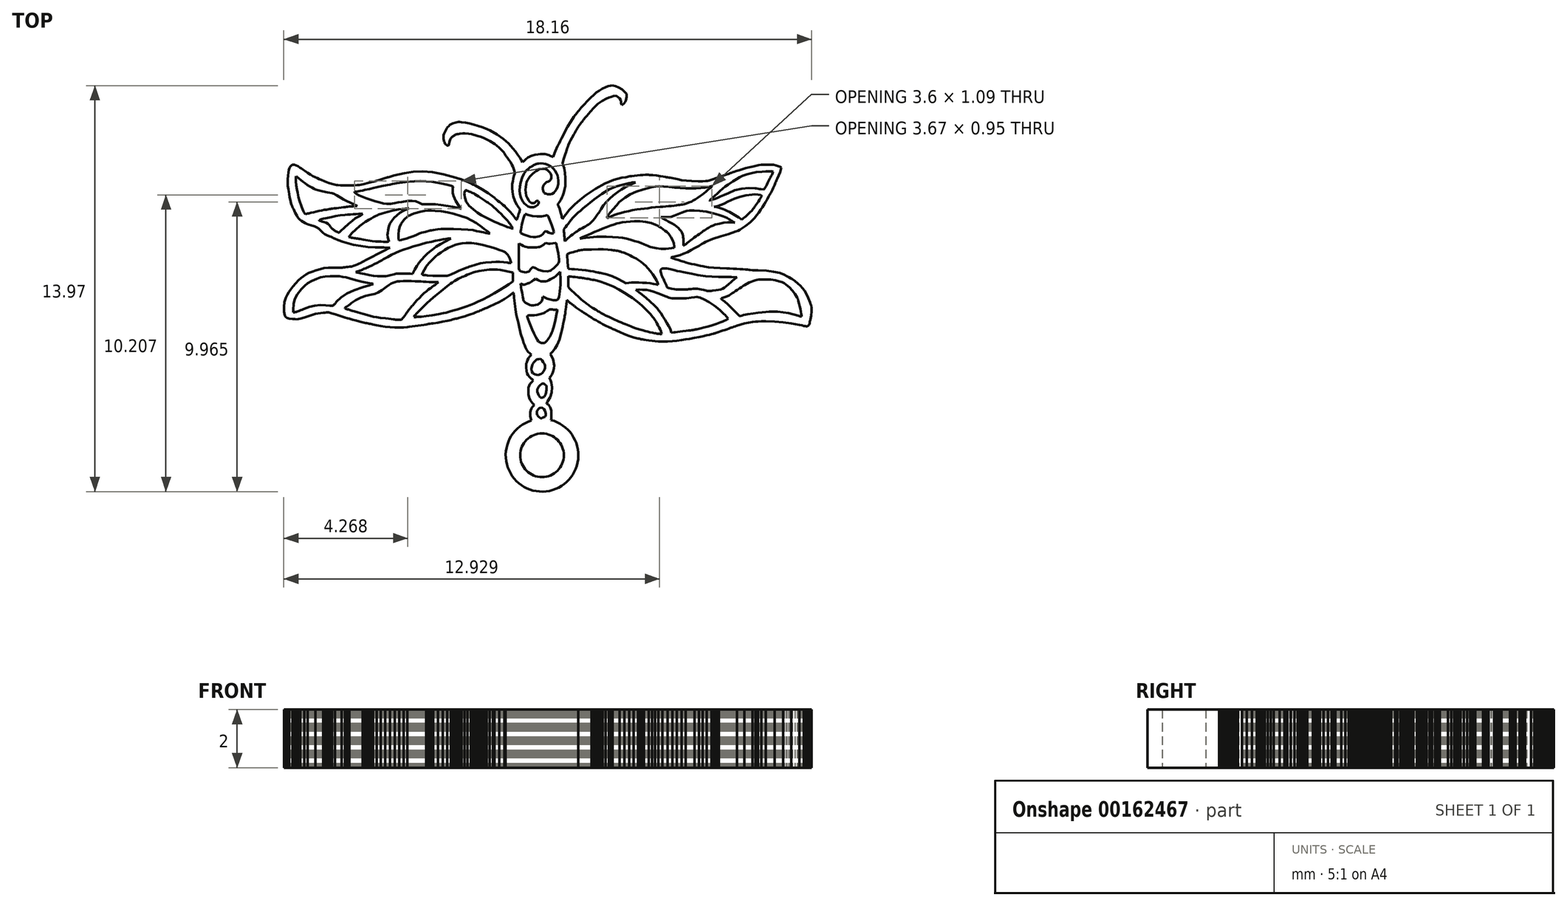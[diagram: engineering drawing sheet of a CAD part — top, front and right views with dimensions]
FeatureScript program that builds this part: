
annotation { "Feature Type Name" : "Feature", "Feature Type Description" : "" }
export const myFeature = defineFeature(function(context is Context, id is Id, definition is map)
    precondition{}
    {
        {
            var Q0;
            Q0=qCreatedBy(makeId("Top.planeOp"),FACE);
            var sketch = newSketch(context, id + "F0", { "sketchPlane" : qUnion([Q0])});
            skLineSegment(sketch, "E0", {"start": v(-0.38, -5.85) * mm, "end": v(-0.42, -5.82) * mm});
            skLineSegment(sketch, "E1", {"start": v(-0.42, -5.82) * mm, "end": v(-0.47, -5.77) * mm});
            skLineSegment(sketch, "E2", {"start": v(-0.47, -5.77) * mm, "end": v(-0.52, -5.72) * mm});
            skLineSegment(sketch, "E3", {"start": v(-0.52, -5.72) * mm, "end": v(-0.56, -5.66) * mm});
            skLineSegment(sketch, "E4", {"start": v(-0.56, -5.66) * mm, "end": v(-0.6, -5.52) * mm});
            skLineSegment(sketch, "E5", {"start": v(-0.6, -5.52) * mm, "end": v(-0.6, -5.39) * mm});
            skLineSegment(sketch, "E6", {"start": v(-0.6, -5.39) * mm, "end": v(-0.58, -5.32) * mm});
            skLineSegment(sketch, "E7", {"start": v(-0.58, -5.32) * mm, "end": v(-0.56, -5.26) * mm});
            skLineSegment(sketch, "E8", {"start": v(-0.56, -5.26) * mm, "end": v(-0.53, -5.21) * mm});
            skLineSegment(sketch, "E9", {"start": v(-0.53, -5.21) * mm, "end": v(-0.5, -5.17) * mm});
            skLineSegment(sketch, "E10", {"start": v(-0.5, -5.17) * mm, "end": v(-0.46, -5.13) * mm});
            skLineSegment(sketch, "E11", {"start": v(-0.46, -5.13) * mm, "end": v(-0.52, -5.07) * mm});
            skLineSegment(sketch, "E12", {"start": v(-0.52, -5.07) * mm, "end": v(-0.6, -4.97) * mm});
            skLineSegment(sketch, "E13", {"start": v(-0.6, -4.97) * mm, "end": v(-0.64, -4.87) * mm});
            skLineSegment(sketch, "E14", {"start": v(-0.64, -4.87) * mm, "end": v(-0.66, -4.76) * mm});
            skLineSegment(sketch, "E15", {"start": v(-0.66, -4.76) * mm, "end": v(-0.67, -4.62) * mm});
            skLineSegment(sketch, "E16", {"start": v(-0.67, -4.62) * mm, "end": v(-0.66, -4.53) * mm});
            skLineSegment(sketch, "E17", {"start": v(-0.66, -4.53) * mm, "end": v(-0.64, -4.47) * mm});
            skLineSegment(sketch, "E18", {"start": v(-0.64, -4.47) * mm, "end": v(-0.6, -4.4) * mm});
            skLineSegment(sketch, "E19", {"start": v(-0.6, -4.4) * mm, "end": v(-0.55, -4.34) * mm});
            skLineSegment(sketch, "E20", {"start": v(-0.55, -4.34) * mm, "end": v(-0.5, -4.28) * mm});
            skLineSegment(sketch, "E21", {"start": v(-0.5, -4.28) * mm, "end": v(-0.52, -4.26) * mm});
            skLineSegment(sketch, "E22", {"start": v(-0.52, -4.26) * mm, "end": v(-0.54, -4.25) * mm});
            skLineSegment(sketch, "E23", {"start": v(-0.54, -4.25) * mm, "end": v(-0.56, -4.23) * mm});
            skLineSegment(sketch, "E24", {"start": v(-0.56, -4.23) * mm, "end": v(-0.6, -4.2) * mm});
            skLineSegment(sketch, "E25", {"start": v(-0.6, -4.2) * mm, "end": v(-0.62, -4.17) * mm});
            skLineSegment(sketch, "E26", {"start": v(-0.62, -4.17) * mm, "end": v(-0.67, -4.1) * mm});
            skLineSegment(sketch, "E27", {"start": v(-0.67, -4.1) * mm, "end": v(-0.7, -4.04) * mm});
            skLineSegment(sketch, "E28", {"start": v(-0.7, -4.04) * mm, "end": v(-0.73, -3.95) * mm});
            skLineSegment(sketch, "E29", {"start": v(-0.73, -3.95) * mm, "end": v(-0.74, -3.85) * mm});
            skLineSegment(sketch, "E30", {"start": v(-0.74, -3.85) * mm, "end": v(-0.74, -3.79) * mm});
            skLineSegment(sketch, "E31", {"start": v(-0.74, -3.79) * mm, "end": v(-0.74, -3.74) * mm});
            skLineSegment(sketch, "E32", {"start": v(-0.74, -3.74) * mm, "end": v(-0.73, -3.7) * mm});
            skLineSegment(sketch, "E33", {"start": v(-0.73, -3.7) * mm, "end": v(-0.72, -3.65) * mm});
            skLineSegment(sketch, "E34", {"start": v(-0.72, -3.65) * mm, "end": v(-0.7, -3.59) * mm});
            skLineSegment(sketch, "E35", {"start": v(-0.7, -3.59) * mm, "end": v(-0.67, -3.53) * mm});
            skLineSegment(sketch, "E36", {"start": v(-0.67, -3.53) * mm, "end": v(-0.63, -3.48) * mm});
            skLineSegment(sketch, "E37", {"start": v(-0.63, -3.48) * mm, "end": v(-0.6, -3.44) * mm});
            skLineSegment(sketch, "E38", {"start": v(-0.6, -3.44) * mm, "end": v(-0.56, -3.4) * mm});
            skLineSegment(sketch, "E39", {"start": v(-0.56, -3.4) * mm, "end": v(-0.62, -3.35) * mm});
            skLineSegment(sketch, "E40", {"start": v(-0.62, -3.35) * mm, "end": v(-0.67, -3.3) * mm});
            skLineSegment(sketch, "E41", {"start": v(-0.67, -3.3) * mm, "end": v(-0.72, -3.23) * mm});
            skLineSegment(sketch, "E42", {"start": v(-0.72, -3.23) * mm, "end": v(-0.77, -3.15) * mm});
            skLineSegment(sketch, "E43", {"start": v(-0.77, -3.15) * mm, "end": v(-0.8, -3.08) * mm});
            skLineSegment(sketch, "E44", {"start": v(-0.8, -3.08) * mm, "end": v(-0.8, -3.04) * mm});
            skLineSegment(sketch, "E45", {"start": v(-0.8, -3.04) * mm, "end": v(-0.82, -3) * mm});
            skLineSegment(sketch, "E46", {"start": v(-0.82, -3) * mm, "end": v(-0.84, -2.94) * mm});
            skLineSegment(sketch, "E47", {"start": v(-0.84, -2.94) * mm, "end": v(-0.86, -2.9) * mm});
            skLineSegment(sketch, "E48", {"start": v(-0.86, -2.9) * mm, "end": v(-0.93, -2.67) * mm});
            skLineSegment(sketch, "E49", {"start": v(-0.93, -2.67) * mm, "end": v(-1, -2.37) * mm});
            skLineSegment(sketch, "E50", {"start": v(-1, -2.37) * mm, "end": v(-1, -2.31) * mm});
            skLineSegment(sketch, "E51", {"start": v(-1, -2.31) * mm, "end": v(-1.02, -2.26) * mm});
            skLineSegment(sketch, "E52", {"start": v(-1.02, -2.26) * mm, "end": v(-1.03, -2.2) * mm});
            skLineSegment(sketch, "E53", {"start": v(-1.03, -2.2) * mm, "end": v(-1.04, -2.17) * mm});
            skLineSegment(sketch, "E54", {"start": v(-1.04, -2.17) * mm, "end": v(-1.08, -2.02) * mm});
            skLineSegment(sketch, "E55", {"start": v(-1.08, -2.02) * mm, "end": v(-1.1, -1.84) * mm});
            skLineSegment(sketch, "E56", {"start": v(-1.1, -1.84) * mm, "end": v(-1.14, -1.64) * mm});
            skLineSegment(sketch, "E57", {"start": v(-1.14, -1.64) * mm, "end": v(-1.16, -1.44) * mm});
            skLineSegment(sketch, "E58", {"start": v(-1.16, -1.44) * mm, "end": v(-1.16, -1.37) * mm});
            skLineSegment(sketch, "E59", {"start": v(-1.16, -1.37) * mm, "end": v(-1.17, -1.32) * mm});
            skLineSegment(sketch, "E60", {"start": v(-1.17, -1.32) * mm, "end": v(-1.17, -1.28) * mm});
            skLineSegment(sketch, "E61", {"start": v(-1.17, -1.28) * mm, "end": v(-1.18, -1.27) * mm});
            skLineSegment(sketch, "E62", {"start": v(-1.18, -1.27) * mm, "end": v(-1.19, -1.27) * mm});
            skLineSegment(sketch, "E63", {"start": v(-1.19, -1.27) * mm, "end": v(-1.22, -1.29) * mm});
            skLineSegment(sketch, "E64", {"start": v(-1.22, -1.29) * mm, "end": v(-1.33, -1.38) * mm});
            skLineSegment(sketch, "E65", {"start": v(-1.33, -1.38) * mm, "end": v(-1.5, -1.49) * mm});
            skLineSegment(sketch, "E66", {"start": v(-1.5, -1.49) * mm, "end": v(-1.67, -1.59) * mm});
            skLineSegment(sketch, "E67", {"start": v(-1.67, -1.59) * mm, "end": v(-1.84, -1.67) * mm});
            skLineSegment(sketch, "E68", {"start": v(-1.84, -1.67) * mm, "end": v(-1.89, -1.69) * mm});
            skLineSegment(sketch, "E69", {"start": v(-1.89, -1.69) * mm, "end": v(-1.94, -1.71) * mm});
            skLineSegment(sketch, "E70", {"start": v(-1.94, -1.71) * mm, "end": v(-2, -1.74) * mm});
            skLineSegment(sketch, "E71", {"start": v(-2, -1.74) * mm, "end": v(-2.05, -1.76) * mm});
            skLineSegment(sketch, "E72", {"start": v(-2.05, -1.76) * mm, "end": v(-2.1, -1.78) * mm});
            skLineSegment(sketch, "E73", {"start": v(-2.1, -1.78) * mm, "end": v(-2.15, -1.8) * mm});
            skLineSegment(sketch, "E74", {"start": v(-2.15, -1.8) * mm, "end": v(-2.2, -1.83) * mm});
            skLineSegment(sketch, "E75", {"start": v(-2.2, -1.83) * mm, "end": v(-2.24, -1.85) * mm});
            skLineSegment(sketch, "E76", {"start": v(-2.24, -1.85) * mm, "end": v(-2.28, -1.86) * mm});
            skLineSegment(sketch, "E77", {"start": v(-2.28, -1.86) * mm, "end": v(-2.32, -1.88) * mm});
            skLineSegment(sketch, "E78", {"start": v(-2.32, -1.88) * mm, "end": v(-2.37, -1.9) * mm});
            skLineSegment(sketch, "E79", {"start": v(-2.37, -1.9) * mm, "end": v(-2.41, -1.92) * mm});
            skLineSegment(sketch, "E80", {"start": v(-2.41, -1.92) * mm, "end": v(-2.47, -1.95) * mm});
            skLineSegment(sketch, "E81", {"start": v(-2.47, -1.95) * mm, "end": v(-2.55, -1.98) * mm});
            skLineSegment(sketch, "E82", {"start": v(-2.55, -1.98) * mm, "end": v(-2.65, -2.01) * mm});
            skLineSegment(sketch, "E83", {"start": v(-2.65, -2.01) * mm, "end": v(-2.75, -2.05) * mm});
            skLineSegment(sketch, "E84", {"start": v(-2.75, -2.05) * mm, "end": v(-2.86, -2.08) * mm});
            skLineSegment(sketch, "E85", {"start": v(-2.86, -2.08) * mm, "end": v(-2.96, -2.1) * mm});
            skLineSegment(sketch, "E86", {"start": v(-2.96, -2.1) * mm, "end": v(-3.05, -2.13) * mm});
            skLineSegment(sketch, "E87", {"start": v(-3.05, -2.13) * mm, "end": v(-3.12, -2.15) * mm});
            skLineSegment(sketch, "E88", {"start": v(-3.12, -2.15) * mm, "end": v(-3.16, -2.16) * mm});
            skLineSegment(sketch, "E89", {"start": v(-3.16, -2.16) * mm, "end": v(-3.22, -2.18) * mm});
            skLineSegment(sketch, "E90", {"start": v(-3.22, -2.18) * mm, "end": v(-3.27, -2.19) * mm});
            skLineSegment(sketch, "E91", {"start": v(-3.27, -2.19) * mm, "end": v(-3.32, -2.2) * mm});
            skLineSegment(sketch, "E92", {"start": v(-3.32, -2.2) * mm, "end": v(-3.45, -2.23) * mm});
            skLineSegment(sketch, "E93", {"start": v(-3.45, -2.23) * mm, "end": v(-3.6, -2.27) * mm});
            skLineSegment(sketch, "E94", {"start": v(-3.6, -2.27) * mm, "end": v(-3.78, -2.3) * mm});
            skLineSegment(sketch, "E95", {"start": v(-3.78, -2.3) * mm, "end": v(-3.93, -2.32) * mm});
            skLineSegment(sketch, "E96", {"start": v(-3.93, -2.32) * mm, "end": v(-4, -2.33) * mm});
            skLineSegment(sketch, "E97", {"start": v(-4, -2.33) * mm, "end": v(-4.05, -2.33) * mm});
            skLineSegment(sketch, "E98", {"start": v(-4.05, -2.33) * mm, "end": v(-4.1, -2.34) * mm});
            skLineSegment(sketch, "E99", {"start": v(-4.1, -2.34) * mm, "end": v(-4.13, -2.35) * mm});
            skLineSegment(sketch, "E100", {"start": v(-4.13, -2.35) * mm, "end": v(-4.18, -2.36) * mm});
            skLineSegment(sketch, "E101", {"start": v(-4.18, -2.36) * mm, "end": v(-4.26, -2.37) * mm});
            skLineSegment(sketch, "E102", {"start": v(-4.26, -2.37) * mm, "end": v(-4.36, -2.38) * mm});
            skLineSegment(sketch, "E103", {"start": v(-4.36, -2.38) * mm, "end": v(-4.46, -2.4) * mm});
            skLineSegment(sketch, "E104", {"start": v(-4.46, -2.4) * mm, "end": v(-4.57, -2.42) * mm});
            skLineSegment(sketch, "E105", {"start": v(-4.57, -2.42) * mm, "end": v(-4.67, -2.43) * mm});
            skLineSegment(sketch, "E106", {"start": v(-4.67, -2.43) * mm, "end": v(-4.76, -2.44) * mm});
            skLineSegment(sketch, "E107", {"start": v(-4.76, -2.44) * mm, "end": v(-4.83, -2.45) * mm});
            skLineSegment(sketch, "E108", {"start": v(-4.83, -2.45) * mm, "end": v(-4.96, -2.46) * mm});
            skLineSegment(sketch, "E109", {"start": v(-4.96, -2.46) * mm, "end": v(-5.1, -2.47) * mm});
            skLineSegment(sketch, "E110", {"start": v(-5.1, -2.47) * mm, "end": v(-5.26, -2.46) * mm});
            skLineSegment(sketch, "E111", {"start": v(-5.26, -2.46) * mm, "end": v(-5.42, -2.45) * mm});
            skLineSegment(sketch, "E112", {"start": v(-5.42, -2.45) * mm, "end": v(-5.59, -2.44) * mm});
            skLineSegment(sketch, "E113", {"start": v(-5.59, -2.44) * mm, "end": v(-5.74, -2.42) * mm});
            skLineSegment(sketch, "E114", {"start": v(-5.74, -2.42) * mm, "end": v(-5.88, -2.4) * mm});
            skLineSegment(sketch, "E115", {"start": v(-5.88, -2.4) * mm, "end": v(-6, -2.36) * mm});
            skLineSegment(sketch, "E116", {"start": v(-6, -2.36) * mm, "end": v(-6.05, -2.35) * mm});
            skLineSegment(sketch, "E117", {"start": v(-6.05, -2.35) * mm, "end": v(-6.1, -2.34) * mm});
            skLineSegment(sketch, "E118", {"start": v(-6.1, -2.34) * mm, "end": v(-6.14, -2.33) * mm});
            skLineSegment(sketch, "E119", {"start": v(-6.14, -2.33) * mm, "end": v(-6.18, -2.32) * mm});
            skLineSegment(sketch, "E120", {"start": v(-6.18, -2.32) * mm, "end": v(-6.22, -2.32) * mm});
            skLineSegment(sketch, "E121", {"start": v(-6.22, -2.32) * mm, "end": v(-6.27, -2.3) * mm});
            skLineSegment(sketch, "E122", {"start": v(-6.27, -2.3) * mm, "end": v(-6.32, -2.3) * mm});
            skLineSegment(sketch, "E123", {"start": v(-6.32, -2.3) * mm, "end": v(-6.36, -2.28) * mm});
            skLineSegment(sketch, "E124", {"start": v(-6.36, -2.28) * mm, "end": v(-6.47, -2.25) * mm});
            skLineSegment(sketch, "E125", {"start": v(-6.47, -2.25) * mm, "end": v(-6.59, -2.22) * mm});
            skLineSegment(sketch, "E126", {"start": v(-6.59, -2.22) * mm, "end": v(-6.71, -2.2) * mm});
            skLineSegment(sketch, "E127", {"start": v(-6.71, -2.2) * mm, "end": v(-6.82, -2.16) * mm});
            skLineSegment(sketch, "E128", {"start": v(-6.82, -2.16) * mm, "end": v(-6.89, -2.15) * mm});
            skLineSegment(sketch, "E129", {"start": v(-6.89, -2.15) * mm, "end": v(-6.98, -2.12) * mm});
            skLineSegment(sketch, "E130", {"start": v(-6.98, -2.12) * mm, "end": v(-7.1, -2.08) * mm});
            skLineSegment(sketch, "E131", {"start": v(-7.1, -2.08) * mm, "end": v(-7.2, -2.05) * mm});
            skLineSegment(sketch, "E132", {"start": v(-7.2, -2.05) * mm, "end": v(-7.32, -2) * mm});
            skLineSegment(sketch, "E133", {"start": v(-7.32, -2) * mm, "end": v(-7.42, -1.98) * mm});
            skLineSegment(sketch, "E134", {"start": v(-7.42, -1.98) * mm, "end": v(-7.49, -1.96) * mm});
            skLineSegment(sketch, "E135", {"start": v(-7.49, -1.96) * mm, "end": v(-7.53, -1.95) * mm});
            skLineSegment(sketch, "E136", {"start": v(-7.53, -1.95) * mm, "end": v(-7.56, -1.95) * mm});
            skLineSegment(sketch, "E137", {"start": v(-7.56, -1.95) * mm, "end": v(-7.6, -1.95) * mm});
            skLineSegment(sketch, "E138", {"start": v(-7.6, -1.95) * mm, "end": v(-7.66, -1.95) * mm});
            skLineSegment(sketch, "E139", {"start": v(-7.66, -1.95) * mm, "end": v(-7.72, -1.96) * mm});
            skLineSegment(sketch, "E140", {"start": v(-7.72, -1.96) * mm, "end": v(-7.99, -2) * mm});
            skLineSegment(sketch, "E141", {"start": v(-7.99, -2) * mm, "end": v(-8.25, -2.08) * mm});
            skLineSegment(sketch, "E142", {"start": v(-8.25, -2.08) * mm, "end": v(-8.38, -2.13) * mm});
            skLineSegment(sketch, "E143", {"start": v(-8.38, -2.13) * mm, "end": v(-8.5, -2.16) * mm});
            skLineSegment(sketch, "E144", {"start": v(-8.5, -2.16) * mm, "end": v(-8.58, -2.17) * mm});
            skLineSegment(sketch, "E145", {"start": v(-8.58, -2.17) * mm, "end": v(-8.64, -2.18) * mm});
            skLineSegment(sketch, "E146", {"start": v(-8.64, -2.18) * mm, "end": v(-8.7, -2.18) * mm});
            skLineSegment(sketch, "E147", {"start": v(-8.7, -2.18) * mm, "end": v(-8.78, -2.17) * mm});
            skLineSegment(sketch, "E148", {"start": v(-8.78, -2.17) * mm, "end": v(-8.9, -2.16) * mm});
            skLineSegment(sketch, "E149", {"start": v(-8.9, -2.16) * mm, "end": v(-8.97, -2.14) * mm});
            skLineSegment(sketch, "E150", {"start": v(-8.97, -2.14) * mm, "end": v(-9.01, -2.1) * mm});
            skLineSegment(sketch, "E151", {"start": v(-9.01, -2.1) * mm, "end": v(-9.05, -2.04) * mm});
            skLineSegment(sketch, "E152", {"start": v(-9.05, -2.04) * mm, "end": v(-9.07, -1.92) * mm});
            skLineSegment(sketch, "E153", {"start": v(-9.07, -1.92) * mm, "end": v(-9.08, -1.76) * mm});
            skLineSegment(sketch, "E154", {"start": v(-9.08, -1.76) * mm, "end": v(-9.05, -1.6) * mm});
            skLineSegment(sketch, "E155", {"start": v(-9.05, -1.6) * mm, "end": v(-9, -1.44) * mm});
            skLineSegment(sketch, "E156", {"start": v(-9, -1.44) * mm, "end": v(-8.96, -1.33) * mm});
            skLineSegment(sketch, "E157", {"start": v(-8.96, -1.33) * mm, "end": v(-8.9, -1.24) * mm});
            skLineSegment(sketch, "E158", {"start": v(-8.9, -1.24) * mm, "end": v(-8.85, -1.15) * mm});
            skLineSegment(sketch, "E159", {"start": v(-8.85, -1.15) * mm, "end": v(-8.77, -1.06) * mm});
            skLineSegment(sketch, "E160", {"start": v(-8.77, -1.06) * mm, "end": v(-8.67, -0.94) * mm});
            skLineSegment(sketch, "E161", {"start": v(-8.67, -0.94) * mm, "end": v(-8.57, -0.84) * mm});
            skLineSegment(sketch, "E162", {"start": v(-8.57, -0.84) * mm, "end": v(-8.49, -0.76) * mm});
            skLineSegment(sketch, "E163", {"start": v(-8.49, -0.76) * mm, "end": v(-8.4, -0.7) * mm});
            skLineSegment(sketch, "E164", {"start": v(-8.4, -0.7) * mm, "end": v(-8.31, -0.64) * mm});
            skLineSegment(sketch, "E165", {"start": v(-8.31, -0.64) * mm, "end": v(-8.21, -0.6) * mm});
            skLineSegment(sketch, "E166", {"start": v(-8.21, -0.6) * mm, "end": v(-8.1, -0.54) * mm});
            skLineSegment(sketch, "E167", {"start": v(-8.1, -0.54) * mm, "end": v(-7.97, -0.5) * mm});
            skLineSegment(sketch, "E168", {"start": v(-7.97, -0.5) * mm, "end": v(-7.83, -0.45) * mm});
            skLineSegment(sketch, "E169", {"start": v(-7.83, -0.45) * mm, "end": v(-7.7, -0.43) * mm});
            skLineSegment(sketch, "E170", {"start": v(-7.7, -0.43) * mm, "end": v(-7.55, -0.41) * mm});
            skLineSegment(sketch, "E171", {"start": v(-7.55, -0.41) * mm, "end": v(-7.34, -0.4) * mm});
            skLineSegment(sketch, "E172", {"start": v(-7.34, -0.4) * mm, "end": v(-7.23, -0.4) * mm});
            skLineSegment(sketch, "E173", {"start": v(-7.23, -0.4) * mm, "end": v(-7.13, -0.4) * mm});
            skLineSegment(sketch, "E174", {"start": v(-7.13, -0.4) * mm, "end": v(-7.06, -0.4) * mm});
            skLineSegment(sketch, "E175", {"start": v(-7.06, -0.4) * mm, "end": v(-7.03, -0.4) * mm});
            skLineSegment(sketch, "E176", {"start": v(-7.03, -0.4) * mm, "end": v(-7, -0.4) * mm});
            skLineSegment(sketch, "E177", {"start": v(-7, -0.4) * mm, "end": v(-6.97, -0.4) * mm});
            skLineSegment(sketch, "E178", {"start": v(-6.97, -0.4) * mm, "end": v(-6.92, -0.39) * mm});
            skLineSegment(sketch, "E179", {"start": v(-6.92, -0.39) * mm, "end": v(-6.87, -0.38) * mm});
            skLineSegment(sketch, "E180", {"start": v(-6.87, -0.38) * mm, "end": v(-6.8, -0.37) * mm});
            skLineSegment(sketch, "E181", {"start": v(-6.8, -0.37) * mm, "end": v(-6.75, -0.36) * mm});
            skLineSegment(sketch, "E182", {"start": v(-6.75, -0.36) * mm, "end": v(-6.69, -0.34) * mm});
            skLineSegment(sketch, "E183", {"start": v(-6.69, -0.34) * mm, "end": v(-6.6, -0.31) * mm});
            skLineSegment(sketch, "E184", {"start": v(-6.6, -0.31) * mm, "end": v(-6.55, -0.29) * mm});
            skLineSegment(sketch, "E185", {"start": v(-6.55, -0.29) * mm, "end": v(-6.49, -0.26) * mm});
            skLineSegment(sketch, "E186", {"start": v(-6.49, -0.26) * mm, "end": v(-6.43, -0.24) * mm});
            skLineSegment(sketch, "E187", {"start": v(-6.43, -0.24) * mm, "end": v(-6.4, -0.22) * mm});
            skLineSegment(sketch, "E188", {"start": v(-6.4, -0.22) * mm, "end": v(-6.2, -0.12) * mm});
            skLineSegment(sketch, "E189", {"start": v(-6.2, -0.12) * mm, "end": v(-6.02, -0.03) * mm});
            skLineSegment(sketch, "E190", {"start": v(-6.02, -0.03) * mm, "end": v(-5.88, 0.05) * mm});
            skLineSegment(sketch, "E191", {"start": v(-5.88, 0.05) * mm, "end": v(-5.77, 0.1) * mm});
            skLineSegment(sketch, "E192", {"start": v(-5.77, 0.1) * mm, "end": v(-5.68, 0.16) * mm});
            skLineSegment(sketch, "E193", {"start": v(-5.68, 0.16) * mm, "end": v(-5.58, 0.2) * mm});
            skLineSegment(sketch, "E194", {"start": v(-5.58, 0.2) * mm, "end": v(-5.49, 0.25) * mm});
            skLineSegment(sketch, "E195", {"start": v(-5.49, 0.25) * mm, "end": v(-5.42, 0.28) * mm});
            skLineSegment(sketch, "E196", {"start": v(-5.42, 0.28) * mm, "end": v(-5.43, 0.28) * mm});
            skLineSegment(sketch, "E197", {"start": v(-5.43, 0.28) * mm, "end": v(-5.48, 0.28) * mm});
            skLineSegment(sketch, "E198", {"start": v(-5.48, 0.28) * mm, "end": v(-5.54, 0.29) * mm});
            skLineSegment(sketch, "E199", {"start": v(-5.54, 0.29) * mm, "end": v(-5.62, 0.29) * mm});
            skLineSegment(sketch, "E200", {"start": v(-5.62, 0.29) * mm, "end": v(-5.93, 0.3) * mm});
            skLineSegment(sketch, "E201", {"start": v(-5.93, 0.3) * mm, "end": v(-6.19, 0.3) * mm});
            skLineSegment(sketch, "E202", {"start": v(-6.19, 0.3) * mm, "end": v(-6.43, 0.34) * mm});
            skLineSegment(sketch, "E203", {"start": v(-6.43, 0.34) * mm, "end": v(-6.68, 0.39) * mm});
            skLineSegment(sketch, "E204", {"start": v(-6.68, 0.39) * mm, "end": v(-6.85, 0.43) * mm});
            skLineSegment(sketch, "E205", {"start": v(-6.85, 0.43) * mm, "end": v(-7.04, 0.49) * mm});
            skLineSegment(sketch, "E206", {"start": v(-7.04, 0.49) * mm, "end": v(-7.21, 0.55) * mm});
            skLineSegment(sketch, "E207", {"start": v(-7.21, 0.55) * mm, "end": v(-7.34, 0.6) * mm});
            skLineSegment(sketch, "E208", {"start": v(-7.34, 0.6) * mm, "end": v(-7.37, 0.61) * mm});
            skLineSegment(sketch, "E209", {"start": v(-7.37, 0.61) * mm, "end": v(-7.41, 0.63) * mm});
            skLineSegment(sketch, "E210", {"start": v(-7.41, 0.63) * mm, "end": v(-7.46, 0.65) * mm});
            skLineSegment(sketch, "E211", {"start": v(-7.46, 0.65) * mm, "end": v(-7.5, 0.67) * mm});
            skLineSegment(sketch, "E212", {"start": v(-7.5, 0.67) * mm, "end": v(-7.6, 0.71) * mm});
            skLineSegment(sketch, "E213", {"start": v(-7.6, 0.71) * mm, "end": v(-7.67, 0.75) * mm});
            skLineSegment(sketch, "E214", {"start": v(-7.67, 0.75) * mm, "end": v(-7.73, 0.8) * mm});
            skLineSegment(sketch, "E215", {"start": v(-7.73, 0.8) * mm, "end": v(-7.8, 0.88) * mm});
            skLineSegment(sketch, "E216", {"start": v(-7.8, 0.88) * mm, "end": v(-7.84, 0.9) * mm});
            skLineSegment(sketch, "E217", {"start": v(-7.84, 0.9) * mm, "end": v(-7.87, 0.94) * mm});
            skLineSegment(sketch, "E218", {"start": v(-7.87, 0.94) * mm, "end": v(-7.9, 0.96) * mm});
            skLineSegment(sketch, "E219", {"start": v(-7.9, 0.96) * mm, "end": v(-7.92, 0.97) * mm});
            skLineSegment(sketch, "E220", {"start": v(-7.92, 0.97) * mm, "end": v(-7.94, 0.98) * mm});
            skLineSegment(sketch, "E221", {"start": v(-7.94, 0.98) * mm, "end": v(-7.96, 1) * mm});
            skLineSegment(sketch, "E222", {"start": v(-7.96, 1) * mm, "end": v(-7.99, 1) * mm});
            skLineSegment(sketch, "E223", {"start": v(-7.99, 1) * mm, "end": v(-8.02, 1.01) * mm});
            skLineSegment(sketch, "E224", {"start": v(-8.02, 1.01) * mm, "end": v(-8.14, 1.05) * mm});
            skLineSegment(sketch, "E225", {"start": v(-8.14, 1.05) * mm, "end": v(-8.23, 1.08) * mm});
            skLineSegment(sketch, "E226", {"start": v(-8.23, 1.08) * mm, "end": v(-8.3, 1.1) * mm});
            skLineSegment(sketch, "E227", {"start": v(-8.3, 1.1) * mm, "end": v(-8.35, 1.13) * mm});
            skLineSegment(sketch, "E228", {"start": v(-8.35, 1.13) * mm, "end": v(-8.41, 1.17) * mm});
            skLineSegment(sketch, "E229", {"start": v(-8.41, 1.17) * mm, "end": v(-8.47, 1.2) * mm});
            skLineSegment(sketch, "E230", {"start": v(-8.47, 1.2) * mm, "end": v(-8.52, 1.24) * mm});
            skLineSegment(sketch, "E231", {"start": v(-8.52, 1.24) * mm, "end": v(-8.55, 1.27) * mm});
            skLineSegment(sketch, "E232", {"start": v(-8.55, 1.27) * mm, "end": v(-8.59, 1.31) * mm});
            skLineSegment(sketch, "E233", {"start": v(-8.59, 1.31) * mm, "end": v(-8.63, 1.39) * mm});
            skLineSegment(sketch, "E234", {"start": v(-8.63, 1.39) * mm, "end": v(-8.68, 1.49) * mm});
            skLineSegment(sketch, "E235", {"start": v(-8.68, 1.49) * mm, "end": v(-8.74, 1.6) * mm});
            skLineSegment(sketch, "E236", {"start": v(-8.74, 1.6) * mm, "end": v(-8.77, 1.67) * mm});
            skLineSegment(sketch, "E237", {"start": v(-8.77, 1.67) * mm, "end": v(-8.8, 1.71) * mm});
            skLineSegment(sketch, "E238", {"start": v(-8.8, 1.71) * mm, "end": v(-8.81, 1.76) * mm});
            skLineSegment(sketch, "E239", {"start": v(-8.81, 1.76) * mm, "end": v(-8.83, 1.8) * mm});
            skLineSegment(sketch, "E240", {"start": v(-8.83, 1.8) * mm, "end": v(-8.84, 1.86) * mm});
            skLineSegment(sketch, "E241", {"start": v(-8.84, 1.86) * mm, "end": v(-8.86, 1.93) * mm});
            skLineSegment(sketch, "E242", {"start": v(-8.86, 1.93) * mm, "end": v(-8.87, 2.02) * mm});
            skLineSegment(sketch, "E243", {"start": v(-8.87, 2.02) * mm, "end": v(-8.9, 2.13) * mm});
            skLineSegment(sketch, "E244", {"start": v(-8.9, 2.13) * mm, "end": v(-8.92, 2.29) * mm});
            skLineSegment(sketch, "E245", {"start": v(-8.92, 2.29) * mm, "end": v(-8.94, 2.41) * mm});
            skLineSegment(sketch, "E246", {"start": v(-8.94, 2.41) * mm, "end": v(-8.94, 2.52) * mm});
            skLineSegment(sketch, "E247", {"start": v(-8.94, 2.52) * mm, "end": v(-8.94, 2.63) * mm});
            skLineSegment(sketch, "E248", {"start": v(-8.94, 2.63) * mm, "end": v(-8.93, 2.76) * mm});
            skLineSegment(sketch, "E249", {"start": v(-8.93, 2.76) * mm, "end": v(-8.92, 2.87) * mm});
            skLineSegment(sketch, "E250", {"start": v(-8.92, 2.87) * mm, "end": v(-8.9, 2.96) * mm});
            skLineSegment(sketch, "E251", {"start": v(-8.9, 2.96) * mm, "end": v(-8.87, 3.03) * mm});
            skLineSegment(sketch, "E252", {"start": v(-8.87, 3.03) * mm, "end": v(-8.85, 3.08) * mm});
            skLineSegment(sketch, "E253", {"start": v(-8.85, 3.08) * mm, "end": v(-8.82, 3.11) * mm});
            skLineSegment(sketch, "E254", {"start": v(-8.82, 3.11) * mm, "end": v(-8.79, 3.14) * mm});
            skLineSegment(sketch, "E255", {"start": v(-8.79, 3.14) * mm, "end": v(-8.75, 3.14) * mm});
            skLineSegment(sketch, "E256", {"start": v(-8.75, 3.14) * mm, "end": v(-8.7, 3.14) * mm});
            skLineSegment(sketch, "E257", {"start": v(-8.7, 3.14) * mm, "end": v(-8.66, 3.12) * mm});
            skLineSegment(sketch, "E258", {"start": v(-8.66, 3.12) * mm, "end": v(-8.6, 3.08) * mm});
            skLineSegment(sketch, "E259", {"start": v(-8.6, 3.08) * mm, "end": v(-8.52, 3.04) * mm});
            skLineSegment(sketch, "E260", {"start": v(-8.52, 3.04) * mm, "end": v(-8.47, 3) * mm});
            skLineSegment(sketch, "E261", {"start": v(-8.47, 3) * mm, "end": v(-8.43, 2.98) * mm});
            skLineSegment(sketch, "E262", {"start": v(-8.43, 2.98) * mm, "end": v(-8.38, 2.94) * mm});
            skLineSegment(sketch, "E263", {"start": v(-8.38, 2.94) * mm, "end": v(-8.34, 2.92) * mm});
            skLineSegment(sketch, "E264", {"start": v(-8.34, 2.92) * mm, "end": v(-8.25, 2.85) * mm});
            skLineSegment(sketch, "E265", {"start": v(-8.25, 2.85) * mm, "end": v(-8.16, 2.8) * mm});
            skLineSegment(sketch, "E266", {"start": v(-8.16, 2.8) * mm, "end": v(-8.07, 2.74) * mm});
            skLineSegment(sketch, "E267", {"start": v(-8.07, 2.74) * mm, "end": v(-8.02, 2.71) * mm});
            skLineSegment(sketch, "E268", {"start": v(-8.02, 2.71) * mm, "end": v(-7.99, 2.7) * mm});
            skLineSegment(sketch, "E269", {"start": v(-7.99, 2.7) * mm, "end": v(-7.93, 2.68) * mm});
            skLineSegment(sketch, "E270", {"start": v(-7.93, 2.68) * mm, "end": v(-7.86, 2.65) * mm});
            skLineSegment(sketch, "E271", {"start": v(-7.86, 2.65) * mm, "end": v(-7.79, 2.61) * mm});
            skLineSegment(sketch, "E272", {"start": v(-7.79, 2.61) * mm, "end": v(-7.67, 2.56) * mm});
            skLineSegment(sketch, "E273", {"start": v(-7.67, 2.56) * mm, "end": v(-7.55, 2.52) * mm});
            skLineSegment(sketch, "E274", {"start": v(-7.55, 2.52) * mm, "end": v(-7.42, 2.48) * mm});
            skLineSegment(sketch, "E275", {"start": v(-7.42, 2.48) * mm, "end": v(-7.27, 2.44) * mm});
            skLineSegment(sketch, "E276", {"start": v(-7.27, 2.44) * mm, "end": v(-7.22, 2.43) * mm});
            skLineSegment(sketch, "E277", {"start": v(-7.22, 2.43) * mm, "end": v(-7.13, 2.43) * mm});
            skLineSegment(sketch, "E278", {"start": v(-7.13, 2.43) * mm, "end": v(-7.02, 2.43) * mm});
            skLineSegment(sketch, "E279", {"start": v(-7.02, 2.43) * mm, "end": v(-6.9, 2.43) * mm});
            skLineSegment(sketch, "E280", {"start": v(-6.9, 2.43) * mm, "end": v(-6.77, 2.43) * mm});
            skLineSegment(sketch, "E281", {"start": v(-6.77, 2.43) * mm, "end": v(-6.65, 2.43) * mm});
            skLineSegment(sketch, "E282", {"start": v(-6.65, 2.43) * mm, "end": v(-6.55, 2.43) * mm});
            skLineSegment(sketch, "E283", {"start": v(-6.55, 2.43) * mm, "end": v(-6.48, 2.44) * mm});
            skLineSegment(sketch, "E284", {"start": v(-6.48, 2.44) * mm, "end": v(-6.35, 2.47) * mm});
            skLineSegment(sketch, "E285", {"start": v(-6.35, 2.47) * mm, "end": v(-6.16, 2.51) * mm});
            skLineSegment(sketch, "E286", {"start": v(-6.16, 2.51) * mm, "end": v(-5.95, 2.57) * mm});
            skLineSegment(sketch, "E287", {"start": v(-5.95, 2.57) * mm, "end": v(-5.75, 2.63) * mm});
            skLineSegment(sketch, "E288", {"start": v(-5.75, 2.63) * mm, "end": v(-5.66, 2.66) * mm});
            skLineSegment(sketch, "E289", {"start": v(-5.66, 2.66) * mm, "end": v(-5.6, 2.68) * mm});
            skLineSegment(sketch, "E290", {"start": v(-5.6, 2.68) * mm, "end": v(-5.54, 2.7) * mm});
            skLineSegment(sketch, "E291", {"start": v(-5.54, 2.7) * mm, "end": v(-5.51, 2.7) * mm});
            skLineSegment(sketch, "E292", {"start": v(-5.51, 2.7) * mm, "end": v(-5.49, 2.7) * mm});
            skLineSegment(sketch, "E293", {"start": v(-5.49, 2.7) * mm, "end": v(-5.43, 2.72) * mm});
            skLineSegment(sketch, "E294", {"start": v(-5.43, 2.72) * mm, "end": v(-5.36, 2.74) * mm});
            skLineSegment(sketch, "E295", {"start": v(-5.36, 2.74) * mm, "end": v(-5.28, 2.76) * mm});
            skLineSegment(sketch, "E296", {"start": v(-5.28, 2.76) * mm, "end": v(-4.93, 2.84) * mm});
            skLineSegment(sketch, "E297", {"start": v(-4.93, 2.84) * mm, "end": v(-4.63, 2.9) * mm});
            skLineSegment(sketch, "E298", {"start": v(-4.63, 2.9) * mm, "end": v(-4.3, 2.9) * mm});
            skLineSegment(sketch, "E299", {"start": v(-4.3, 2.9) * mm, "end": v(-3.96, 2.88) * mm});
            skLineSegment(sketch, "E300", {"start": v(-3.96, 2.88) * mm, "end": v(-3.58, 2.81) * mm});
            skLineSegment(sketch, "E301", {"start": v(-3.58, 2.81) * mm, "end": v(-3.17, 2.7) * mm});
            skLineSegment(sketch, "E302", {"start": v(-3.17, 2.7) * mm, "end": v(-3.08, 2.67) * mm});
            skLineSegment(sketch, "E303", {"start": v(-3.08, 2.67) * mm, "end": v(-3, 2.64) * mm});
            skLineSegment(sketch, "E304", {"start": v(-3, 2.64) * mm, "end": v(-2.9, 2.6) * mm});
            skLineSegment(sketch, "E305", {"start": v(-2.9, 2.6) * mm, "end": v(-2.8, 2.56) * mm});
            skLineSegment(sketch, "E306", {"start": v(-2.8, 2.56) * mm, "end": v(-2.7, 2.53) * mm});
            skLineSegment(sketch, "E307", {"start": v(-2.7, 2.53) * mm, "end": v(-2.62, 2.49) * mm});
            skLineSegment(sketch, "E308", {"start": v(-2.62, 2.49) * mm, "end": v(-2.55, 2.46) * mm});
            skLineSegment(sketch, "E309", {"start": v(-2.55, 2.46) * mm, "end": v(-2.5, 2.43) * mm});
            skLineSegment(sketch, "E310", {"start": v(-2.5, 2.43) * mm, "end": v(-2.25, 2.28) * mm});
            skLineSegment(sketch, "E311", {"start": v(-2.25, 2.28) * mm, "end": v(-2.05, 2.16) * mm});
            skLineSegment(sketch, "E312", {"start": v(-2.05, 2.16) * mm, "end": v(-1.9, 2.06) * mm});
            skLineSegment(sketch, "E313", {"start": v(-1.9, 2.06) * mm, "end": v(-1.82, 2) * mm});
            skLineSegment(sketch, "E314", {"start": v(-1.82, 2) * mm, "end": v(-1.8, 1.97) * mm});
            skLineSegment(sketch, "E315", {"start": v(-1.8, 1.97) * mm, "end": v(-1.76, 1.94) * mm});
            skLineSegment(sketch, "E316", {"start": v(-1.76, 1.94) * mm, "end": v(-1.7, 1.9) * mm});
            skLineSegment(sketch, "E317", {"start": v(-1.7, 1.9) * mm, "end": v(-1.65, 1.85) * mm});
            skLineSegment(sketch, "E318", {"start": v(-1.65, 1.85) * mm, "end": v(-1.6, 1.8) * mm});
            skLineSegment(sketch, "E319", {"start": v(-1.6, 1.8) * mm, "end": v(-1.53, 1.75) * mm});
            skLineSegment(sketch, "E320", {"start": v(-1.53, 1.75) * mm, "end": v(-1.48, 1.71) * mm});
            skLineSegment(sketch, "E321", {"start": v(-1.48, 1.71) * mm, "end": v(-1.44, 1.68) * mm});
            skLineSegment(sketch, "E322", {"start": v(-1.44, 1.68) * mm, "end": v(-1.38, 1.62) * mm});
            skLineSegment(sketch, "E323", {"start": v(-1.38, 1.62) * mm, "end": v(-1.3, 1.53) * mm});
            skLineSegment(sketch, "E324", {"start": v(-1.3, 1.53) * mm, "end": v(-1.21, 1.42) * mm});
            skLineSegment(sketch, "E325", {"start": v(-1.21, 1.42) * mm, "end": v(-1.13, 1.32) * mm});
            skLineSegment(sketch, "E326", {"start": v(-1.13, 1.32) * mm, "end": v(-1.1, 1.28) * mm});
            skLineSegment(sketch, "E327", {"start": v(-1.1, 1.28) * mm, "end": v(-1.08, 1.26) * mm});
            skLineSegment(sketch, "E328", {"start": v(-1.08, 1.26) * mm, "end": v(-1.06, 1.24) * mm});
            skLineSegment(sketch, "E329", {"start": v(-1.06, 1.24) * mm, "end": v(-1.06, 1.24) * mm});
            skLineSegment(sketch, "E330", {"start": v(-1.06, 1.24) * mm, "end": v(-1.05, 1.26) * mm});
            skLineSegment(sketch, "E331", {"start": v(-1.05, 1.26) * mm, "end": v(-1.04, 1.3) * mm});
            skLineSegment(sketch, "E332", {"start": v(-1.04, 1.3) * mm, "end": v(-1.02, 1.36) * mm});
            skLineSegment(sketch, "E333", {"start": v(-1.02, 1.36) * mm, "end": v(-1, 1.43) * mm});
            skLineSegment(sketch, "E334", {"start": v(-1, 1.43) * mm, "end": v(-0.98, 1.48) * mm});
            skLineSegment(sketch, "E335", {"start": v(-0.98, 1.48) * mm, "end": v(-0.97, 1.52) * mm});
            skLineSegment(sketch, "E336", {"start": v(-0.97, 1.52) * mm, "end": v(-0.96, 1.55) * mm});
            skLineSegment(sketch, "E337", {"start": v(-0.96, 1.55) * mm, "end": v(-0.96, 1.58) * mm});
            skLineSegment(sketch, "E338", {"start": v(-0.96, 1.58) * mm, "end": v(-0.96, 1.6) * mm});
            skLineSegment(sketch, "E339", {"start": v(-0.96, 1.6) * mm, "end": v(-0.96, 1.6) * mm});
            skLineSegment(sketch, "E340", {"start": v(-0.96, 1.6) * mm, "end": v(-0.96, 1.61) * mm});
            skLineSegment(sketch, "E341", {"start": v(-0.96, 1.61) * mm, "end": v(-0.96, 1.62) * mm});
            skLineSegment(sketch, "E342", {"start": v(-0.96, 1.62) * mm, "end": v(-1, 1.68) * mm});
            skLineSegment(sketch, "E343", {"start": v(-1, 1.68) * mm, "end": v(-1.06, 1.76) * mm});
            skLineSegment(sketch, "E344", {"start": v(-1.06, 1.76) * mm, "end": v(-1.1, 1.84) * mm});
            skLineSegment(sketch, "E345", {"start": v(-1.1, 1.84) * mm, "end": v(-1.14, 1.9) * mm});
            skLineSegment(sketch, "E346", {"start": v(-1.14, 1.9) * mm, "end": v(-1.18, 2.05) * mm});
            skLineSegment(sketch, "E347", {"start": v(-1.18, 2.05) * mm, "end": v(-1.2, 2.2) * mm});
            skLineSegment(sketch, "E348", {"start": v(-1.2, 2.2) * mm, "end": v(-1.22, 2.34) * mm});
            skLineSegment(sketch, "E349", {"start": v(-1.22, 2.34) * mm, "end": v(-1.21, 2.47) * mm});
            skLineSegment(sketch, "E350", {"start": v(-1.21, 2.47) * mm, "end": v(-1.2, 2.56) * mm});
            skLineSegment(sketch, "E351", {"start": v(-1.2, 2.56) * mm, "end": v(-1.18, 2.67) * mm});
            skLineSegment(sketch, "E352", {"start": v(-1.18, 2.67) * mm, "end": v(-1.16, 2.76) * mm});
            skLineSegment(sketch, "E353", {"start": v(-1.16, 2.76) * mm, "end": v(-1.13, 2.83) * mm});
            skLineSegment(sketch, "E354", {"start": v(-1.13, 2.83) * mm, "end": v(-1.13, 2.87) * mm});
            skLineSegment(sketch, "E355", {"start": v(-1.13, 2.87) * mm, "end": v(-1.14, 2.92) * mm});
            skLineSegment(sketch, "E356", {"start": v(-1.14, 2.92) * mm, "end": v(-1.16, 3) * mm});
            skLineSegment(sketch, "E357", {"start": v(-1.16, 3) * mm, "end": v(-1.2, 3.08) * mm});
            skLineSegment(sketch, "E358", {"start": v(-1.2, 3.08) * mm, "end": v(-1.23, 3.14) * mm});
            skLineSegment(sketch, "E359", {"start": v(-1.23, 3.14) * mm, "end": v(-1.28, 3.22) * mm});
            skLineSegment(sketch, "E360", {"start": v(-1.28, 3.22) * mm, "end": v(-1.33, 3.3) * mm});
            skLineSegment(sketch, "E361", {"start": v(-1.33, 3.3) * mm, "end": v(-1.39, 3.38) * mm});
            skLineSegment(sketch, "E362", {"start": v(-1.39, 3.38) * mm, "end": v(-1.4, 3.4) * mm});
            skLineSegment(sketch, "E363", {"start": v(-1.4, 3.4) * mm, "end": v(-1.43, 3.43) * mm});
            skLineSegment(sketch, "E364", {"start": v(-1.43, 3.43) * mm, "end": v(-1.44, 3.46) * mm});
            skLineSegment(sketch, "E365", {"start": v(-1.44, 3.46) * mm, "end": v(-1.46, 3.48) * mm});
            skLineSegment(sketch, "E366", {"start": v(-1.46, 3.48) * mm, "end": v(-1.48, 3.53) * mm});
            skLineSegment(sketch, "E367", {"start": v(-1.48, 3.53) * mm, "end": v(-1.52, 3.57) * mm});
            skLineSegment(sketch, "E368", {"start": v(-1.52, 3.57) * mm, "end": v(-1.58, 3.64) * mm});
            skLineSegment(sketch, "E369", {"start": v(-1.58, 3.64) * mm, "end": v(-1.66, 3.72) * mm});
            skLineSegment(sketch, "E370", {"start": v(-1.66, 3.72) * mm, "end": v(-1.75, 3.8) * mm});
            skLineSegment(sketch, "E371", {"start": v(-1.75, 3.8) * mm, "end": v(-1.82, 3.85) * mm});
            skLineSegment(sketch, "E372", {"start": v(-1.82, 3.85) * mm, "end": v(-1.98, 3.95) * mm});
            skLineSegment(sketch, "E373", {"start": v(-1.98, 3.95) * mm, "end": v(-2.1, 4.02) * mm});
            skLineSegment(sketch, "E374", {"start": v(-2.1, 4.02) * mm, "end": v(-2.2, 4.06) * mm});
            skLineSegment(sketch, "E375", {"start": v(-2.2, 4.06) * mm, "end": v(-2.32, 4.1) * mm});
            skLineSegment(sketch, "E376", {"start": v(-2.32, 4.1) * mm, "end": v(-2.36, 4.11) * mm});
            skLineSegment(sketch, "E377", {"start": v(-2.36, 4.11) * mm, "end": v(-2.41, 4.13) * mm});
            skLineSegment(sketch, "E378", {"start": v(-2.41, 4.13) * mm, "end": v(-2.45, 4.14) * mm});
            skLineSegment(sketch, "E379", {"start": v(-2.45, 4.14) * mm, "end": v(-2.48, 4.15) * mm});
            skLineSegment(sketch, "E380", {"start": v(-2.48, 4.15) * mm, "end": v(-2.54, 4.17) * mm});
            skLineSegment(sketch, "E381", {"start": v(-2.54, 4.17) * mm, "end": v(-2.62, 4.19) * mm});
            skLineSegment(sketch, "E382", {"start": v(-2.62, 4.19) * mm, "end": v(-2.72, 4.2) * mm});
            skLineSegment(sketch, "E383", {"start": v(-2.72, 4.2) * mm, "end": v(-2.84, 4.22) * mm});
            skLineSegment(sketch, "E384", {"start": v(-2.84, 4.22) * mm, "end": v(-2.92, 4.22) * mm});
            skLineSegment(sketch, "E385", {"start": v(-2.92, 4.22) * mm, "end": v(-3.02, 4.2) * mm});
            skLineSegment(sketch, "E386", {"start": v(-3.02, 4.2) * mm, "end": v(-3.08, 4.2) * mm});
            skLineSegment(sketch, "E387", {"start": v(-3.08, 4.2) * mm, "end": v(-3.12, 4.19) * mm});
            skLineSegment(sketch, "E388", {"start": v(-3.12, 4.19) * mm, "end": v(-3.15, 4.18) * mm});
            skLineSegment(sketch, "E389", {"start": v(-3.15, 4.18) * mm, "end": v(-3.17, 4.18) * mm});
            skLineSegment(sketch, "E390", {"start": v(-3.17, 4.18) * mm, "end": v(-3.18, 4.18) * mm});
            skLineSegment(sketch, "E391", {"start": v(-3.18, 4.18) * mm, "end": v(-3.19, 4.17) * mm});
            skLineSegment(sketch, "E392", {"start": v(-3.19, 4.17) * mm, "end": v(-3.19, 4.17) * mm});
            skLineSegment(sketch, "E393", {"start": v(-3.19, 4.17) * mm, "end": v(-3.19, 4.16) * mm});
            skLineSegment(sketch, "E394", {"start": v(-3.19, 4.16) * mm, "end": v(-3.2, 4.15) * mm});
            skLineSegment(sketch, "E395", {"start": v(-3.2, 4.15) * mm, "end": v(-3.22, 4.14) * mm});
            skLineSegment(sketch, "E396", {"start": v(-3.22, 4.14) * mm, "end": v(-3.23, 4.13) * mm});
            skLineSegment(sketch, "E397", {"start": v(-3.23, 4.13) * mm, "end": v(-3.26, 4.12) * mm});
            skLineSegment(sketch, "E398", {"start": v(-3.26, 4.12) * mm, "end": v(-3.28, 4.1) * mm});
            skLineSegment(sketch, "E399", {"start": v(-3.28, 4.1) * mm, "end": v(-3.3, 4.08) * mm});
            skLineSegment(sketch, "E400", {"start": v(-3.3, 4.08) * mm, "end": v(-3.32, 4.06) * mm});
            skLineSegment(sketch, "E401", {"start": v(-3.32, 4.06) * mm, "end": v(-3.34, 4.03) * mm});
            skLineSegment(sketch, "E402", {"start": v(-3.34, 4.03) * mm, "end": v(-3.36, 4) * mm});
            skLineSegment(sketch, "E403", {"start": v(-3.36, 4) * mm, "end": v(-3.37, 3.96) * mm});
            skLineSegment(sketch, "E404", {"start": v(-3.37, 3.96) * mm, "end": v(-3.38, 3.93) * mm});
            skLineSegment(sketch, "E405", {"start": v(-3.38, 3.93) * mm, "end": v(-3.38, 3.9) * mm});
            skLineSegment(sketch, "E406", {"start": v(-3.38, 3.9) * mm, "end": v(-3.39, 3.87) * mm});
            skLineSegment(sketch, "E407", {"start": v(-3.39, 3.87) * mm, "end": v(-3.39, 3.85) * mm});
            skLineSegment(sketch, "E408", {"start": v(-3.39, 3.85) * mm, "end": v(-3.4, 3.83) * mm});
            skLineSegment(sketch, "E409", {"start": v(-3.4, 3.83) * mm, "end": v(-3.4, 3.81) * mm});
            skLineSegment(sketch, "E410", {"start": v(-3.4, 3.81) * mm, "end": v(-3.42, 3.8) * mm});
            skLineSegment(sketch, "E411", {"start": v(-3.42, 3.8) * mm, "end": v(-3.45, 3.8) * mm});
            skLineSegment(sketch, "E412", {"start": v(-3.45, 3.8) * mm, "end": v(-3.47, 3.8) * mm});
            skLineSegment(sketch, "E413", {"start": v(-3.47, 3.8) * mm, "end": v(-3.5, 3.83) * mm});
            skLineSegment(sketch, "E414", {"start": v(-3.5, 3.83) * mm, "end": v(-3.53, 3.86) * mm});
            skLineSegment(sketch, "E415", {"start": v(-3.53, 3.86) * mm, "end": v(-3.54, 3.9) * mm});
            skLineSegment(sketch, "E416", {"start": v(-3.54, 3.9) * mm, "end": v(-3.55, 3.92) * mm});
            skLineSegment(sketch, "E417", {"start": v(-3.55, 3.92) * mm, "end": v(-3.56, 3.93) * mm});
            skLineSegment(sketch, "E418", {"start": v(-3.56, 3.93) * mm, "end": v(-3.56, 3.94) * mm});
            skLineSegment(sketch, "E419", {"start": v(-3.56, 3.94) * mm, "end": v(-3.57, 3.96) * mm});
            skLineSegment(sketch, "E420", {"start": v(-3.57, 3.96) * mm, "end": v(-3.58, 3.98) * mm});
            skLineSegment(sketch, "E421", {"start": v(-3.58, 3.98) * mm, "end": v(-3.58, 4.01) * mm});
            skLineSegment(sketch, "E422", {"start": v(-3.58, 4.01) * mm, "end": v(-3.58, 4.05) * mm});
            skLineSegment(sketch, "E423", {"start": v(-3.58, 4.05) * mm, "end": v(-3.59, 4.08) * mm});
            skLineSegment(sketch, "E424", {"start": v(-3.59, 4.08) * mm, "end": v(-3.59, 4.1) * mm});
            skLineSegment(sketch, "E425", {"start": v(-3.59, 4.1) * mm, "end": v(-3.59, 4.13) * mm});
            skLineSegment(sketch, "E426", {"start": v(-3.59, 4.13) * mm, "end": v(-3.58, 4.16) * mm});
            skLineSegment(sketch, "E427", {"start": v(-3.58, 4.16) * mm, "end": v(-3.56, 4.2) * mm});
            skLineSegment(sketch, "E428", {"start": v(-3.56, 4.2) * mm, "end": v(-3.55, 4.24) * mm});
            skLineSegment(sketch, "E429", {"start": v(-3.55, 4.24) * mm, "end": v(-3.52, 4.29) * mm});
            skLineSegment(sketch, "E430", {"start": v(-3.52, 4.29) * mm, "end": v(-3.5, 4.35) * mm});
            skLineSegment(sketch, "E431", {"start": v(-3.5, 4.35) * mm, "end": v(-3.47, 4.4) * mm});
            skLineSegment(sketch, "E432", {"start": v(-3.47, 4.4) * mm, "end": v(-3.44, 4.43) * mm});
            skLineSegment(sketch, "E433", {"start": v(-3.44, 4.43) * mm, "end": v(-3.41, 4.46) * mm});
            skLineSegment(sketch, "E434", {"start": v(-3.41, 4.46) * mm, "end": v(-3.36, 4.5) * mm});
            skLineSegment(sketch, "E435", {"start": v(-3.36, 4.5) * mm, "end": v(-3.32, 4.53) * mm});
            skLineSegment(sketch, "E436", {"start": v(-3.32, 4.53) * mm, "end": v(-3.26, 4.55) * mm});
            skLineSegment(sketch, "E437", {"start": v(-3.26, 4.55) * mm, "end": v(-3.18, 4.58) * mm});
            skLineSegment(sketch, "E438", {"start": v(-3.18, 4.58) * mm, "end": v(-3.12, 4.6) * mm});
            skLineSegment(sketch, "E439", {"start": v(-3.12, 4.6) * mm, "end": v(-3.08, 4.6) * mm});
            skLineSegment(sketch, "E440", {"start": v(-3.08, 4.6) * mm, "end": v(-3.03, 4.6) * mm});
            skLineSegment(sketch, "E441", {"start": v(-3.03, 4.6) * mm, "end": v(-2.96, 4.6) * mm});
            skLineSegment(sketch, "E442", {"start": v(-2.96, 4.6) * mm, "end": v(-2.82, 4.58) * mm});
            skLineSegment(sketch, "E443", {"start": v(-2.82, 4.58) * mm, "end": v(-2.69, 4.56) * mm});
            skLineSegment(sketch, "E444", {"start": v(-2.69, 4.56) * mm, "end": v(-2.55, 4.53) * mm});
            skLineSegment(sketch, "E445", {"start": v(-2.55, 4.53) * mm, "end": v(-2.39, 4.47) * mm});
            skLineSegment(sketch, "E446", {"start": v(-2.39, 4.47) * mm, "end": v(-2.26, 4.43) * mm});
            skLineSegment(sketch, "E447", {"start": v(-2.26, 4.43) * mm, "end": v(-2.16, 4.4) * mm});
            skLineSegment(sketch, "E448", {"start": v(-2.16, 4.4) * mm, "end": v(-2.07, 4.36) * mm});
            skLineSegment(sketch, "E449", {"start": v(-2.07, 4.36) * mm, "end": v(-1.98, 4.31) * mm});
            skLineSegment(sketch, "E450", {"start": v(-1.98, 4.31) * mm, "end": v(-1.74, 4.17) * mm});
            skLineSegment(sketch, "E451", {"start": v(-1.74, 4.17) * mm, "end": v(-1.53, 4.03) * mm});
            skLineSegment(sketch, "E452", {"start": v(-1.53, 4.03) * mm, "end": v(-1.35, 3.87) * mm});
            skLineSegment(sketch, "E453", {"start": v(-1.35, 3.87) * mm, "end": v(-1.2, 3.7) * mm});
            skLineSegment(sketch, "E454", {"start": v(-1.2, 3.7) * mm, "end": v(-1.1, 3.6) * mm});
            skLineSegment(sketch, "E455", {"start": v(-1.1, 3.6) * mm, "end": v(-1.03, 3.48) * mm});
            skLineSegment(sketch, "E456", {"start": v(-1.03, 3.48) * mm, "end": v(-0.96, 3.38) * mm});
            skLineSegment(sketch, "E457", {"start": v(-0.96, 3.38) * mm, "end": v(-0.9, 3.3) * mm});
            skLineSegment(sketch, "E458", {"start": v(-0.9, 3.3) * mm, "end": v(-0.86, 3.22) * mm});
            skLineSegment(sketch, "E459", {"start": v(-0.86, 3.22) * mm, "end": v(-0.82, 3.27) * mm});
            skLineSegment(sketch, "E460", {"start": v(-0.82, 3.27) * mm, "end": v(-0.8, 3.29) * mm});
            skLineSegment(sketch, "E461", {"start": v(-0.8, 3.29) * mm, "end": v(-0.77, 3.31) * mm});
            skLineSegment(sketch, "E462", {"start": v(-0.77, 3.31) * mm, "end": v(-0.73, 3.34) * mm});
            skLineSegment(sketch, "E463", {"start": v(-0.73, 3.34) * mm, "end": v(-0.7, 3.36) * mm});
            skLineSegment(sketch, "E464", {"start": v(-0.7, 3.36) * mm, "end": v(-0.67, 3.39) * mm});
            skLineSegment(sketch, "E465", {"start": v(-0.67, 3.39) * mm, "end": v(-0.64, 3.4) * mm});
            skLineSegment(sketch, "E466", {"start": v(-0.64, 3.4) * mm, "end": v(-0.61, 3.42) * mm});
            skLineSegment(sketch, "E467", {"start": v(-0.61, 3.42) * mm, "end": v(-0.6, 3.43) * mm});
            skLineSegment(sketch, "E468", {"start": v(-0.6, 3.43) * mm, "end": v(-0.52, 3.46) * mm});
            skLineSegment(sketch, "E469", {"start": v(-0.52, 3.46) * mm, "end": v(-0.43, 3.48) * mm});
            skLineSegment(sketch, "E470", {"start": v(-0.43, 3.48) * mm, "end": v(-0.34, 3.5) * mm});
            skLineSegment(sketch, "E471", {"start": v(-0.34, 3.5) * mm, "end": v(-0.25, 3.5) * mm});
            skLineSegment(sketch, "E472", {"start": v(-0.25, 3.5) * mm, "end": v(-0.2, 3.5) * mm});
            skLineSegment(sketch, "E473", {"start": v(-0.2, 3.5) * mm, "end": v(-0.14, 3.5) * mm});
            skLineSegment(sketch, "E474", {"start": v(-0.14, 3.5) * mm, "end": v(-0.1, 3.5) * mm});
            skLineSegment(sketch, "E475", {"start": v(-0.1, 3.5) * mm, "end": v(-0.04, 3.49) * mm});
            skLineSegment(sketch, "E476", {"start": v(-0.04, 3.49) * mm, "end": v(0, 3.48) * mm});
            skLineSegment(sketch, "E477", {"start": v(0, 3.48) * mm, "end": v(0.05, 3.46) * mm});
            skLineSegment(sketch, "E478", {"start": v(0.05, 3.46) * mm, "end": v(0.1, 3.45) * mm});
            skLineSegment(sketch, "E479", {"start": v(0.1, 3.45) * mm, "end": v(0.12, 3.43) * mm});
            skLineSegment(sketch, "E480", {"start": v(0.12, 3.43) * mm, "end": v(0.19, 3.4) * mm});
            skLineSegment(sketch, "E481", {"start": v(0.19, 3.4) * mm, "end": v(0.24, 3.54) * mm});
            skLineSegment(sketch, "E482", {"start": v(0.24, 3.54) * mm, "end": v(0.27, 3.6) * mm});
            skLineSegment(sketch, "E483", {"start": v(0.27, 3.6) * mm, "end": v(0.3, 3.7) * mm});
            skLineSegment(sketch, "E484", {"start": v(0.3, 3.7) * mm, "end": v(0.35, 3.78) * mm});
            skLineSegment(sketch, "E485", {"start": v(0.35, 3.78) * mm, "end": v(0.39, 3.86) * mm});
            skLineSegment(sketch, "E486", {"start": v(0.39, 3.86) * mm, "end": v(0.43, 3.95) * mm});
            skLineSegment(sketch, "E487", {"start": v(0.43, 3.95) * mm, "end": v(0.48, 4.05) * mm});
            skLineSegment(sketch, "E488", {"start": v(0.48, 4.05) * mm, "end": v(0.53, 4.14) * mm});
            skLineSegment(sketch, "E489", {"start": v(0.53, 4.14) * mm, "end": v(0.57, 4.23) * mm});
            skLineSegment(sketch, "E490", {"start": v(0.57, 4.23) * mm, "end": v(0.68, 4.44) * mm});
            skLineSegment(sketch, "E491", {"start": v(0.68, 4.44) * mm, "end": v(0.8, 4.62) * mm});
            skLineSegment(sketch, "E492", {"start": v(0.8, 4.62) * mm, "end": v(0.9, 4.78) * mm});
            skLineSegment(sketch, "E493", {"start": v(0.9, 4.78) * mm, "end": v(1.01, 4.93) * mm});
            skLineSegment(sketch, "E494", {"start": v(1.01, 4.93) * mm, "end": v(1.04, 4.96) * mm});
            skLineSegment(sketch, "E495", {"start": v(1.04, 4.96) * mm, "end": v(1.08, 5) * mm});
            skLineSegment(sketch, "E496", {"start": v(1.08, 5) * mm, "end": v(1.12, 5.05) * mm});
            skLineSegment(sketch, "E497", {"start": v(1.12, 5.05) * mm, "end": v(1.16, 5.1) * mm});
            skLineSegment(sketch, "E498", {"start": v(1.16, 5.1) * mm, "end": v(1.21, 5.16) * mm});
            skLineSegment(sketch, "E499", {"start": v(1.21, 5.16) * mm, "end": v(1.28, 5.23) * mm});
            skLineSegment(sketch, "E500", {"start": v(1.28, 5.23) * mm, "end": v(1.35, 5.3) * mm});
            skLineSegment(sketch, "E501", {"start": v(1.35, 5.3) * mm, "end": v(1.42, 5.39) * mm});
            skLineSegment(sketch, "E502", {"start": v(1.42, 5.39) * mm, "end": v(1.5, 5.46) * mm});
            skLineSegment(sketch, "E503", {"start": v(1.5, 5.46) * mm, "end": v(1.57, 5.53) * mm});
            skLineSegment(sketch, "E504", {"start": v(1.57, 5.53) * mm, "end": v(1.63, 5.58) * mm});
            skLineSegment(sketch, "E505", {"start": v(1.63, 5.58) * mm, "end": v(1.67, 5.62) * mm});
            skLineSegment(sketch, "E506", {"start": v(1.67, 5.62) * mm, "end": v(1.77, 5.68) * mm});
            skLineSegment(sketch, "E507", {"start": v(1.77, 5.68) * mm, "end": v(1.88, 5.75) * mm});
            skLineSegment(sketch, "E508", {"start": v(1.88, 5.75) * mm, "end": v(2, 5.8) * mm});
            skLineSegment(sketch, "E509", {"start": v(2, 5.8) * mm, "end": v(2.09, 5.84) * mm});
            skLineSegment(sketch, "E510", {"start": v(2.09, 5.84) * mm, "end": v(2.15, 5.86) * mm});
            skLineSegment(sketch, "E511", {"start": v(2.15, 5.86) * mm, "end": v(2.22, 5.86) * mm});
            skLineSegment(sketch, "E512", {"start": v(2.22, 5.86) * mm, "end": v(2.33, 5.85) * mm});
            skLineSegment(sketch, "E513", {"start": v(2.33, 5.85) * mm, "end": v(2.45, 5.8) * mm});
            skLineSegment(sketch, "E514", {"start": v(2.45, 5.8) * mm, "end": v(2.57, 5.72) * mm});
            skLineSegment(sketch, "E515", {"start": v(2.57, 5.72) * mm, "end": v(2.66, 5.63) * mm});
            skLineSegment(sketch, "E516", {"start": v(2.66, 5.63) * mm, "end": v(2.7, 5.57) * mm});
            skLineSegment(sketch, "E517", {"start": v(2.7, 5.57) * mm, "end": v(2.71, 5.48) * mm});
            skLineSegment(sketch, "E518", {"start": v(2.71, 5.48) * mm, "end": v(2.7, 5.4) * mm});
            skLineSegment(sketch, "E519", {"start": v(2.7, 5.4) * mm, "end": v(2.7, 5.35) * mm});
            skLineSegment(sketch, "E520", {"start": v(2.7, 5.35) * mm, "end": v(2.67, 5.3) * mm});
            skLineSegment(sketch, "E521", {"start": v(2.67, 5.3) * mm, "end": v(2.62, 5.25) * mm});
            skLineSegment(sketch, "E522", {"start": v(2.62, 5.25) * mm, "end": v(2.58, 5.21) * mm});
            skLineSegment(sketch, "E523", {"start": v(2.58, 5.21) * mm, "end": v(2.55, 5.2) * mm});
            skLineSegment(sketch, "E524", {"start": v(2.55, 5.2) * mm, "end": v(2.53, 5.22) * mm});
            skLineSegment(sketch, "E525", {"start": v(2.53, 5.22) * mm, "end": v(2.53, 5.26) * mm});
            skLineSegment(sketch, "E526", {"start": v(2.53, 5.26) * mm, "end": v(2.53, 5.31) * mm});
            skLineSegment(sketch, "E527", {"start": v(2.53, 5.31) * mm, "end": v(2.52, 5.36) * mm});
            skLineSegment(sketch, "E528", {"start": v(2.52, 5.36) * mm, "end": v(2.48, 5.42) * mm});
            skLineSegment(sketch, "E529", {"start": v(2.48, 5.42) * mm, "end": v(2.43, 5.46) * mm});
            skLineSegment(sketch, "E530", {"start": v(2.43, 5.46) * mm, "end": v(2.37, 5.5) * mm});
            skLineSegment(sketch, "E531", {"start": v(2.37, 5.5) * mm, "end": v(2.3, 5.5) * mm});
            skLineSegment(sketch, "E532", {"start": v(2.3, 5.5) * mm, "end": v(2.26, 5.5) * mm});
            skLineSegment(sketch, "E533", {"start": v(2.26, 5.5) * mm, "end": v(2.2, 5.48) * mm});
            skLineSegment(sketch, "E534", {"start": v(2.2, 5.48) * mm, "end": v(2.1, 5.45) * mm});
            skLineSegment(sketch, "E535", {"start": v(2.1, 5.45) * mm, "end": v(2.01, 5.41) * mm});
            skLineSegment(sketch, "E536", {"start": v(2.01, 5.41) * mm, "end": v(1.87, 5.34) * mm});
            skLineSegment(sketch, "E537", {"start": v(1.87, 5.34) * mm, "end": v(1.73, 5.23) * mm});
            skLineSegment(sketch, "E538", {"start": v(1.73, 5.23) * mm, "end": v(1.58, 5.08) * mm});
            skLineSegment(sketch, "E539", {"start": v(1.58, 5.08) * mm, "end": v(1.4, 4.87) * mm});
            skLineSegment(sketch, "E540", {"start": v(1.4, 4.87) * mm, "end": v(1.36, 4.83) * mm});
            skLineSegment(sketch, "E541", {"start": v(1.36, 4.83) * mm, "end": v(1.32, 4.8) * mm});
            skLineSegment(sketch, "E542", {"start": v(1.32, 4.8) * mm, "end": v(1.3, 4.76) * mm});
            skLineSegment(sketch, "E543", {"start": v(1.3, 4.76) * mm, "end": v(1.28, 4.75) * mm});
            skLineSegment(sketch, "E544", {"start": v(1.28, 4.75) * mm, "end": v(1.26, 4.72) * mm});
            skLineSegment(sketch, "E545", {"start": v(1.26, 4.72) * mm, "end": v(1.23, 4.68) * mm});
            skLineSegment(sketch, "E546", {"start": v(1.23, 4.68) * mm, "end": v(1.21, 4.66) * mm});
            skLineSegment(sketch, "E547", {"start": v(1.21, 4.66) * mm, "end": v(1.19, 4.63) * mm});
            skLineSegment(sketch, "E548", {"start": v(1.19, 4.63) * mm, "end": v(1.16, 4.59) * mm});
            skLineSegment(sketch, "E549", {"start": v(1.16, 4.59) * mm, "end": v(1.13, 4.54) * mm});
            skLineSegment(sketch, "E550", {"start": v(1.13, 4.54) * mm, "end": v(1.1, 4.5) * mm});
            skLineSegment(sketch, "E551", {"start": v(1.1, 4.5) * mm, "end": v(1.06, 4.44) * mm});
            skLineSegment(sketch, "E552", {"start": v(1.06, 4.44) * mm, "end": v(1.02, 4.4) * mm});
            skLineSegment(sketch, "E553", {"start": v(1.02, 4.4) * mm, "end": v(1, 4.35) * mm});
            skLineSegment(sketch, "E554", {"start": v(1, 4.35) * mm, "end": v(0.98, 4.31) * mm});
            skLineSegment(sketch, "E555", {"start": v(0.98, 4.31) * mm, "end": v(0.95, 4.27) * mm});
            skLineSegment(sketch, "E556", {"start": v(0.95, 4.27) * mm, "end": v(0.92, 4.22) * mm});
            skLineSegment(sketch, "E557", {"start": v(0.92, 4.22) * mm, "end": v(0.9, 4.18) * mm});
            skLineSegment(sketch, "E558", {"start": v(0.9, 4.18) * mm, "end": v(0.83, 4.07) * mm});
            skLineSegment(sketch, "E559", {"start": v(0.83, 4.07) * mm, "end": v(0.79, 3.98) * mm});
            skLineSegment(sketch, "E560", {"start": v(0.79, 3.98) * mm, "end": v(0.75, 3.9) * mm});
            skLineSegment(sketch, "E561", {"start": v(0.75, 3.9) * mm, "end": v(0.72, 3.81) * mm});
            skLineSegment(sketch, "E562", {"start": v(0.72, 3.81) * mm, "end": v(0.7, 3.76) * mm});
            skLineSegment(sketch, "E563", {"start": v(0.7, 3.76) * mm, "end": v(0.68, 3.71) * mm});
            skLineSegment(sketch, "E564", {"start": v(0.68, 3.71) * mm, "end": v(0.66, 3.66) * mm});
            skLineSegment(sketch, "E565", {"start": v(0.66, 3.66) * mm, "end": v(0.64, 3.62) * mm});
            skLineSegment(sketch, "E566", {"start": v(0.64, 3.62) * mm, "end": v(0.63, 3.57) * mm});
            skLineSegment(sketch, "E567", {"start": v(0.63, 3.57) * mm, "end": v(0.6, 3.5) * mm});
            skLineSegment(sketch, "E568", {"start": v(0.6, 3.5) * mm, "end": v(0.58, 3.43) * mm});
            skLineSegment(sketch, "E569", {"start": v(0.58, 3.43) * mm, "end": v(0.56, 3.35) * mm});
            skLineSegment(sketch, "E570", {"start": v(0.56, 3.35) * mm, "end": v(0.5, 3.16) * mm});
            skLineSegment(sketch, "E571", {"start": v(0.5, 3.16) * mm, "end": v(0.53, 3.12) * mm});
            skLineSegment(sketch, "E572", {"start": v(0.53, 3.12) * mm, "end": v(0.56, 3.02) * mm});
            skLineSegment(sketch, "E573", {"start": v(0.56, 3.02) * mm, "end": v(0.6, 2.86) * mm});
            skLineSegment(sketch, "E574", {"start": v(0.6, 2.86) * mm, "end": v(0.6, 2.68) * mm});
            skLineSegment(sketch, "E575", {"start": v(0.6, 2.68) * mm, "end": v(0.61, 2.5) * mm});
            skLineSegment(sketch, "E576", {"start": v(0.61, 2.5) * mm, "end": v(0.6, 2.4) * mm});
            skLineSegment(sketch, "E577", {"start": v(0.6, 2.4) * mm, "end": v(0.59, 2.3) * mm});
            skLineSegment(sketch, "E578", {"start": v(0.59, 2.3) * mm, "end": v(0.56, 2.18) * mm});
            skLineSegment(sketch, "E579", {"start": v(0.56, 2.18) * mm, "end": v(0.52, 2.07) * mm});
            skLineSegment(sketch, "E580", {"start": v(0.52, 2.07) * mm, "end": v(0.5, 2.01) * mm});
            skLineSegment(sketch, "E581", {"start": v(0.5, 2.01) * mm, "end": v(0.45, 1.93) * mm});
            skLineSegment(sketch, "E582", {"start": v(0.45, 1.93) * mm, "end": v(0.4, 1.86) * mm});
            skLineSegment(sketch, "E583", {"start": v(0.4, 1.86) * mm, "end": v(0.37, 1.8) * mm});
            skLineSegment(sketch, "E584", {"start": v(0.37, 1.8) * mm, "end": v(0.36, 1.78) * mm});
            skLineSegment(sketch, "E585", {"start": v(0.36, 1.78) * mm, "end": v(0.35, 1.77) * mm});
            skLineSegment(sketch, "E586", {"start": v(0.35, 1.77) * mm, "end": v(0.35, 1.76) * mm});
            skLineSegment(sketch, "E587", {"start": v(0.35, 1.76) * mm, "end": v(0.36, 1.75) * mm});
            skLineSegment(sketch, "E588", {"start": v(0.36, 1.75) * mm, "end": v(0.38, 1.7) * mm});
            skLineSegment(sketch, "E589", {"start": v(0.38, 1.7) * mm, "end": v(0.41, 1.61) * mm});
            skLineSegment(sketch, "E590", {"start": v(0.41, 1.61) * mm, "end": v(0.45, 1.5) * mm});
            skLineSegment(sketch, "E591", {"start": v(0.45, 1.5) * mm, "end": v(0.48, 1.38) * mm});
            skLineSegment(sketch, "E592", {"start": v(0.48, 1.38) * mm, "end": v(0.49, 1.34) * mm});
            skLineSegment(sketch, "E593", {"start": v(0.49, 1.34) * mm, "end": v(0.5, 1.3) * mm});
            skLineSegment(sketch, "E594", {"start": v(0.5, 1.3) * mm, "end": v(0.5, 1.28) * mm});
            skLineSegment(sketch, "E595", {"start": v(0.5, 1.28) * mm, "end": v(0.5, 1.28) * mm});
            skLineSegment(sketch, "E596", {"start": v(0.5, 1.28) * mm, "end": v(0.52, 1.29) * mm});
            skLineSegment(sketch, "E597", {"start": v(0.52, 1.29) * mm, "end": v(0.54, 1.32) * mm});
            skLineSegment(sketch, "E598", {"start": v(0.54, 1.32) * mm, "end": v(0.58, 1.36) * mm});
            skLineSegment(sketch, "E599", {"start": v(0.58, 1.36) * mm, "end": v(0.62, 1.42) * mm});
            skLineSegment(sketch, "E600", {"start": v(0.62, 1.42) * mm, "end": v(0.75, 1.58) * mm});
            skLineSegment(sketch, "E601", {"start": v(0.75, 1.58) * mm, "end": v(0.92, 1.76) * mm});
            skLineSegment(sketch, "E602", {"start": v(0.92, 1.76) * mm, "end": v(1.11, 1.93) * mm});
            skLineSegment(sketch, "E603", {"start": v(1.11, 1.93) * mm, "end": v(1.3, 2.08) * mm});
            skLineSegment(sketch, "E604", {"start": v(1.3, 2.08) * mm, "end": v(1.65, 2.31) * mm});
            skLineSegment(sketch, "E605", {"start": v(1.65, 2.31) * mm, "end": v(1.97, 2.49) * mm});
            skLineSegment(sketch, "E606", {"start": v(1.97, 2.49) * mm, "end": v(2.27, 2.61) * mm});
            skLineSegment(sketch, "E607", {"start": v(2.27, 2.61) * mm, "end": v(2.55, 2.69) * mm});
            skLineSegment(sketch, "E608", {"start": v(2.55, 2.69) * mm, "end": v(2.69, 2.71) * mm});
            skLineSegment(sketch, "E609", {"start": v(2.69, 2.71) * mm, "end": v(2.83, 2.74) * mm});
            skLineSegment(sketch, "E610", {"start": v(2.83, 2.74) * mm, "end": v(2.9, 2.75) * mm});
            skLineSegment(sketch, "E611", {"start": v(2.9, 2.75) * mm, "end": v(2.99, 2.76) * mm});
            skLineSegment(sketch, "E612", {"start": v(2.99, 2.76) * mm, "end": v(3.08, 2.77) * mm});
            skLineSegment(sketch, "E613", {"start": v(3.08, 2.77) * mm, "end": v(3.18, 2.78) * mm});
            skLineSegment(sketch, "E614", {"start": v(3.18, 2.78) * mm, "end": v(3.28, 2.79) * mm});
            skLineSegment(sketch, "E615", {"start": v(3.28, 2.79) * mm, "end": v(3.36, 2.8) * mm});
            skLineSegment(sketch, "E616", {"start": v(3.36, 2.8) * mm, "end": v(3.42, 2.8) * mm});
            skLineSegment(sketch, "E617", {"start": v(3.42, 2.8) * mm, "end": v(3.45, 2.8) * mm});
            skLineSegment(sketch, "E618", {"start": v(3.45, 2.8) * mm, "end": v(3.47, 2.79) * mm});
            skLineSegment(sketch, "E619", {"start": v(3.47, 2.79) * mm, "end": v(3.5, 2.79) * mm});
            skLineSegment(sketch, "E620", {"start": v(3.5, 2.79) * mm, "end": v(3.56, 2.78) * mm});
            skLineSegment(sketch, "E621", {"start": v(3.56, 2.78) * mm, "end": v(3.62, 2.78) * mm});
            skLineSegment(sketch, "E622", {"start": v(3.62, 2.78) * mm, "end": v(3.75, 2.76) * mm});
            skLineSegment(sketch, "E623", {"start": v(3.75, 2.76) * mm, "end": v(3.88, 2.75) * mm});
            skLineSegment(sketch, "E624", {"start": v(3.88, 2.75) * mm, "end": v(3.98, 2.73) * mm});
            skLineSegment(sketch, "E625", {"start": v(3.98, 2.73) * mm, "end": v(4.05, 2.72) * mm});
            skLineSegment(sketch, "E626", {"start": v(4.05, 2.72) * mm, "end": v(4.09, 2.7) * mm});
            skLineSegment(sketch, "E627", {"start": v(4.09, 2.7) * mm, "end": v(4.13, 2.7) * mm});
            skLineSegment(sketch, "E628", {"start": v(4.13, 2.7) * mm, "end": v(4.18, 2.7) * mm});
            skLineSegment(sketch, "E629", {"start": v(4.18, 2.7) * mm, "end": v(4.22, 2.69) * mm});
            skLineSegment(sketch, "E630", {"start": v(4.22, 2.69) * mm, "end": v(4.34, 2.67) * mm});
            skLineSegment(sketch, "E631", {"start": v(4.34, 2.67) * mm, "end": v(4.47, 2.64) * mm});
            skLineSegment(sketch, "E632", {"start": v(4.47, 2.64) * mm, "end": v(4.61, 2.6) * mm});
            skLineSegment(sketch, "E633", {"start": v(4.61, 2.6) * mm, "end": v(4.77, 2.59) * mm});
            skLineSegment(sketch, "E634", {"start": v(4.77, 2.59) * mm, "end": v(4.95, 2.58) * mm});
            skLineSegment(sketch, "E635", {"start": v(4.95, 2.58) * mm, "end": v(5.18, 2.57) * mm});
            skLineSegment(sketch, "E636", {"start": v(5.18, 2.57) * mm, "end": v(5.34, 2.57) * mm});
            skLineSegment(sketch, "E637", {"start": v(5.34, 2.57) * mm, "end": v(5.43, 2.57) * mm});
            skLineSegment(sketch, "E638", {"start": v(5.43, 2.57) * mm, "end": v(5.5, 2.58) * mm});
            skLineSegment(sketch, "E639", {"start": v(5.5, 2.58) * mm, "end": v(5.55, 2.6) * mm});
            skLineSegment(sketch, "E640", {"start": v(5.55, 2.6) * mm, "end": v(5.67, 2.63) * mm});
            skLineSegment(sketch, "E641", {"start": v(5.67, 2.63) * mm, "end": v(5.8, 2.67) * mm});
            skLineSegment(sketch, "E642", {"start": v(5.8, 2.67) * mm, "end": v(5.95, 2.72) * mm});
            skLineSegment(sketch, "E643", {"start": v(5.95, 2.72) * mm, "end": v(6.1, 2.78) * mm});
            skLineSegment(sketch, "E644", {"start": v(6.1, 2.78) * mm, "end": v(6.17, 2.8) * mm});
            skLineSegment(sketch, "E645", {"start": v(6.17, 2.8) * mm, "end": v(6.23, 2.83) * mm});
            skLineSegment(sketch, "E646", {"start": v(6.23, 2.83) * mm, "end": v(6.27, 2.84) * mm});
            skLineSegment(sketch, "E647", {"start": v(6.27, 2.84) * mm, "end": v(6.3, 2.85) * mm});
            skLineSegment(sketch, "E648", {"start": v(6.3, 2.85) * mm, "end": v(6.33, 2.86) * mm});
            skLineSegment(sketch, "E649", {"start": v(6.33, 2.86) * mm, "end": v(6.38, 2.88) * mm});
            skLineSegment(sketch, "E650", {"start": v(6.38, 2.88) * mm, "end": v(6.43, 2.9) * mm});
            skLineSegment(sketch, "E651", {"start": v(6.43, 2.9) * mm, "end": v(6.49, 2.92) * mm});
            skLineSegment(sketch, "E652", {"start": v(6.49, 2.92) * mm, "end": v(6.59, 2.95) * mm});
            skLineSegment(sketch, "E653", {"start": v(6.59, 2.95) * mm, "end": v(6.7, 2.99) * mm});
            skLineSegment(sketch, "E654", {"start": v(6.7, 2.99) * mm, "end": v(6.82, 3.02) * mm});
            skLineSegment(sketch, "E655", {"start": v(6.82, 3.02) * mm, "end": v(6.94, 3.05) * mm});
            skLineSegment(sketch, "E656", {"start": v(6.94, 3.05) * mm, "end": v(7.05, 3.08) * mm});
            skLineSegment(sketch, "E657", {"start": v(7.05, 3.08) * mm, "end": v(7.16, 3.1) * mm});
            skLineSegment(sketch, "E658", {"start": v(7.16, 3.1) * mm, "end": v(7.26, 3.12) * mm});
            skLineSegment(sketch, "E659", {"start": v(7.26, 3.12) * mm, "end": v(7.34, 3.13) * mm});
            skLineSegment(sketch, "E660", {"start": v(7.34, 3.13) * mm, "end": v(7.45, 3.14) * mm});
            skLineSegment(sketch, "E661", {"start": v(7.45, 3.14) * mm, "end": v(7.57, 3.14) * mm});
            skLineSegment(sketch, "E662", {"start": v(7.57, 3.14) * mm, "end": v(7.69, 3.14) * mm});
            skLineSegment(sketch, "E663", {"start": v(7.69, 3.14) * mm, "end": v(7.78, 3.13) * mm});
            skLineSegment(sketch, "E664", {"start": v(7.78, 3.13) * mm, "end": v(7.85, 3.11) * mm});
            skLineSegment(sketch, "E665", {"start": v(7.85, 3.11) * mm, "end": v(7.94, 3.09) * mm});
            skLineSegment(sketch, "E666", {"start": v(7.94, 3.09) * mm, "end": v(8.01, 3.06) * mm});
            skLineSegment(sketch, "E667", {"start": v(8.01, 3.06) * mm, "end": v(8.04, 3.03) * mm});
            skLineSegment(sketch, "E668", {"start": v(8.04, 3.03) * mm, "end": v(8.03, 2.98) * mm});
            skLineSegment(sketch, "E669", {"start": v(8.03, 2.98) * mm, "end": v(8, 2.88) * mm});
            skLineSegment(sketch, "E670", {"start": v(8, 2.88) * mm, "end": v(7.95, 2.76) * mm});
            skLineSegment(sketch, "E671", {"start": v(7.95, 2.76) * mm, "end": v(7.9, 2.66) * mm});
            skLineSegment(sketch, "E672", {"start": v(7.9, 2.66) * mm, "end": v(7.88, 2.6) * mm});
            skLineSegment(sketch, "E673", {"start": v(7.88, 2.6) * mm, "end": v(7.86, 2.57) * mm});
            skLineSegment(sketch, "E674", {"start": v(7.86, 2.57) * mm, "end": v(7.85, 2.54) * mm});
            skLineSegment(sketch, "E675", {"start": v(7.85, 2.54) * mm, "end": v(7.84, 2.53) * mm});
            skLineSegment(sketch, "E676", {"start": v(7.84, 2.53) * mm, "end": v(7.84, 2.51) * mm});
            skLineSegment(sketch, "E677", {"start": v(7.84, 2.51) * mm, "end": v(7.83, 2.48) * mm});
            skLineSegment(sketch, "E678", {"start": v(7.83, 2.48) * mm, "end": v(7.8, 2.44) * mm});
            skLineSegment(sketch, "E679", {"start": v(7.8, 2.44) * mm, "end": v(7.78, 2.39) * mm});
            skLineSegment(sketch, "E680", {"start": v(7.78, 2.39) * mm, "end": v(7.76, 2.33) * mm});
            skLineSegment(sketch, "E681", {"start": v(7.76, 2.33) * mm, "end": v(7.73, 2.28) * mm});
            skLineSegment(sketch, "E682", {"start": v(7.73, 2.28) * mm, "end": v(7.7, 2.22) * mm});
            skLineSegment(sketch, "E683", {"start": v(7.7, 2.22) * mm, "end": v(7.68, 2.18) * mm});
            skLineSegment(sketch, "E684", {"start": v(7.68, 2.18) * mm, "end": v(7.61, 2.05) * mm});
            skLineSegment(sketch, "E685", {"start": v(7.61, 2.05) * mm, "end": v(7.55, 1.94) * mm});
            skLineSegment(sketch, "E686", {"start": v(7.55, 1.94) * mm, "end": v(7.5, 1.86) * mm});
            skLineSegment(sketch, "E687", {"start": v(7.5, 1.86) * mm, "end": v(7.45, 1.78) * mm});
            skLineSegment(sketch, "E688", {"start": v(7.45, 1.78) * mm, "end": v(7.4, 1.68) * mm});
            skLineSegment(sketch, "E689", {"start": v(7.4, 1.68) * mm, "end": v(7.33, 1.58) * mm});
            skLineSegment(sketch, "E690", {"start": v(7.33, 1.58) * mm, "end": v(7.26, 1.49) * mm});
            skLineSegment(sketch, "E691", {"start": v(7.26, 1.49) * mm, "end": v(7.19, 1.4) * mm});
            skLineSegment(sketch, "E692", {"start": v(7.19, 1.4) * mm, "end": v(7.12, 1.31) * mm});
            skLineSegment(sketch, "E693", {"start": v(7.12, 1.31) * mm, "end": v(7.06, 1.24) * mm});
            skLineSegment(sketch, "E694", {"start": v(7.06, 1.24) * mm, "end": v(6.97, 1.15) * mm});
            skLineSegment(sketch, "E695", {"start": v(6.97, 1.15) * mm, "end": v(6.8, 1.03) * mm});
            skLineSegment(sketch, "E696", {"start": v(6.8, 1.03) * mm, "end": v(6.7, 0.96) * mm});
            skLineSegment(sketch, "E697", {"start": v(6.7, 0.96) * mm, "end": v(6.62, 0.9) * mm});
            skLineSegment(sketch, "E698", {"start": v(6.62, 0.9) * mm, "end": v(6.55, 0.87) * mm});
            skLineSegment(sketch, "E699", {"start": v(6.55, 0.87) * mm, "end": v(6.46, 0.83) * mm});
            skLineSegment(sketch, "E700", {"start": v(6.46, 0.83) * mm, "end": v(6.22, 0.75) * mm});
            skLineSegment(sketch, "E701", {"start": v(6.22, 0.75) * mm, "end": v(5.96, 0.67) * mm});
            skLineSegment(sketch, "E702", {"start": v(5.96, 0.67) * mm, "end": v(5.68, 0.58) * mm});
            skLineSegment(sketch, "E703", {"start": v(5.68, 0.58) * mm, "end": v(5.44, 0.48) * mm});
            skLineSegment(sketch, "E704", {"start": v(5.44, 0.48) * mm, "end": v(5.37, 0.45) * mm});
            skLineSegment(sketch, "E705", {"start": v(5.37, 0.45) * mm, "end": v(5.3, 0.4) * mm});
            skLineSegment(sketch, "E706", {"start": v(5.3, 0.4) * mm, "end": v(5.2, 0.35) * mm});
            skLineSegment(sketch, "E707", {"start": v(5.2, 0.35) * mm, "end": v(5.06, 0.26) * mm});
            skLineSegment(sketch, "E708", {"start": v(5.06, 0.26) * mm, "end": v(4.94, 0.2) * mm});
            skLineSegment(sketch, "E709", {"start": v(4.94, 0.2) * mm, "end": v(4.8, 0.13) * mm});
            skLineSegment(sketch, "E710", {"start": v(4.8, 0.13) * mm, "end": v(4.67, 0.07) * mm});
            skLineSegment(sketch, "E711", {"start": v(4.67, 0.07) * mm, "end": v(4.55, 0.03) * mm});
            skLineSegment(sketch, "E712", {"start": v(4.55, 0.03) * mm, "end": v(4.51, 0.01) * mm});
            skLineSegment(sketch, "E713", {"start": v(4.51, 0.01) * mm, "end": v(4.46, 0) * mm});
            skLineSegment(sketch, "E714", {"start": v(4.46, 0) * mm, "end": v(4.4, -0.01) * mm});
            skLineSegment(sketch, "E715", {"start": v(4.4, -0.01) * mm, "end": v(4.36, -0.02) * mm});
            skLineSegment(sketch, "E716", {"start": v(4.36, -0.02) * mm, "end": v(4.3, -0.04) * mm});
            skLineSegment(sketch, "E717", {"start": v(4.3, -0.04) * mm, "end": v(4.26, -0.05) * mm});
            skLineSegment(sketch, "E718", {"start": v(4.26, -0.05) * mm, "end": v(4.24, -0.06) * mm});
            skLineSegment(sketch, "E719", {"start": v(4.24, -0.06) * mm, "end": v(4.26, -0.06) * mm});
            skLineSegment(sketch, "E720", {"start": v(4.26, -0.06) * mm, "end": v(4.27, -0.06) * mm});
            skLineSegment(sketch, "E721", {"start": v(4.27, -0.06) * mm, "end": v(4.28, -0.07) * mm});
            skLineSegment(sketch, "E722", {"start": v(4.28, -0.07) * mm, "end": v(4.3, -0.08) * mm});
            skLineSegment(sketch, "E723", {"start": v(4.3, -0.08) * mm, "end": v(4.33, -0.1) * mm});
            skLineSegment(sketch, "E724", {"start": v(4.33, -0.1) * mm, "end": v(4.4, -0.11) * mm});
            skLineSegment(sketch, "E725", {"start": v(4.4, -0.11) * mm, "end": v(4.5, -0.14) * mm});
            skLineSegment(sketch, "E726", {"start": v(4.5, -0.14) * mm, "end": v(4.6, -0.17) * mm});
            skLineSegment(sketch, "E727", {"start": v(4.6, -0.17) * mm, "end": v(4.7, -0.2) * mm});
            skLineSegment(sketch, "E728", {"start": v(4.7, -0.2) * mm, "end": v(4.76, -0.23) * mm});
            skLineSegment(sketch, "E729", {"start": v(4.76, -0.23) * mm, "end": v(4.85, -0.25) * mm});
            skLineSegment(sketch, "E730", {"start": v(4.85, -0.25) * mm, "end": v(4.95, -0.27) * mm});
            skLineSegment(sketch, "E731", {"start": v(4.95, -0.27) * mm, "end": v(5.05, -0.3) * mm});
            skLineSegment(sketch, "E732", {"start": v(5.05, -0.3) * mm, "end": v(5.15, -0.32) * mm});
            skLineSegment(sketch, "E733", {"start": v(5.15, -0.32) * mm, "end": v(5.25, -0.34) * mm});
            skLineSegment(sketch, "E734", {"start": v(5.25, -0.34) * mm, "end": v(5.34, -0.36) * mm});
            skLineSegment(sketch, "E735", {"start": v(5.34, -0.36) * mm, "end": v(5.4, -0.37) * mm});
            skLineSegment(sketch, "E736", {"start": v(5.4, -0.37) * mm, "end": v(5.53, -0.39) * mm});
            skLineSegment(sketch, "E737", {"start": v(5.53, -0.39) * mm, "end": v(5.71, -0.4) * mm});
            skLineSegment(sketch, "E738", {"start": v(5.71, -0.4) * mm, "end": v(5.92, -0.42) * mm});
            skLineSegment(sketch, "E739", {"start": v(5.92, -0.42) * mm, "end": v(6.15, -0.43) * mm});
            skLineSegment(sketch, "E740", {"start": v(6.15, -0.43) * mm, "end": v(6.27, -0.43) * mm});
            skLineSegment(sketch, "E741", {"start": v(6.27, -0.43) * mm, "end": v(6.38, -0.44) * mm});
            skLineSegment(sketch, "E742", {"start": v(6.38, -0.44) * mm, "end": v(6.5, -0.45) * mm});
            skLineSegment(sketch, "E743", {"start": v(6.5, -0.45) * mm, "end": v(6.61, -0.45) * mm});
            skLineSegment(sketch, "E744", {"start": v(6.61, -0.45) * mm, "end": v(6.71, -0.46) * mm});
            skLineSegment(sketch, "E745", {"start": v(6.71, -0.46) * mm, "end": v(6.8, -0.47) * mm});
            skLineSegment(sketch, "E746", {"start": v(6.8, -0.47) * mm, "end": v(6.88, -0.47) * mm});
            skLineSegment(sketch, "E747", {"start": v(6.88, -0.47) * mm, "end": v(6.93, -0.48) * mm});
            skLineSegment(sketch, "E748", {"start": v(6.93, -0.48) * mm, "end": v(6.97, -0.49) * mm});
            skLineSegment(sketch, "E749", {"start": v(6.97, -0.49) * mm, "end": v(7.05, -0.5) * mm});
            skLineSegment(sketch, "E750", {"start": v(7.05, -0.5) * mm, "end": v(7.14, -0.5) * mm});
            skLineSegment(sketch, "E751", {"start": v(7.14, -0.5) * mm, "end": v(7.24, -0.5) * mm});
            skLineSegment(sketch, "E752", {"start": v(7.24, -0.5) * mm, "end": v(7.52, -0.51) * mm});
            skLineSegment(sketch, "E753", {"start": v(7.52, -0.51) * mm, "end": v(7.77, -0.54) * mm});
            skLineSegment(sketch, "E754", {"start": v(7.77, -0.54) * mm, "end": v(7.98, -0.6) * mm});
            skLineSegment(sketch, "E755", {"start": v(7.98, -0.6) * mm, "end": v(8.14, -0.65) * mm});
            skLineSegment(sketch, "E756", {"start": v(8.14, -0.65) * mm, "end": v(8.23, -0.7) * mm});
            skLineSegment(sketch, "E757", {"start": v(8.23, -0.7) * mm, "end": v(8.3, -0.74) * mm});
            skLineSegment(sketch, "E758", {"start": v(8.3, -0.74) * mm, "end": v(8.37, -0.77) * mm});
            skLineSegment(sketch, "E759", {"start": v(8.37, -0.77) * mm, "end": v(8.42, -0.8) * mm});
            skLineSegment(sketch, "E760", {"start": v(8.42, -0.8) * mm, "end": v(8.5, -0.87) * mm});
            skLineSegment(sketch, "E761", {"start": v(8.5, -0.87) * mm, "end": v(8.6, -0.95) * mm});
            skLineSegment(sketch, "E762", {"start": v(8.6, -0.95) * mm, "end": v(8.7, -1.03) * mm});
            skLineSegment(sketch, "E763", {"start": v(8.7, -1.03) * mm, "end": v(8.76, -1.1) * mm});
            skLineSegment(sketch, "E764", {"start": v(8.76, -1.1) * mm, "end": v(8.83, -1.2) * mm});
            skLineSegment(sketch, "E765", {"start": v(8.83, -1.2) * mm, "end": v(8.9, -1.31) * mm});
            skLineSegment(sketch, "E766", {"start": v(8.9, -1.31) * mm, "end": v(8.97, -1.45) * mm});
            skLineSegment(sketch, "E767", {"start": v(8.97, -1.45) * mm, "end": v(9.02, -1.6) * mm});
            skLineSegment(sketch, "E768", {"start": v(9.02, -1.6) * mm, "end": v(9.04, -1.65) * mm});
            skLineSegment(sketch, "E769", {"start": v(9.04, -1.65) * mm, "end": v(9.06, -1.7) * mm});
            skLineSegment(sketch, "E770", {"start": v(9.06, -1.7) * mm, "end": v(9.08, -1.78) * mm});
            skLineSegment(sketch, "E771", {"start": v(9.08, -1.78) * mm, "end": v(9.07, -1.9) * mm});
            skLineSegment(sketch, "E772", {"start": v(9.07, -1.9) * mm, "end": v(9.06, -2.05) * mm});
            skLineSegment(sketch, "E773", {"start": v(9.06, -2.05) * mm, "end": v(9.04, -2.19) * mm});
            skLineSegment(sketch, "E774", {"start": v(9.04, -2.19) * mm, "end": v(9.03, -2.23) * mm});
            skLineSegment(sketch, "E775", {"start": v(9.03, -2.23) * mm, "end": v(9.02, -2.27) * mm});
            skLineSegment(sketch, "E776", {"start": v(9.02, -2.27) * mm, "end": v(9.02, -2.3) * mm});
            skLineSegment(sketch, "E777", {"start": v(9.02, -2.3) * mm, "end": v(9.02, -2.3) * mm});
            skLineSegment(sketch, "E778", {"start": v(9.02, -2.3) * mm, "end": v(9.02, -2.32) * mm});
            skLineSegment(sketch, "E779", {"start": v(9.02, -2.32) * mm, "end": v(9, -2.35) * mm});
            skLineSegment(sketch, "E780", {"start": v(9, -2.35) * mm, "end": v(8.98, -2.37) * mm});
            skLineSegment(sketch, "E781", {"start": v(8.98, -2.37) * mm, "end": v(8.96, -2.4) * mm});
            skLineSegment(sketch, "E782", {"start": v(8.96, -2.4) * mm, "end": v(8.95, -2.41) * mm});
            skLineSegment(sketch, "E783", {"start": v(8.95, -2.41) * mm, "end": v(8.94, -2.42) * mm});
            skLineSegment(sketch, "E784", {"start": v(8.94, -2.42) * mm, "end": v(8.92, -2.42) * mm});
            skLineSegment(sketch, "E785", {"start": v(8.92, -2.42) * mm, "end": v(8.9, -2.42) * mm});
            skLineSegment(sketch, "E786", {"start": v(8.9, -2.42) * mm, "end": v(8.86, -2.42) * mm});
            skLineSegment(sketch, "E787", {"start": v(8.86, -2.42) * mm, "end": v(8.82, -2.4) * mm});
            skLineSegment(sketch, "E788", {"start": v(8.82, -2.4) * mm, "end": v(8.75, -2.4) * mm});
            skLineSegment(sketch, "E789", {"start": v(8.75, -2.4) * mm, "end": v(8.67, -2.37) * mm});
            skLineSegment(sketch, "E790", {"start": v(8.67, -2.37) * mm, "end": v(8.39, -2.32) * mm});
            skLineSegment(sketch, "E791", {"start": v(8.39, -2.32) * mm, "end": v(8.1, -2.28) * mm});
            skLineSegment(sketch, "E792", {"start": v(8.1, -2.28) * mm, "end": v(7.81, -2.26) * mm});
            skLineSegment(sketch, "E793", {"start": v(7.81, -2.26) * mm, "end": v(7.5, -2.25) * mm});
            skLineSegment(sketch, "E794", {"start": v(7.5, -2.25) * mm, "end": v(7.35, -2.25) * mm});
            skLineSegment(sketch, "E795", {"start": v(7.35, -2.25) * mm, "end": v(7.24, -2.26) * mm});
            skLineSegment(sketch, "E796", {"start": v(7.24, -2.26) * mm, "end": v(7.14, -2.27) * mm});
            skLineSegment(sketch, "E797", {"start": v(7.14, -2.27) * mm, "end": v(7.05, -2.28) * mm});
            skLineSegment(sketch, "E798", {"start": v(7.05, -2.28) * mm, "end": v(6.76, -2.33) * mm});
            skLineSegment(sketch, "E799", {"start": v(6.76, -2.33) * mm, "end": v(6.51, -2.4) * mm});
            skLineSegment(sketch, "E800", {"start": v(6.51, -2.4) * mm, "end": v(6.46, -2.42) * mm});
            skLineSegment(sketch, "E801", {"start": v(6.46, -2.42) * mm, "end": v(6.4, -2.44) * mm});
            skLineSegment(sketch, "E802", {"start": v(6.4, -2.44) * mm, "end": v(6.35, -2.46) * mm});
            skLineSegment(sketch, "E803", {"start": v(6.35, -2.46) * mm, "end": v(6.32, -2.47) * mm});
            skLineSegment(sketch, "E804", {"start": v(6.32, -2.47) * mm, "end": v(6.28, -2.48) * mm});
            skLineSegment(sketch, "E805", {"start": v(6.28, -2.48) * mm, "end": v(6.23, -2.5) * mm});
            skLineSegment(sketch, "E806", {"start": v(6.23, -2.5) * mm, "end": v(6.17, -2.52) * mm});
            skLineSegment(sketch, "E807", {"start": v(6.17, -2.52) * mm, "end": v(6.1, -2.55) * mm});
            skLineSegment(sketch, "E808", {"start": v(6.1, -2.55) * mm, "end": v(6.03, -2.57) * mm});
            skLineSegment(sketch, "E809", {"start": v(6.03, -2.57) * mm, "end": v(5.96, -2.6) * mm});
            skLineSegment(sketch, "E810", {"start": v(5.96, -2.6) * mm, "end": v(5.9, -2.61) * mm});
            skLineSegment(sketch, "E811", {"start": v(5.9, -2.61) * mm, "end": v(5.85, -2.63) * mm});
            skLineSegment(sketch, "E812", {"start": v(5.85, -2.63) * mm, "end": v(5.81, -2.64) * mm});
            skLineSegment(sketch, "E813", {"start": v(5.81, -2.64) * mm, "end": v(5.78, -2.65) * mm});
            skLineSegment(sketch, "E814", {"start": v(5.78, -2.65) * mm, "end": v(5.75, -2.66) * mm});
            skLineSegment(sketch, "E815", {"start": v(5.75, -2.66) * mm, "end": v(5.73, -2.67) * mm});
            skLineSegment(sketch, "E816", {"start": v(5.73, -2.67) * mm, "end": v(5.7, -2.68) * mm});
            skLineSegment(sketch, "E817", {"start": v(5.7, -2.68) * mm, "end": v(5.64, -2.7) * mm});
            skLineSegment(sketch, "E818", {"start": v(5.64, -2.7) * mm, "end": v(5.57, -2.71) * mm});
            skLineSegment(sketch, "E819", {"start": v(5.57, -2.71) * mm, "end": v(5.48, -2.74) * mm});
            skLineSegment(sketch, "E820", {"start": v(5.48, -2.74) * mm, "end": v(5.34, -2.77) * mm});
            skLineSegment(sketch, "E821", {"start": v(5.34, -2.77) * mm, "end": v(5.2, -2.8) * mm});
            skLineSegment(sketch, "E822", {"start": v(5.2, -2.8) * mm, "end": v(5.06, -2.82) * mm});
            skLineSegment(sketch, "E823", {"start": v(5.06, -2.82) * mm, "end": v(4.88, -2.85) * mm});
            skLineSegment(sketch, "E824", {"start": v(4.88, -2.85) * mm, "end": v(4.75, -2.87) * mm});
            skLineSegment(sketch, "E825", {"start": v(4.75, -2.87) * mm, "end": v(4.6, -2.9) * mm});
            skLineSegment(sketch, "E826", {"start": v(4.6, -2.9) * mm, "end": v(4.44, -2.92) * mm});
            skLineSegment(sketch, "E827", {"start": v(4.44, -2.92) * mm, "end": v(4.29, -2.94) * mm});
            skLineSegment(sketch, "E828", {"start": v(4.29, -2.94) * mm, "end": v(4.13, -2.94) * mm});
            skLineSegment(sketch, "E829", {"start": v(4.13, -2.94) * mm, "end": v(3.94, -2.94) * mm});
            skLineSegment(sketch, "E830", {"start": v(3.94, -2.94) * mm, "end": v(3.8, -2.94) * mm});
            skLineSegment(sketch, "E831", {"start": v(3.8, -2.94) * mm, "end": v(3.7, -2.93) * mm});
            skLineSegment(sketch, "E832", {"start": v(3.7, -2.93) * mm, "end": v(3.59, -2.92) * mm});
            skLineSegment(sketch, "E833", {"start": v(3.59, -2.92) * mm, "end": v(3.48, -2.91) * mm});
            skLineSegment(sketch, "E834", {"start": v(3.48, -2.91) * mm, "end": v(3.4, -2.9) * mm});
            skLineSegment(sketch, "E835", {"start": v(3.4, -2.9) * mm, "end": v(3.32, -2.89) * mm});
            skLineSegment(sketch, "E836", {"start": v(3.32, -2.89) * mm, "end": v(3.26, -2.88) * mm});
            skLineSegment(sketch, "E837", {"start": v(3.26, -2.88) * mm, "end": v(3.23, -2.87) * mm});
            skLineSegment(sketch, "E838", {"start": v(3.23, -2.87) * mm, "end": v(3.21, -2.86) * mm});
            skLineSegment(sketch, "E839", {"start": v(3.21, -2.86) * mm, "end": v(3.18, -2.86) * mm});
            skLineSegment(sketch, "E840", {"start": v(3.18, -2.86) * mm, "end": v(3.15, -2.85) * mm});
            skLineSegment(sketch, "E841", {"start": v(3.15, -2.85) * mm, "end": v(3.11, -2.84) * mm});
            skLineSegment(sketch, "E842", {"start": v(3.11, -2.84) * mm, "end": v(2.96, -2.8) * mm});
            skLineSegment(sketch, "E843", {"start": v(2.96, -2.8) * mm, "end": v(2.8, -2.75) * mm});
            skLineSegment(sketch, "E844", {"start": v(2.8, -2.75) * mm, "end": v(2.65, -2.7) * mm});
            skLineSegment(sketch, "E845", {"start": v(2.65, -2.7) * mm, "end": v(2.47, -2.62) * mm});
            skLineSegment(sketch, "E846", {"start": v(2.47, -2.62) * mm, "end": v(2.39, -2.58) * mm});
            skLineSegment(sketch, "E847", {"start": v(2.39, -2.58) * mm, "end": v(2.3, -2.54) * mm});
            skLineSegment(sketch, "E848", {"start": v(2.3, -2.54) * mm, "end": v(2.24, -2.51) * mm});
            skLineSegment(sketch, "E849", {"start": v(2.24, -2.51) * mm, "end": v(2.2, -2.5) * mm});
            skLineSegment(sketch, "E850", {"start": v(2.2, -2.5) * mm, "end": v(2.1, -2.45) * mm});
            skLineSegment(sketch, "E851", {"start": v(2.1, -2.45) * mm, "end": v(2, -2.4) * mm});
            skLineSegment(sketch, "E852", {"start": v(2, -2.4) * mm, "end": v(1.9, -2.35) * mm});
            skLineSegment(sketch, "E853", {"start": v(1.9, -2.35) * mm, "end": v(1.82, -2.3) * mm});
            skLineSegment(sketch, "E854", {"start": v(1.82, -2.3) * mm, "end": v(1.78, -2.28) * mm});
            skLineSegment(sketch, "E855", {"start": v(1.78, -2.28) * mm, "end": v(1.74, -2.26) * mm});
            skLineSegment(sketch, "E856", {"start": v(1.74, -2.26) * mm, "end": v(1.7, -2.24) * mm});
            skLineSegment(sketch, "E857", {"start": v(1.7, -2.24) * mm, "end": v(1.66, -2.21) * mm});
            skLineSegment(sketch, "E858", {"start": v(1.66, -2.21) * mm, "end": v(1.62, -2.2) * mm});
            skLineSegment(sketch, "E859", {"start": v(1.62, -2.2) * mm, "end": v(1.58, -2.17) * mm});
            skLineSegment(sketch, "E860", {"start": v(1.58, -2.17) * mm, "end": v(1.54, -2.15) * mm});
            skLineSegment(sketch, "E861", {"start": v(1.54, -2.15) * mm, "end": v(1.51, -2.13) * mm});
            skLineSegment(sketch, "E862", {"start": v(1.51, -2.13) * mm, "end": v(1.42, -2.07) * mm});
            skLineSegment(sketch, "E863", {"start": v(1.42, -2.07) * mm, "end": v(1.33, -2) * mm});
            skLineSegment(sketch, "E864", {"start": v(1.33, -2) * mm, "end": v(1.25, -1.96) * mm});
            skLineSegment(sketch, "E865", {"start": v(1.25, -1.96) * mm, "end": v(1.2, -1.92) * mm});
            skLineSegment(sketch, "E866", {"start": v(1.2, -1.92) * mm, "end": v(1.17, -1.9) * mm});
            skLineSegment(sketch, "E867", {"start": v(1.17, -1.9) * mm, "end": v(1.13, -1.88) * mm});
            skLineSegment(sketch, "E868", {"start": v(1.13, -1.88) * mm, "end": v(1.1, -1.86) * mm});
            skLineSegment(sketch, "E869", {"start": v(1.1, -1.86) * mm, "end": v(1.05, -1.83) * mm});
            skLineSegment(sketch, "E870", {"start": v(1.05, -1.83) * mm, "end": v(1.02, -1.8) * mm});
            skLineSegment(sketch, "E871", {"start": v(1.02, -1.8) * mm, "end": v(0.98, -1.78) * mm});
            skLineSegment(sketch, "E872", {"start": v(0.98, -1.78) * mm, "end": v(0.95, -1.75) * mm});
            skLineSegment(sketch, "E873", {"start": v(0.95, -1.75) * mm, "end": v(0.93, -1.74) * mm});
            skLineSegment(sketch, "E874", {"start": v(0.93, -1.74) * mm, "end": v(0.9, -1.72) * mm});
            skLineSegment(sketch, "E875", {"start": v(0.9, -1.72) * mm, "end": v(0.88, -1.7) * mm});
            skLineSegment(sketch, "E876", {"start": v(0.88, -1.7) * mm, "end": v(0.85, -1.68) * mm});
            skLineSegment(sketch, "E877", {"start": v(0.85, -1.68) * mm, "end": v(0.82, -1.65) * mm});
            skLineSegment(sketch, "E878", {"start": v(0.82, -1.65) * mm, "end": v(0.8, -1.63) * mm});
            skLineSegment(sketch, "E879", {"start": v(0.8, -1.63) * mm, "end": v(0.76, -1.6) * mm});
            skLineSegment(sketch, "E880", {"start": v(0.76, -1.6) * mm, "end": v(0.73, -1.58) * mm});
            skLineSegment(sketch, "E881", {"start": v(0.73, -1.58) * mm, "end": v(0.71, -1.56) * mm});
            skLineSegment(sketch, "E882", {"start": v(0.71, -1.56) * mm, "end": v(0.68, -1.54) * mm});
            skLineSegment(sketch, "E883", {"start": v(0.68, -1.54) * mm, "end": v(0.67, -1.52) * mm});
            skLineSegment(sketch, "E884", {"start": v(0.67, -1.52) * mm, "end": v(0.66, -1.56) * mm});
            skLineSegment(sketch, "E885", {"start": v(0.66, -1.56) * mm, "end": v(0.65, -1.64) * mm});
            skLineSegment(sketch, "E886", {"start": v(0.65, -1.64) * mm, "end": v(0.63, -1.77) * mm});
            skLineSegment(sketch, "E887", {"start": v(0.63, -1.77) * mm, "end": v(0.61, -1.91) * mm});
            skLineSegment(sketch, "E888", {"start": v(0.61, -1.91) * mm, "end": v(0.6, -1.94) * mm});
            skLineSegment(sketch, "E889", {"start": v(0.6, -1.94) * mm, "end": v(0.6, -1.99) * mm});
            skLineSegment(sketch, "E890", {"start": v(0.6, -1.99) * mm, "end": v(0.6, -2.03) * mm});
            skLineSegment(sketch, "E891", {"start": v(0.6, -2.03) * mm, "end": v(0.59, -2.07) * mm});
            skLineSegment(sketch, "E892", {"start": v(0.59, -2.07) * mm, "end": v(0.58, -2.12) * mm});
            skLineSegment(sketch, "E893", {"start": v(0.58, -2.12) * mm, "end": v(0.57, -2.18) * mm});
            skLineSegment(sketch, "E894", {"start": v(0.57, -2.18) * mm, "end": v(0.56, -2.23) * mm});
            skLineSegment(sketch, "E895", {"start": v(0.56, -2.23) * mm, "end": v(0.55, -2.28) * mm});
            skLineSegment(sketch, "E896", {"start": v(0.55, -2.28) * mm, "end": v(0.54, -2.34) * mm});
            skLineSegment(sketch, "E897", {"start": v(0.54, -2.34) * mm, "end": v(0.52, -2.43) * mm});
            skLineSegment(sketch, "E898", {"start": v(0.52, -2.43) * mm, "end": v(0.5, -2.54) * mm});
            skLineSegment(sketch, "E899", {"start": v(0.5, -2.54) * mm, "end": v(0.46, -2.65) * mm});
            skLineSegment(sketch, "E900", {"start": v(0.46, -2.65) * mm, "end": v(0.4, -2.88) * mm});
            skLineSegment(sketch, "E901", {"start": v(0.4, -2.88) * mm, "end": v(0.33, -3.06) * mm});
            skLineSegment(sketch, "E902", {"start": v(0.33, -3.06) * mm, "end": v(0.25, -3.2) * mm});
            skLineSegment(sketch, "E903", {"start": v(0.25, -3.2) * mm, "end": v(0.16, -3.3) * mm});
            skLineSegment(sketch, "E904", {"start": v(0.16, -3.3) * mm, "end": v(0.09, -3.37) * mm});
            skLineSegment(sketch, "E905", {"start": v(0.09, -3.37) * mm, "end": v(0.11, -3.4) * mm});
            skLineSegment(sketch, "E906", {"start": v(0.11, -3.4) * mm, "end": v(0.2, -3.57) * mm});
            skLineSegment(sketch, "E907", {"start": v(0.2, -3.57) * mm, "end": v(0.22, -3.77) * mm});
            skLineSegment(sketch, "E908", {"start": v(0.22, -3.77) * mm, "end": v(0.21, -3.87) * mm});
            skLineSegment(sketch, "E909", {"start": v(0.21, -3.87) * mm, "end": v(0.18, -3.98) * mm});
            skLineSegment(sketch, "E910", {"start": v(0.18, -3.98) * mm, "end": v(0.15, -4.07) * mm});
            skLineSegment(sketch, "E911", {"start": v(0.15, -4.07) * mm, "end": v(0.1, -4.15) * mm});
            skLineSegment(sketch, "E912", {"start": v(0.1, -4.15) * mm, "end": v(0.06, -4.2) * mm});
            skLineSegment(sketch, "E913", {"start": v(0.06, -4.2) * mm, "end": v(0.08, -4.23) * mm});
            skLineSegment(sketch, "E914", {"start": v(0.08, -4.23) * mm, "end": v(0.09, -4.25) * mm});
            skLineSegment(sketch, "E915", {"start": v(0.09, -4.25) * mm, "end": v(0.1, -4.28) * mm});
            skLineSegment(sketch, "E916", {"start": v(0.1, -4.28) * mm, "end": v(0.11, -4.31) * mm});
            skLineSegment(sketch, "E917", {"start": v(0.11, -4.31) * mm, "end": v(0.13, -4.35) * mm});
            skLineSegment(sketch, "E918", {"start": v(0.13, -4.35) * mm, "end": v(0.15, -4.52) * mm});
            skLineSegment(sketch, "E919", {"start": v(0.15, -4.52) * mm, "end": v(0.14, -4.7) * mm});
            skLineSegment(sketch, "E920", {"start": v(0.14, -4.7) * mm, "end": v(0.09, -4.86) * mm});
            skLineSegment(sketch, "E921", {"start": v(0.09, -4.86) * mm, "end": v(0, -5) * mm});
            skLineSegment(sketch, "E922", {"start": v(0, -5) * mm, "end": v(-0.02, -5.03) * mm});
            skLineSegment(sketch, "E923", {"start": v(-0.02, -5.03) * mm, "end": v(-0.03, -5.05) * mm});
            skLineSegment(sketch, "E924", {"start": v(-0.03, -5.05) * mm, "end": v(-0.04, -5.06) * mm});
            skLineSegment(sketch, "E925", {"start": v(-0.04, -5.06) * mm, "end": v(-0.05, -5.07) * mm});
            skLineSegment(sketch, "E926", {"start": v(-0.05, -5.07) * mm, "end": v(-0.04, -5.08) * mm});
            skLineSegment(sketch, "E927", {"start": v(-0.04, -5.08) * mm, "end": v(-0.01, -5.09) * mm});
            skLineSegment(sketch, "E928", {"start": v(-0.01, -5.09) * mm, "end": v(0.02, -5.11) * mm});
            skLineSegment(sketch, "E929", {"start": v(0.02, -5.11) * mm, "end": v(0.05, -5.15) * mm});
            skLineSegment(sketch, "E930", {"start": v(0.05, -5.15) * mm, "end": v(0.08, -5.21) * mm});
            skLineSegment(sketch, "E931", {"start": v(0.08, -5.21) * mm, "end": v(0.11, -5.28) * mm});
            skLineSegment(sketch, "E932", {"start": v(0.11, -5.28) * mm, "end": v(0.12, -5.32) * mm});
            skLineSegment(sketch, "E933", {"start": v(0.12, -5.32) * mm, "end": v(0.13, -5.37) * mm});
            skLineSegment(sketch, "E934", {"start": v(0.13, -5.37) * mm, "end": v(0.13, -5.42) * mm});
            skLineSegment(sketch, "E935", {"start": v(0.13, -5.42) * mm, "end": v(0.13, -5.5) * mm});
            skLineSegment(sketch, "E936", {"start": v(0.13, -5.5) * mm, "end": v(0.13, -5.57) * mm});
            skLineSegment(sketch, "E937", {"start": v(0.13, -5.57) * mm, "end": v(0.12, -5.62) * mm});
            skLineSegment(sketch, "E938", {"start": v(0.12, -5.62) * mm, "end": v(0.11, -5.65) * mm});
            skLineSegment(sketch, "E939", {"start": v(0.11, -5.65) * mm, "end": v(0.1, -5.69) * mm});
            skLineSegment(sketch, "E940", {"start": v(0.1, -5.69) * mm, "end": v(0.04, -5.76) * mm});
            skLineSegment(sketch, "E941", {"start": v(0.04, -5.76) * mm, "end": v(-0.02, -5.81) * mm});
            skLineSegment(sketch, "E942", {"start": v(-0.02, -5.81) * mm, "end": v(-0.11, -5.85) * mm});
            skLineSegment(sketch, "E943", {"start": v(-0.11, -5.85) * mm, "end": v(-0.23, -5.86) * mm});
            skLineSegment(sketch, "E944", {"start": v(-0.23, -5.86) * mm, "end": v(-0.28, -5.86) * mm});
            skLineSegment(sketch, "E945", {"start": v(-0.28, -5.86) * mm, "end": v(-0.32, -5.86) * mm});
            skLineSegment(sketch, "E946", {"start": v(-0.32, -5.86) * mm, "end": v(-0.35, -5.86) * mm});
            skLineSegment(sketch, "E947", {"start": v(-0.35, -5.86) * mm, "end": v(-0.38, -5.85) * mm});
            skLineSegment(sketch, "E948", {"start": v(-0.16, -5.57) * mm, "end": v(-0.1, -5.53) * mm});
            skLineSegment(sketch, "E949", {"start": v(-0.1, -5.53) * mm, "end": v(-0.06, -5.48) * mm});
            skLineSegment(sketch, "E950", {"start": v(-0.06, -5.48) * mm, "end": v(-0.06, -5.42) * mm});
            skLineSegment(sketch, "E951", {"start": v(-0.06, -5.42) * mm, "end": v(-0.1, -5.34) * mm});
            skLineSegment(sketch, "E952", {"start": v(-0.1, -5.34) * mm, "end": v(-0.13, -5.27) * mm});
            skLineSegment(sketch, "E953", {"start": v(-0.13, -5.27) * mm, "end": v(-0.17, -5.23) * mm});
            skLineSegment(sketch, "E954", {"start": v(-0.17, -5.23) * mm, "end": v(-0.22, -5.21) * mm});
            skLineSegment(sketch, "E955", {"start": v(-0.22, -5.21) * mm, "end": v(-0.27, -5.23) * mm});
            skLineSegment(sketch, "E956", {"start": v(-0.27, -5.23) * mm, "end": v(-0.3, -5.25) * mm});
            skLineSegment(sketch, "E957", {"start": v(-0.3, -5.25) * mm, "end": v(-0.32, -5.27) * mm});
            skLineSegment(sketch, "E958", {"start": v(-0.32, -5.27) * mm, "end": v(-0.35, -5.3) * mm});
            skLineSegment(sketch, "E959", {"start": v(-0.35, -5.3) * mm, "end": v(-0.37, -5.33) * mm});
            skLineSegment(sketch, "E960", {"start": v(-0.37, -5.33) * mm, "end": v(-0.37, -5.36) * mm});
            skLineSegment(sketch, "E961", {"start": v(-0.37, -5.36) * mm, "end": v(-0.37, -5.4) * mm});
            skLineSegment(sketch, "E962", {"start": v(-0.37, -5.4) * mm, "end": v(-0.37, -5.44) * mm});
            skLineSegment(sketch, "E963", {"start": v(-0.37, -5.44) * mm, "end": v(-0.35, -5.47) * mm});
            skLineSegment(sketch, "E964", {"start": v(-0.35, -5.47) * mm, "end": v(-0.33, -5.5) * mm});
            skLineSegment(sketch, "E965", {"start": v(-0.33, -5.5) * mm, "end": v(-0.3, -5.55) * mm});
            skLineSegment(sketch, "E966", {"start": v(-0.3, -5.55) * mm, "end": v(-0.26, -5.58) * mm});
            skLineSegment(sketch, "E967", {"start": v(-0.26, -5.58) * mm, "end": v(-0.24, -5.6) * mm});
            skLineSegment(sketch, "E968", {"start": v(-0.24, -5.6) * mm, "end": v(-0.21, -5.58) * mm});
            skLineSegment(sketch, "E969", {"start": v(-0.21, -5.58) * mm, "end": v(-0.16, -5.57) * mm});
            skLineSegment(sketch, "E970", {"start": v(-0.12, -4.85) * mm, "end": v(-0.06, -4.75) * mm});
            skLineSegment(sketch, "E971", {"start": v(-0.06, -4.75) * mm, "end": v(-0.04, -4.6) * mm});
            skLineSegment(sketch, "E972", {"start": v(-0.04, -4.6) * mm, "end": v(-0.03, -4.55) * mm});
            skLineSegment(sketch, "E973", {"start": v(-0.03, -4.55) * mm, "end": v(-0.04, -4.51) * mm});
            skLineSegment(sketch, "E974", {"start": v(-0.04, -4.51) * mm, "end": v(-0.04, -4.49) * mm});
            skLineSegment(sketch, "E975", {"start": v(-0.04, -4.49) * mm, "end": v(-0.06, -4.46) * mm});
            skLineSegment(sketch, "E976", {"start": v(-0.06, -4.46) * mm, "end": v(-0.09, -4.43) * mm});
            skLineSegment(sketch, "E977", {"start": v(-0.09, -4.43) * mm, "end": v(-0.12, -4.4) * mm});
            skLineSegment(sketch, "E978", {"start": v(-0.12, -4.4) * mm, "end": v(-0.14, -4.4) * mm});
            skLineSegment(sketch, "E979", {"start": v(-0.14, -4.4) * mm, "end": v(-0.16, -4.4) * mm});
            skLineSegment(sketch, "E980", {"start": v(-0.16, -4.4) * mm, "end": v(-0.18, -4.4) * mm});
            skLineSegment(sketch, "E981", {"start": v(-0.18, -4.4) * mm, "end": v(-0.2, -4.41) * mm});
            skLineSegment(sketch, "E982", {"start": v(-0.2, -4.41) * mm, "end": v(-0.26, -4.45) * mm});
            skLineSegment(sketch, "E983", {"start": v(-0.26, -4.45) * mm, "end": v(-0.3, -4.5) * mm});
            skLineSegment(sketch, "E984", {"start": v(-0.3, -4.5) * mm, "end": v(-0.33, -4.55) * mm});
            skLineSegment(sketch, "E985", {"start": v(-0.33, -4.55) * mm, "end": v(-0.35, -4.6) * mm});
            skLineSegment(sketch, "E986", {"start": v(-0.35, -4.6) * mm, "end": v(-0.35, -4.67) * mm});
            skLineSegment(sketch, "E987", {"start": v(-0.35, -4.67) * mm, "end": v(-0.34, -4.74) * mm});
            skLineSegment(sketch, "E988", {"start": v(-0.34, -4.74) * mm, "end": v(-0.3, -4.8) * mm});
            skLineSegment(sketch, "E989", {"start": v(-0.3, -4.8) * mm, "end": v(-0.27, -4.85) * mm});
            skLineSegment(sketch, "E990", {"start": v(-0.27, -4.85) * mm, "end": v(-0.25, -4.87) * mm});
            skLineSegment(sketch, "E991", {"start": v(-0.25, -4.87) * mm, "end": v(-0.23, -4.88) * mm});
            skLineSegment(sketch, "E992", {"start": v(-0.23, -4.88) * mm, "end": v(-0.21, -4.88) * mm});
            skLineSegment(sketch, "E993", {"start": v(-0.21, -4.88) * mm, "end": v(-0.19, -4.88) * mm});
            skLineSegment(sketch, "E994", {"start": v(-0.19, -4.88) * mm, "end": v(-0.15, -4.87) * mm});
            skLineSegment(sketch, "E995", {"start": v(-0.15, -4.87) * mm, "end": v(-0.12, -4.85) * mm});
            skLineSegment(sketch, "E996", {"start": v(-0.24, -4.07) * mm, "end": v(-0.2, -4.03) * mm});
            skLineSegment(sketch, "E997", {"start": v(-0.2, -4.03) * mm, "end": v(-0.14, -3.97) * mm});
            skLineSegment(sketch, "E998", {"start": v(-0.14, -3.97) * mm, "end": v(-0.12, -3.93) * mm});
            skLineSegment(sketch, "E999", {"start": v(-0.12, -3.93) * mm, "end": v(-0.1, -3.9) * mm});
            skLineSegment(sketch, "E1000", {"start": v(-0.1, -3.9) * mm, "end": v(-0.1, -3.86) * mm});
            skLineSegment(sketch, "E1001", {"start": v(-0.1, -3.86) * mm, "end": v(-0.1, -3.82) * mm});
            skLineSegment(sketch, "E1002", {"start": v(-0.1, -3.82) * mm, "end": v(-0.1, -3.77) * mm});
            skLineSegment(sketch, "E1003", {"start": v(-0.1, -3.77) * mm, "end": v(-0.1, -3.74) * mm});
            skLineSegment(sketch, "E1004", {"start": v(-0.1, -3.74) * mm, "end": v(-0.12, -3.7) * mm});
            skLineSegment(sketch, "E1005", {"start": v(-0.12, -3.7) * mm, "end": v(-0.15, -3.66) * mm});
            skLineSegment(sketch, "E1006", {"start": v(-0.15, -3.66) * mm, "end": v(-0.2, -3.6) * mm});
            skLineSegment(sketch, "E1007", {"start": v(-0.2, -3.6) * mm, "end": v(-0.23, -3.56) * mm});
            skLineSegment(sketch, "E1008", {"start": v(-0.23, -3.56) * mm, "end": v(-0.27, -3.55) * mm});
            skLineSegment(sketch, "E1009", {"start": v(-0.27, -3.55) * mm, "end": v(-0.32, -3.55) * mm});
            skLineSegment(sketch, "E1010", {"start": v(-0.32, -3.55) * mm, "end": v(-0.35, -3.56) * mm});
            skLineSegment(sketch, "E1011", {"start": v(-0.35, -3.56) * mm, "end": v(-0.38, -3.57) * mm});
            skLineSegment(sketch, "E1012", {"start": v(-0.38, -3.57) * mm, "end": v(-0.4, -3.6) * mm});
            skLineSegment(sketch, "E1013", {"start": v(-0.4, -3.6) * mm, "end": v(-0.44, -3.63) * mm});
            skLineSegment(sketch, "E1014", {"start": v(-0.44, -3.63) * mm, "end": v(-0.48, -3.67) * mm});
            skLineSegment(sketch, "E1015", {"start": v(-0.48, -3.67) * mm, "end": v(-0.5, -3.7) * mm});
            skLineSegment(sketch, "E1016", {"start": v(-0.5, -3.7) * mm, "end": v(-0.52, -3.73) * mm});
            skLineSegment(sketch, "E1017", {"start": v(-0.52, -3.73) * mm, "end": v(-0.53, -3.78) * mm});
            skLineSegment(sketch, "E1018", {"start": v(-0.53, -3.78) * mm, "end": v(-0.56, -3.89) * mm});
            skLineSegment(sketch, "E1019", {"start": v(-0.56, -3.89) * mm, "end": v(-0.55, -3.97) * mm});
            skLineSegment(sketch, "E1020", {"start": v(-0.55, -3.97) * mm, "end": v(-0.5, -4.04) * mm});
            skLineSegment(sketch, "E1021", {"start": v(-0.5, -4.04) * mm, "end": v(-0.43, -4.08) * mm});
            skLineSegment(sketch, "E1022", {"start": v(-0.43, -4.08) * mm, "end": v(-0.33, -4.1) * mm});
            skLineSegment(sketch, "E1023", {"start": v(-0.33, -4.1) * mm, "end": v(-0.24, -4.07) * mm});
            skLineSegment(sketch, "E1024", {"start": v(-0.03, -2.92) * mm, "end": v(0, -2.88) * mm});
            skLineSegment(sketch, "E1025", {"start": v(0, -2.88) * mm, "end": v(0.04, -2.83) * mm});
            skLineSegment(sketch, "E1026", {"start": v(0.04, -2.83) * mm, "end": v(0.07, -2.78) * mm});
            skLineSegment(sketch, "E1027", {"start": v(0.07, -2.78) * mm, "end": v(0.11, -2.7) * mm});
            skLineSegment(sketch, "E1028", {"start": v(0.11, -2.7) * mm, "end": v(0.14, -2.65) * mm});
            skLineSegment(sketch, "E1029", {"start": v(0.14, -2.65) * mm, "end": v(0.16, -2.59) * mm});
            skLineSegment(sketch, "E1030", {"start": v(0.16, -2.59) * mm, "end": v(0.18, -2.54) * mm});
            skLineSegment(sketch, "E1031", {"start": v(0.18, -2.54) * mm, "end": v(0.2, -2.5) * mm});
            skLineSegment(sketch, "E1032", {"start": v(0.2, -2.5) * mm, "end": v(0.21, -2.43) * mm});
            skLineSegment(sketch, "E1033", {"start": v(0.21, -2.43) * mm, "end": v(0.23, -2.36) * mm});
            skLineSegment(sketch, "E1034", {"start": v(0.23, -2.36) * mm, "end": v(0.25, -2.27) * mm});
            skLineSegment(sketch, "E1035", {"start": v(0.25, -2.27) * mm, "end": v(0.28, -2.14) * mm});
            skLineSegment(sketch, "E1036", {"start": v(0.28, -2.14) * mm, "end": v(0.3, -2) * mm});
            skLineSegment(sketch, "E1037", {"start": v(0.3, -2) * mm, "end": v(0.33, -1.9) * mm});
            skLineSegment(sketch, "E1038", {"start": v(0.33, -1.9) * mm, "end": v(0.33, -1.84) * mm});
            skLineSegment(sketch, "E1039", {"start": v(0.33, -1.84) * mm, "end": v(0.3, -1.85) * mm});
            skLineSegment(sketch, "E1040", {"start": v(0.3, -1.85) * mm, "end": v(0.27, -1.85) * mm});
            skLineSegment(sketch, "E1041", {"start": v(0.27, -1.85) * mm, "end": v(0.24, -1.85) * mm});
            skLineSegment(sketch, "E1042", {"start": v(0.24, -1.85) * mm, "end": v(0.2, -1.85) * mm});
            skLineSegment(sketch, "E1043", {"start": v(0.2, -1.85) * mm, "end": v(0.16, -1.85) * mm});
            skLineSegment(sketch, "E1044", {"start": v(0.16, -1.85) * mm, "end": v(0.07, -1.84) * mm});
            skLineSegment(sketch, "E1045", {"start": v(0.07, -1.84) * mm, "end": v(-0.01, -1.9) * mm});
            skLineSegment(sketch, "E1046", {"start": v(-0.01, -1.9) * mm, "end": v(-0.05, -1.92) * mm});
            skLineSegment(sketch, "E1047", {"start": v(-0.05, -1.92) * mm, "end": v(-0.08, -1.94) * mm});
            skLineSegment(sketch, "E1048", {"start": v(-0.08, -1.94) * mm, "end": v(-0.11, -1.96) * mm});
            skLineSegment(sketch, "E1049", {"start": v(-0.11, -1.96) * mm, "end": v(-0.13, -1.97) * mm});
            skLineSegment(sketch, "E1050", {"start": v(-0.13, -1.97) * mm, "end": v(-0.27, -2.01) * mm});
            skLineSegment(sketch, "E1051", {"start": v(-0.27, -2.01) * mm, "end": v(-0.37, -2.04) * mm});
            skLineSegment(sketch, "E1052", {"start": v(-0.37, -2.04) * mm, "end": v(-0.46, -2.05) * mm});
            skLineSegment(sketch, "E1053", {"start": v(-0.46, -2.05) * mm, "end": v(-0.56, -2.05) * mm});
            skLineSegment(sketch, "E1054", {"start": v(-0.56, -2.05) * mm, "end": v(-0.62, -2.05) * mm});
            skLineSegment(sketch, "E1055", {"start": v(-0.62, -2.05) * mm, "end": v(-0.66, -2.05) * mm});
            skLineSegment(sketch, "E1056", {"start": v(-0.66, -2.05) * mm, "end": v(-0.68, -2.05) * mm});
            skLineSegment(sketch, "E1057", {"start": v(-0.68, -2.05) * mm, "end": v(-0.7, -2.06) * mm});
            skLineSegment(sketch, "E1058", {"start": v(-0.7, -2.06) * mm, "end": v(-0.7, -2.07) * mm});
            skLineSegment(sketch, "E1059", {"start": v(-0.7, -2.07) * mm, "end": v(-0.7, -2.1) * mm});
            skLineSegment(sketch, "E1060", {"start": v(-0.7, -2.1) * mm, "end": v(-0.68, -2.13) * mm});
            skLineSegment(sketch, "E1061", {"start": v(-0.68, -2.13) * mm, "end": v(-0.67, -2.17) * mm});
            skLineSegment(sketch, "E1062", {"start": v(-0.67, -2.17) * mm, "end": v(-0.63, -2.28) * mm});
            skLineSegment(sketch, "E1063", {"start": v(-0.63, -2.28) * mm, "end": v(-0.59, -2.4) * mm});
            skLineSegment(sketch, "E1064", {"start": v(-0.59, -2.4) * mm, "end": v(-0.54, -2.53) * mm});
            skLineSegment(sketch, "E1065", {"start": v(-0.54, -2.53) * mm, "end": v(-0.48, -2.66) * mm});
            skLineSegment(sketch, "E1066", {"start": v(-0.48, -2.66) * mm, "end": v(-0.41, -2.79) * mm});
            skLineSegment(sketch, "E1067", {"start": v(-0.41, -2.79) * mm, "end": v(-0.36, -2.89) * mm});
            skLineSegment(sketch, "E1068", {"start": v(-0.36, -2.89) * mm, "end": v(-0.31, -2.94) * mm});
            skLineSegment(sketch, "E1069", {"start": v(-0.31, -2.94) * mm, "end": v(-0.27, -2.98) * mm});
            skLineSegment(sketch, "E1070", {"start": v(-0.27, -2.98) * mm, "end": v(-0.22, -3) * mm});
            skLineSegment(sketch, "E1071", {"start": v(-0.22, -3) * mm, "end": v(-0.16, -3) * mm});
            skLineSegment(sketch, "E1072", {"start": v(-0.16, -3) * mm, "end": v(-0.14, -3) * mm});
            skLineSegment(sketch, "E1073", {"start": v(-0.14, -3) * mm, "end": v(-0.13, -3) * mm});
            skLineSegment(sketch, "E1074", {"start": v(-0.13, -3) * mm, "end": v(-0.12, -3) * mm});
            skLineSegment(sketch, "E1075", {"start": v(-0.12, -3) * mm, "end": v(-0.1, -3) * mm});
            skLineSegment(sketch, "E1076", {"start": v(-0.1, -3) * mm, "end": v(-0.1, -2.98) * mm});
            skLineSegment(sketch, "E1077", {"start": v(-0.1, -2.98) * mm, "end": v(-0.08, -2.97) * mm});
            skLineSegment(sketch, "E1078", {"start": v(-0.08, -2.97) * mm, "end": v(-0.06, -2.95) * mm});
            skLineSegment(sketch, "E1079", {"start": v(-0.06, -2.95) * mm, "end": v(-0.03, -2.92) * mm});
            skLineSegment(sketch, "E1080", {"start": v(3.92, -2.68) * mm, "end": v(3.91, -2.64) * mm});
            skLineSegment(sketch, "E1081", {"start": v(3.91, -2.64) * mm, "end": v(3.9, -2.6) * mm});
            skLineSegment(sketch, "E1082", {"start": v(3.9, -2.6) * mm, "end": v(3.87, -2.53) * mm});
            skLineSegment(sketch, "E1083", {"start": v(3.87, -2.53) * mm, "end": v(3.84, -2.46) * mm});
            skLineSegment(sketch, "E1084", {"start": v(3.84, -2.46) * mm, "end": v(3.8, -2.39) * mm});
            skLineSegment(sketch, "E1085", {"start": v(3.8, -2.39) * mm, "end": v(3.76, -2.32) * mm});
            skLineSegment(sketch, "E1086", {"start": v(3.76, -2.32) * mm, "end": v(3.73, -2.26) * mm});
            skLineSegment(sketch, "E1087", {"start": v(3.73, -2.26) * mm, "end": v(3.7, -2.2) * mm});
            skLineSegment(sketch, "E1088", {"start": v(3.7, -2.2) * mm, "end": v(3.67, -2.17) * mm});
            skLineSegment(sketch, "E1089", {"start": v(3.67, -2.17) * mm, "end": v(3.64, -2.13) * mm});
            skLineSegment(sketch, "E1090", {"start": v(3.64, -2.13) * mm, "end": v(3.6, -2.1) * mm});
            skLineSegment(sketch, "E1091", {"start": v(3.6, -2.1) * mm, "end": v(3.59, -2.06) * mm});
            skLineSegment(sketch, "E1092", {"start": v(3.59, -2.06) * mm, "end": v(3.53, -2) * mm});
            skLineSegment(sketch, "E1093", {"start": v(3.53, -2) * mm, "end": v(3.46, -1.91) * mm});
            skLineSegment(sketch, "E1094", {"start": v(3.46, -1.91) * mm, "end": v(3.37, -1.82) * mm});
            skLineSegment(sketch, "E1095", {"start": v(3.37, -1.82) * mm, "end": v(3.26, -1.73) * mm});
            skLineSegment(sketch, "E1096", {"start": v(3.26, -1.73) * mm, "end": v(3.15, -1.63) * mm});
            skLineSegment(sketch, "E1097", {"start": v(3.15, -1.63) * mm, "end": v(3.03, -1.54) * mm});
            skLineSegment(sketch, "E1098", {"start": v(3.03, -1.54) * mm, "end": v(2.92, -1.45) * mm});
            skLineSegment(sketch, "E1099", {"start": v(2.92, -1.45) * mm, "end": v(2.82, -1.38) * mm});
            skLineSegment(sketch, "E1100", {"start": v(2.82, -1.38) * mm, "end": v(2.64, -1.27) * mm});
            skLineSegment(sketch, "E1101", {"start": v(2.64, -1.27) * mm, "end": v(2.45, -1.16) * mm});
            skLineSegment(sketch, "E1102", {"start": v(2.45, -1.16) * mm, "end": v(2.26, -1.06) * mm});
            skLineSegment(sketch, "E1103", {"start": v(2.26, -1.06) * mm, "end": v(2.07, -0.97) * mm});
            skLineSegment(sketch, "E1104", {"start": v(2.07, -0.97) * mm, "end": v(1.97, -0.94) * mm});
            skLineSegment(sketch, "E1105", {"start": v(1.97, -0.94) * mm, "end": v(1.83, -0.9) * mm});
            skLineSegment(sketch, "E1106", {"start": v(1.83, -0.9) * mm, "end": v(1.7, -0.85) * mm});
            skLineSegment(sketch, "E1107", {"start": v(1.7, -0.85) * mm, "end": v(1.6, -0.83) * mm});
            skLineSegment(sketch, "E1108", {"start": v(1.6, -0.83) * mm, "end": v(1.54, -0.82) * mm});
            skLineSegment(sketch, "E1109", {"start": v(1.54, -0.82) * mm, "end": v(1.49, -0.8) * mm});
            skLineSegment(sketch, "E1110", {"start": v(1.49, -0.8) * mm, "end": v(1.45, -0.8) * mm});
            skLineSegment(sketch, "E1111", {"start": v(1.45, -0.8) * mm, "end": v(1.4, -0.8) * mm});
            skLineSegment(sketch, "E1112", {"start": v(1.4, -0.8) * mm, "end": v(1.34, -0.78) * mm});
            skLineSegment(sketch, "E1113", {"start": v(1.34, -0.78) * mm, "end": v(1.29, -0.77) * mm});
            skLineSegment(sketch, "E1114", {"start": v(1.29, -0.77) * mm, "end": v(1.23, -0.77) * mm});
            skLineSegment(sketch, "E1115", {"start": v(1.23, -0.77) * mm, "end": v(1.19, -0.76) * mm});
            skLineSegment(sketch, "E1116", {"start": v(1.19, -0.76) * mm, "end": v(1.16, -0.76) * mm});
            skLineSegment(sketch, "E1117", {"start": v(1.16, -0.76) * mm, "end": v(1.14, -0.75) * mm});
            skLineSegment(sketch, "E1118", {"start": v(1.14, -0.75) * mm, "end": v(1.13, -0.75) * mm});
            skLineSegment(sketch, "E1119", {"start": v(1.13, -0.75) * mm, "end": v(1.08, -0.74) * mm});
            skLineSegment(sketch, "E1120", {"start": v(1.08, -0.74) * mm, "end": v(1.02, -0.74) * mm});
            skLineSegment(sketch, "E1121", {"start": v(1.02, -0.74) * mm, "end": v(0.95, -0.73) * mm});
            skLineSegment(sketch, "E1122", {"start": v(0.95, -0.73) * mm, "end": v(0.88, -0.72) * mm});
            skLineSegment(sketch, "E1123", {"start": v(0.88, -0.72) * mm, "end": v(0.82, -0.72) * mm});
            skLineSegment(sketch, "E1124", {"start": v(0.82, -0.72) * mm, "end": v(0.77, -0.71) * mm});
            skLineSegment(sketch, "E1125", {"start": v(0.77, -0.71) * mm, "end": v(0.74, -0.7) * mm});
            skLineSegment(sketch, "E1126", {"start": v(0.74, -0.7) * mm, "end": v(0.71, -0.7) * mm});
            skLineSegment(sketch, "E1127", {"start": v(0.71, -0.7) * mm, "end": v(0.71, -1.07) * mm});
            skLineSegment(sketch, "E1128", {"start": v(0.71, -1.07) * mm, "end": v(0.76, -1.13) * mm});
            skLineSegment(sketch, "E1129", {"start": v(0.76, -1.13) * mm, "end": v(0.79, -1.16) * mm});
            skLineSegment(sketch, "E1130", {"start": v(0.79, -1.16) * mm, "end": v(0.82, -1.2) * mm});
            skLineSegment(sketch, "E1131", {"start": v(0.82, -1.2) * mm, "end": v(0.85, -1.22) * mm});
            skLineSegment(sketch, "E1132", {"start": v(0.85, -1.22) * mm, "end": v(0.89, -1.25) * mm});
            skLineSegment(sketch, "E1133", {"start": v(0.89, -1.25) * mm, "end": v(0.93, -1.28) * mm});
            skLineSegment(sketch, "E1134", {"start": v(0.93, -1.28) * mm, "end": v(0.98, -1.33) * mm});
            skLineSegment(sketch, "E1135", {"start": v(0.98, -1.33) * mm, "end": v(1.04, -1.38) * mm});
            skLineSegment(sketch, "E1136", {"start": v(1.04, -1.38) * mm, "end": v(1.1, -1.44) * mm});
            skLineSegment(sketch, "E1137", {"start": v(1.1, -1.44) * mm, "end": v(1.16, -1.5) * mm});
            skLineSegment(sketch, "E1138", {"start": v(1.16, -1.5) * mm, "end": v(1.21, -1.54) * mm});
            skLineSegment(sketch, "E1139", {"start": v(1.21, -1.54) * mm, "end": v(1.27, -1.59) * mm});
            skLineSegment(sketch, "E1140", {"start": v(1.27, -1.59) * mm, "end": v(1.3, -1.62) * mm});
            skLineSegment(sketch, "E1141", {"start": v(1.3, -1.62) * mm, "end": v(1.33, -1.64) * mm});
            skLineSegment(sketch, "E1142", {"start": v(1.33, -1.64) * mm, "end": v(1.37, -1.67) * mm});
            skLineSegment(sketch, "E1143", {"start": v(1.37, -1.67) * mm, "end": v(1.4, -1.7) * mm});
            skLineSegment(sketch, "E1144", {"start": v(1.4, -1.7) * mm, "end": v(1.44, -1.72) * mm});
            skLineSegment(sketch, "E1145", {"start": v(1.44, -1.72) * mm, "end": v(1.47, -1.74) * mm});
            skLineSegment(sketch, "E1146", {"start": v(1.47, -1.74) * mm, "end": v(1.52, -1.77) * mm});
            skLineSegment(sketch, "E1147", {"start": v(1.52, -1.77) * mm, "end": v(1.58, -1.8) * mm});
            skLineSegment(sketch, "E1148", {"start": v(1.58, -1.8) * mm, "end": v(1.63, -1.84) * mm});
            skLineSegment(sketch, "E1149", {"start": v(1.63, -1.84) * mm, "end": v(1.68, -1.87) * mm});
            skLineSegment(sketch, "E1150", {"start": v(1.68, -1.87) * mm, "end": v(1.73, -1.9) * mm});
            skLineSegment(sketch, "E1151", {"start": v(1.73, -1.9) * mm, "end": v(1.77, -1.92) * mm});
            skLineSegment(sketch, "E1152", {"start": v(1.77, -1.92) * mm, "end": v(1.79, -1.93) * mm});
            skLineSegment(sketch, "E1153", {"start": v(1.79, -1.93) * mm, "end": v(1.84, -1.97) * mm});
            skLineSegment(sketch, "E1154", {"start": v(1.84, -1.97) * mm, "end": v(1.92, -2) * mm});
            skLineSegment(sketch, "E1155", {"start": v(1.92, -2) * mm, "end": v(2, -2.05) * mm});
            skLineSegment(sketch, "E1156", {"start": v(2, -2.05) * mm, "end": v(2.1, -2.1) * mm});
            skLineSegment(sketch, "E1157", {"start": v(2.1, -2.1) * mm, "end": v(2.16, -2.13) * mm});
            skLineSegment(sketch, "E1158", {"start": v(2.16, -2.13) * mm, "end": v(2.23, -2.16) * mm});
            skLineSegment(sketch, "E1159", {"start": v(2.23, -2.16) * mm, "end": v(2.3, -2.2) * mm});
            skLineSegment(sketch, "E1160", {"start": v(2.3, -2.2) * mm, "end": v(2.38, -2.23) * mm});
            skLineSegment(sketch, "E1161", {"start": v(2.38, -2.23) * mm, "end": v(2.45, -2.26) * mm});
            skLineSegment(sketch, "E1162", {"start": v(2.45, -2.26) * mm, "end": v(2.53, -2.3) * mm});
            skLineSegment(sketch, "E1163", {"start": v(2.53, -2.3) * mm, "end": v(2.6, -2.32) * mm});
            skLineSegment(sketch, "E1164", {"start": v(2.6, -2.32) * mm, "end": v(2.68, -2.35) * mm});
            skLineSegment(sketch, "E1165", {"start": v(2.68, -2.35) * mm, "end": v(2.74, -2.38) * mm});
            skLineSegment(sketch, "E1166", {"start": v(2.74, -2.38) * mm, "end": v(2.81, -2.4) * mm});
            skLineSegment(sketch, "E1167", {"start": v(2.81, -2.4) * mm, "end": v(2.87, -2.43) * mm});
            skLineSegment(sketch, "E1168", {"start": v(2.87, -2.43) * mm, "end": v(2.92, -2.45) * mm});
            skLineSegment(sketch, "E1169", {"start": v(2.92, -2.45) * mm, "end": v(3.03, -2.49) * mm});
            skLineSegment(sketch, "E1170", {"start": v(3.03, -2.49) * mm, "end": v(3.15, -2.52) * mm});
            skLineSegment(sketch, "E1171", {"start": v(3.15, -2.52) * mm, "end": v(3.2, -2.54) * mm});
            skLineSegment(sketch, "E1172", {"start": v(3.2, -2.54) * mm, "end": v(3.25, -2.55) * mm});
            skLineSegment(sketch, "E1173", {"start": v(3.25, -2.55) * mm, "end": v(3.3, -2.57) * mm});
            skLineSegment(sketch, "E1174", {"start": v(3.3, -2.57) * mm, "end": v(3.33, -2.58) * mm});
            skLineSegment(sketch, "E1175", {"start": v(3.33, -2.58) * mm, "end": v(3.37, -2.6) * mm});
            skLineSegment(sketch, "E1176", {"start": v(3.37, -2.6) * mm, "end": v(3.44, -2.6) * mm});
            skLineSegment(sketch, "E1177", {"start": v(3.44, -2.6) * mm, "end": v(3.52, -2.63) * mm});
            skLineSegment(sketch, "E1178", {"start": v(3.52, -2.63) * mm, "end": v(3.6, -2.64) * mm});
            skLineSegment(sketch, "E1179", {"start": v(3.6, -2.64) * mm, "end": v(3.7, -2.66) * mm});
            skLineSegment(sketch, "E1180", {"start": v(3.7, -2.66) * mm, "end": v(3.77, -2.67) * mm});
            skLineSegment(sketch, "E1181", {"start": v(3.77, -2.67) * mm, "end": v(3.84, -2.68) * mm});
            skLineSegment(sketch, "E1182", {"start": v(3.84, -2.68) * mm, "end": v(3.9, -2.69) * mm});
            skLineSegment(sketch, "E1183", {"start": v(3.9, -2.69) * mm, "end": v(3.91, -2.69) * mm});
            skLineSegment(sketch, "E1184", {"start": v(3.91, -2.69) * mm, "end": v(3.92, -2.68) * mm});
            skLineSegment(sketch, "E1185", {"start": v(4.65, -2.6) * mm, "end": v(4.76, -2.58) * mm});
            skLineSegment(sketch, "E1186", {"start": v(4.76, -2.58) * mm, "end": v(4.84, -2.57) * mm});
            skLineSegment(sketch, "E1187", {"start": v(4.84, -2.57) * mm, "end": v(4.9, -2.56) * mm});
            skLineSegment(sketch, "E1188", {"start": v(4.9, -2.56) * mm, "end": v(4.96, -2.55) * mm});
            skLineSegment(sketch, "E1189", {"start": v(4.96, -2.55) * mm, "end": v(5, -2.55) * mm});
            skLineSegment(sketch, "E1190", {"start": v(5, -2.55) * mm, "end": v(5.04, -2.54) * mm});
            skLineSegment(sketch, "E1191", {"start": v(5.04, -2.54) * mm, "end": v(5.07, -2.54) * mm});
            skLineSegment(sketch, "E1192", {"start": v(5.07, -2.54) * mm, "end": v(5.1, -2.53) * mm});
            skLineSegment(sketch, "E1193", {"start": v(5.1, -2.53) * mm, "end": v(5.13, -2.52) * mm});
            skLineSegment(sketch, "E1194", {"start": v(5.13, -2.52) * mm, "end": v(5.17, -2.51) * mm});
            skLineSegment(sketch, "E1195", {"start": v(5.17, -2.51) * mm, "end": v(5.23, -2.5) * mm});
            skLineSegment(sketch, "E1196", {"start": v(5.23, -2.5) * mm, "end": v(5.28, -2.5) * mm});
            skLineSegment(sketch, "E1197", {"start": v(5.28, -2.5) * mm, "end": v(5.37, -2.47) * mm});
            skLineSegment(sketch, "E1198", {"start": v(5.37, -2.47) * mm, "end": v(5.48, -2.44) * mm});
            skLineSegment(sketch, "E1199", {"start": v(5.48, -2.44) * mm, "end": v(5.62, -2.4) * mm});
            skLineSegment(sketch, "E1200", {"start": v(5.62, -2.4) * mm, "end": v(5.81, -2.34) * mm});
            skLineSegment(sketch, "E1201", {"start": v(5.81, -2.34) * mm, "end": v(5.88, -2.31) * mm});
            skLineSegment(sketch, "E1202", {"start": v(5.88, -2.31) * mm, "end": v(5.95, -2.29) * mm});
            skLineSegment(sketch, "E1203", {"start": v(5.95, -2.29) * mm, "end": v(6.01, -2.26) * mm});
            skLineSegment(sketch, "E1204", {"start": v(6.01, -2.26) * mm, "end": v(6.08, -2.23) * mm});
            skLineSegment(sketch, "E1205", {"start": v(6.08, -2.23) * mm, "end": v(6.13, -2.2) * mm});
            skLineSegment(sketch, "E1206", {"start": v(6.13, -2.2) * mm, "end": v(6.17, -2.19) * mm});
            skLineSegment(sketch, "E1207", {"start": v(6.17, -2.19) * mm, "end": v(6.2, -2.17) * mm});
            skLineSegment(sketch, "E1208", {"start": v(6.2, -2.17) * mm, "end": v(6.21, -2.16) * mm});
            skLineSegment(sketch, "E1209", {"start": v(6.21, -2.16) * mm, "end": v(6.2, -2.14) * mm});
            skLineSegment(sketch, "E1210", {"start": v(6.2, -2.14) * mm, "end": v(6.18, -2.12) * mm});
            skLineSegment(sketch, "E1211", {"start": v(6.18, -2.12) * mm, "end": v(6.15, -2.08) * mm});
            skLineSegment(sketch, "E1212", {"start": v(6.15, -2.08) * mm, "end": v(6.1, -2.04) * mm});
            skLineSegment(sketch, "E1213", {"start": v(6.1, -2.04) * mm, "end": v(6.06, -2) * mm});
            skLineSegment(sketch, "E1214", {"start": v(6.06, -2) * mm, "end": v(6.01, -1.94) * mm});
            skLineSegment(sketch, "E1215", {"start": v(6.01, -1.94) * mm, "end": v(5.96, -1.9) * mm});
            skLineSegment(sketch, "E1216", {"start": v(5.96, -1.9) * mm, "end": v(5.91, -1.86) * mm});
            skLineSegment(sketch, "E1217", {"start": v(5.91, -1.86) * mm, "end": v(5.73, -1.72) * mm});
            skLineSegment(sketch, "E1218", {"start": v(5.73, -1.72) * mm, "end": v(5.55, -1.6) * mm});
            skLineSegment(sketch, "E1219", {"start": v(5.55, -1.6) * mm, "end": v(5.38, -1.5) * mm});
            skLineSegment(sketch, "E1220", {"start": v(5.38, -1.5) * mm, "end": v(5.25, -1.44) * mm});
            skLineSegment(sketch, "E1221", {"start": v(5.25, -1.44) * mm, "end": v(5.19, -1.42) * mm});
            skLineSegment(sketch, "E1222", {"start": v(5.19, -1.42) * mm, "end": v(5.13, -1.41) * mm});
            skLineSegment(sketch, "E1223", {"start": v(5.13, -1.41) * mm, "end": v(5.05, -1.42) * mm});
            skLineSegment(sketch, "E1224", {"start": v(5.05, -1.42) * mm, "end": v(4.94, -1.44) * mm});
            skLineSegment(sketch, "E1225", {"start": v(4.94, -1.44) * mm, "end": v(4.86, -1.45) * mm});
            skLineSegment(sketch, "E1226", {"start": v(4.86, -1.45) * mm, "end": v(4.77, -1.46) * mm});
            skLineSegment(sketch, "E1227", {"start": v(4.77, -1.46) * mm, "end": v(4.67, -1.46) * mm});
            skLineSegment(sketch, "E1228", {"start": v(4.67, -1.46) * mm, "end": v(4.53, -1.46) * mm});
            skLineSegment(sketch, "E1229", {"start": v(4.53, -1.46) * mm, "end": v(4.42, -1.46) * mm});
            skLineSegment(sketch, "E1230", {"start": v(4.42, -1.46) * mm, "end": v(4.34, -1.46) * mm});
            skLineSegment(sketch, "E1231", {"start": v(4.34, -1.46) * mm, "end": v(4.28, -1.46) * mm});
            skLineSegment(sketch, "E1232", {"start": v(4.28, -1.46) * mm, "end": v(4.22, -1.45) * mm});
            skLineSegment(sketch, "E1233", {"start": v(4.22, -1.45) * mm, "end": v(4.17, -1.43) * mm});
            skLineSegment(sketch, "E1234", {"start": v(4.17, -1.43) * mm, "end": v(4.1, -1.41) * mm});
            skLineSegment(sketch, "E1235", {"start": v(4.1, -1.41) * mm, "end": v(4.04, -1.39) * mm});
            skLineSegment(sketch, "E1236", {"start": v(4.04, -1.39) * mm, "end": v(3.95, -1.35) * mm});
            skLineSegment(sketch, "E1237", {"start": v(3.95, -1.35) * mm, "end": v(3.78, -1.28) * mm});
            skLineSegment(sketch, "E1238", {"start": v(3.78, -1.28) * mm, "end": v(3.64, -1.23) * mm});
            skLineSegment(sketch, "E1239", {"start": v(3.64, -1.23) * mm, "end": v(3.52, -1.2) * mm});
            skLineSegment(sketch, "E1240", {"start": v(3.52, -1.2) * mm, "end": v(3.4, -1.17) * mm});
            skLineSegment(sketch, "E1241", {"start": v(3.4, -1.17) * mm, "end": v(3.27, -1.16) * mm});
            skLineSegment(sketch, "E1242", {"start": v(3.27, -1.16) * mm, "end": v(3.15, -1.16) * mm});
            skLineSegment(sketch, "E1243", {"start": v(3.15, -1.16) * mm, "end": v(3.04, -1.16) * mm});
            skLineSegment(sketch, "E1244", {"start": v(3.04, -1.16) * mm, "end": v(3.2, -1.3) * mm});
            skLineSegment(sketch, "E1245", {"start": v(3.2, -1.3) * mm, "end": v(3.37, -1.43) * mm});
            skLineSegment(sketch, "E1246", {"start": v(3.37, -1.43) * mm, "end": v(3.53, -1.57) * mm});
            skLineSegment(sketch, "E1247", {"start": v(3.53, -1.57) * mm, "end": v(3.67, -1.7) * mm});
            skLineSegment(sketch, "E1248", {"start": v(3.67, -1.7) * mm, "end": v(3.77, -1.8) * mm});
            skLineSegment(sketch, "E1249", {"start": v(3.77, -1.8) * mm, "end": v(3.83, -1.88) * mm});
            skLineSegment(sketch, "E1250", {"start": v(3.83, -1.88) * mm, "end": v(3.9, -1.97) * mm});
            skLineSegment(sketch, "E1251", {"start": v(3.9, -1.97) * mm, "end": v(3.97, -2.08) * mm});
            skLineSegment(sketch, "E1252", {"start": v(3.97, -2.08) * mm, "end": v(4.04, -2.2) * mm});
            skLineSegment(sketch, "E1253", {"start": v(4.04, -2.2) * mm, "end": v(4.1, -2.3) * mm});
            skLineSegment(sketch, "E1254", {"start": v(4.1, -2.3) * mm, "end": v(4.16, -2.42) * mm});
            skLineSegment(sketch, "E1255", {"start": v(4.16, -2.42) * mm, "end": v(4.2, -2.5) * mm});
            skLineSegment(sketch, "E1256", {"start": v(4.2, -2.5) * mm, "end": v(4.24, -2.58) * mm});
            skLineSegment(sketch, "E1257", {"start": v(4.24, -2.58) * mm, "end": v(4.26, -2.64) * mm});
            skLineSegment(sketch, "E1258", {"start": v(4.26, -2.64) * mm, "end": v(4.34, -2.63) * mm});
            skLineSegment(sketch, "E1259", {"start": v(4.34, -2.63) * mm, "end": v(4.4, -2.62) * mm});
            skLineSegment(sketch, "E1260", {"start": v(4.4, -2.62) * mm, "end": v(4.47, -2.62) * mm});
            skLineSegment(sketch, "E1261", {"start": v(4.47, -2.62) * mm, "end": v(4.56, -2.6) * mm});
            skLineSegment(sketch, "E1262", {"start": v(4.56, -2.6) * mm, "end": v(4.65, -2.6) * mm});
            skLineSegment(sketch, "E1263", {"start": v(-4.98, -2.14) * mm, "end": v(-4.95, -2.1) * mm});
            skLineSegment(sketch, "E1264", {"start": v(-4.95, -2.1) * mm, "end": v(-4.92, -2.06) * mm});
            skLineSegment(sketch, "E1265", {"start": v(-4.92, -2.06) * mm, "end": v(-4.88, -2) * mm});
            skLineSegment(sketch, "E1266", {"start": v(-4.88, -2) * mm, "end": v(-4.85, -1.96) * mm});
            skLineSegment(sketch, "E1267", {"start": v(-4.85, -1.96) * mm, "end": v(-4.82, -1.92) * mm});
            skLineSegment(sketch, "E1268", {"start": v(-4.82, -1.92) * mm, "end": v(-4.79, -1.87) * mm});
            skLineSegment(sketch, "E1269", {"start": v(-4.79, -1.87) * mm, "end": v(-4.76, -1.84) * mm});
            skLineSegment(sketch, "E1270", {"start": v(-4.76, -1.84) * mm, "end": v(-4.74, -1.81) * mm});
            skLineSegment(sketch, "E1271", {"start": v(-4.74, -1.81) * mm, "end": v(-4.72, -1.8) * mm});
            skLineSegment(sketch, "E1272", {"start": v(-4.72, -1.8) * mm, "end": v(-4.7, -1.76) * mm});
            skLineSegment(sketch, "E1273", {"start": v(-4.7, -1.76) * mm, "end": v(-4.67, -1.73) * mm});
            skLineSegment(sketch, "E1274", {"start": v(-4.67, -1.73) * mm, "end": v(-4.64, -1.7) * mm});
            skLineSegment(sketch, "E1275", {"start": v(-4.64, -1.7) * mm, "end": v(-4.57, -1.61) * mm});
            skLineSegment(sketch, "E1276", {"start": v(-4.57, -1.61) * mm, "end": v(-4.5, -1.53) * mm});
            skLineSegment(sketch, "E1277", {"start": v(-4.5, -1.53) * mm, "end": v(-4.41, -1.44) * mm});
            skLineSegment(sketch, "E1278", {"start": v(-4.41, -1.44) * mm, "end": v(-4.33, -1.36) * mm});
            skLineSegment(sketch, "E1279", {"start": v(-4.33, -1.36) * mm, "end": v(-4.25, -1.28) * mm});
            skLineSegment(sketch, "E1280", {"start": v(-4.25, -1.28) * mm, "end": v(-4.17, -1.22) * mm});
            skLineSegment(sketch, "E1281", {"start": v(-4.17, -1.22) * mm, "end": v(-4.1, -1.16) * mm});
            skLineSegment(sketch, "E1282", {"start": v(-4.1, -1.16) * mm, "end": v(-4.05, -1.12) * mm});
            skLineSegment(sketch, "E1283", {"start": v(-4.05, -1.12) * mm, "end": v(-4.02, -1.1) * mm});
            skLineSegment(sketch, "E1284", {"start": v(-4.02, -1.1) * mm, "end": v(-3.98, -1.07) * mm});
            skLineSegment(sketch, "E1285", {"start": v(-3.98, -1.07) * mm, "end": v(-3.93, -1.03) * mm});
            skLineSegment(sketch, "E1286", {"start": v(-3.93, -1.03) * mm, "end": v(-3.88, -1) * mm});
            skLineSegment(sketch, "E1287", {"start": v(-3.88, -1) * mm, "end": v(-3.76, -0.9) * mm});
            skLineSegment(sketch, "E1288", {"start": v(-3.76, -0.9) * mm, "end": v(-3.98, -0.9) * mm});
            skLineSegment(sketch, "E1289", {"start": v(-3.98, -0.9) * mm, "end": v(-4.08, -0.9) * mm});
            skLineSegment(sketch, "E1290", {"start": v(-4.08, -0.9) * mm, "end": v(-4.18, -0.9) * mm});
            skLineSegment(sketch, "E1291", {"start": v(-4.18, -0.9) * mm, "end": v(-4.28, -0.89) * mm});
            skLineSegment(sketch, "E1292", {"start": v(-4.28, -0.89) * mm, "end": v(-4.36, -0.88) * mm});
            skLineSegment(sketch, "E1293", {"start": v(-4.36, -0.88) * mm, "end": v(-4.44, -0.88) * mm});
            skLineSegment(sketch, "E1294", {"start": v(-4.44, -0.88) * mm, "end": v(-4.56, -0.87) * mm});
            skLineSegment(sketch, "E1295", {"start": v(-4.56, -0.87) * mm, "end": v(-4.69, -0.87) * mm});
            skLineSegment(sketch, "E1296", {"start": v(-4.69, -0.87) * mm, "end": v(-4.82, -0.87) * mm});
            skLineSegment(sketch, "E1297", {"start": v(-4.82, -0.87) * mm, "end": v(-4.97, -0.87) * mm});
            skLineSegment(sketch, "E1298", {"start": v(-4.97, -0.87) * mm, "end": v(-5.08, -0.87) * mm});
            skLineSegment(sketch, "E1299", {"start": v(-5.08, -0.87) * mm, "end": v(-5.18, -0.88) * mm});
            skLineSegment(sketch, "E1300", {"start": v(-5.18, -0.88) * mm, "end": v(-5.25, -0.9) * mm});
            skLineSegment(sketch, "E1301", {"start": v(-5.25, -0.9) * mm, "end": v(-5.32, -0.92) * mm});
            skLineSegment(sketch, "E1302", {"start": v(-5.32, -0.92) * mm, "end": v(-5.39, -0.96) * mm});
            skLineSegment(sketch, "E1303", {"start": v(-5.39, -0.96) * mm, "end": v(-5.46, -1) * mm});
            skLineSegment(sketch, "E1304", {"start": v(-5.46, -1) * mm, "end": v(-5.55, -1.07) * mm});
            skLineSegment(sketch, "E1305", {"start": v(-5.55, -1.07) * mm, "end": v(-5.7, -1.18) * mm});
            skLineSegment(sketch, "E1306", {"start": v(-5.7, -1.18) * mm, "end": v(-5.83, -1.26) * mm});
            skLineSegment(sketch, "E1307", {"start": v(-5.83, -1.26) * mm, "end": v(-5.95, -1.3) * mm});
            skLineSegment(sketch, "E1308", {"start": v(-5.95, -1.3) * mm, "end": v(-6.08, -1.33) * mm});
            skLineSegment(sketch, "E1309", {"start": v(-6.08, -1.33) * mm, "end": v(-6.25, -1.38) * mm});
            skLineSegment(sketch, "E1310", {"start": v(-6.25, -1.38) * mm, "end": v(-6.43, -1.44) * mm});
            skLineSegment(sketch, "E1311", {"start": v(-6.43, -1.44) * mm, "end": v(-6.6, -1.52) * mm});
            skLineSegment(sketch, "E1312", {"start": v(-6.6, -1.52) * mm, "end": v(-6.76, -1.63) * mm});
            skLineSegment(sketch, "E1313", {"start": v(-6.76, -1.63) * mm, "end": v(-6.8, -1.66) * mm});
            skLineSegment(sketch, "E1314", {"start": v(-6.8, -1.66) * mm, "end": v(-6.85, -1.7) * mm});
            skLineSegment(sketch, "E1315", {"start": v(-6.85, -1.7) * mm, "end": v(-6.89, -1.73) * mm});
            skLineSegment(sketch, "E1316", {"start": v(-6.89, -1.73) * mm, "end": v(-6.92, -1.75) * mm});
            skLineSegment(sketch, "E1317", {"start": v(-6.92, -1.75) * mm, "end": v(-6.94, -1.77) * mm});
            skLineSegment(sketch, "E1318", {"start": v(-6.94, -1.77) * mm, "end": v(-6.96, -1.78) * mm});
            skLineSegment(sketch, "E1319", {"start": v(-6.96, -1.78) * mm, "end": v(-6.97, -1.8) * mm});
            skLineSegment(sketch, "E1320", {"start": v(-6.97, -1.8) * mm, "end": v(-6.98, -1.8) * mm});
            skLineSegment(sketch, "E1321", {"start": v(-6.98, -1.8) * mm, "end": v(-6.97, -1.8) * mm});
            skLineSegment(sketch, "E1322", {"start": v(-6.97, -1.8) * mm, "end": v(-6.95, -1.81) * mm});
            skLineSegment(sketch, "E1323", {"start": v(-6.95, -1.81) * mm, "end": v(-6.92, -1.82) * mm});
            skLineSegment(sketch, "E1324", {"start": v(-6.92, -1.82) * mm, "end": v(-6.88, -1.84) * mm});
            skLineSegment(sketch, "E1325", {"start": v(-6.88, -1.84) * mm, "end": v(-6.84, -1.85) * mm});
            skLineSegment(sketch, "E1326", {"start": v(-6.84, -1.85) * mm, "end": v(-6.8, -1.86) * mm});
            skLineSegment(sketch, "E1327", {"start": v(-6.8, -1.86) * mm, "end": v(-6.75, -1.88) * mm});
            skLineSegment(sketch, "E1328", {"start": v(-6.75, -1.88) * mm, "end": v(-6.72, -1.89) * mm});
            skLineSegment(sketch, "E1329", {"start": v(-6.72, -1.89) * mm, "end": v(-6.65, -1.91) * mm});
            skLineSegment(sketch, "E1330", {"start": v(-6.65, -1.91) * mm, "end": v(-6.53, -1.95) * mm});
            skLineSegment(sketch, "E1331", {"start": v(-6.53, -1.95) * mm, "end": v(-6.36, -2) * mm});
            skLineSegment(sketch, "E1332", {"start": v(-6.36, -2) * mm, "end": v(-6.12, -2.06) * mm});
            skLineSegment(sketch, "E1333", {"start": v(-6.12, -2.06) * mm, "end": v(-5.99, -2.1) * mm});
            skLineSegment(sketch, "E1334", {"start": v(-5.99, -2.1) * mm, "end": v(-5.88, -2.11) * mm});
            skLineSegment(sketch, "E1335", {"start": v(-5.88, -2.11) * mm, "end": v(-5.75, -2.13) * mm});
            skLineSegment(sketch, "E1336", {"start": v(-5.75, -2.13) * mm, "end": v(-5.58, -2.15) * mm});
            skLineSegment(sketch, "E1337", {"start": v(-5.58, -2.15) * mm, "end": v(-5.48, -2.16) * mm});
            skLineSegment(sketch, "E1338", {"start": v(-5.48, -2.16) * mm, "end": v(-5.39, -2.18) * mm});
            skLineSegment(sketch, "E1339", {"start": v(-5.39, -2.18) * mm, "end": v(-5.31, -2.18) * mm});
            skLineSegment(sketch, "E1340", {"start": v(-5.31, -2.18) * mm, "end": v(-5.27, -2.2) * mm});
            skLineSegment(sketch, "E1341", {"start": v(-5.27, -2.2) * mm, "end": v(-5.24, -2.2) * mm});
            skLineSegment(sketch, "E1342", {"start": v(-5.24, -2.2) * mm, "end": v(-5.2, -2.2) * mm});
            skLineSegment(sketch, "E1343", {"start": v(-5.2, -2.2) * mm, "end": v(-5.16, -2.2) * mm});
            skLineSegment(sketch, "E1344", {"start": v(-5.16, -2.2) * mm, "end": v(-5.12, -2.2) * mm});
            skLineSegment(sketch, "E1345", {"start": v(-5.12, -2.2) * mm, "end": v(-5.03, -2.2) * mm});
            skLineSegment(sketch, "E1346", {"start": v(-5.03, -2.2) * mm, "end": v(-4.98, -2.14) * mm});
            skLineSegment(sketch, "E1347", {"start": v(-4.35, -2.1) * mm, "end": v(-4.17, -2.07) * mm});
            skLineSegment(sketch, "E1348", {"start": v(-4.17, -2.07) * mm, "end": v(-3.97, -2.04) * mm});
            skLineSegment(sketch, "E1349", {"start": v(-3.97, -2.04) * mm, "end": v(-3.76, -2) * mm});
            skLineSegment(sketch, "E1350", {"start": v(-3.76, -2) * mm, "end": v(-3.58, -1.97) * mm});
            skLineSegment(sketch, "E1351", {"start": v(-3.58, -1.97) * mm, "end": v(-3.5, -1.95) * mm});
            skLineSegment(sketch, "E1352", {"start": v(-3.5, -1.95) * mm, "end": v(-3.38, -1.92) * mm});
            skLineSegment(sketch, "E1353", {"start": v(-3.38, -1.92) * mm, "end": v(-3.25, -1.88) * mm});
            skLineSegment(sketch, "E1354", {"start": v(-3.25, -1.88) * mm, "end": v(-3.1, -1.84) * mm});
            skLineSegment(sketch, "E1355", {"start": v(-3.1, -1.84) * mm, "end": v(-2.95, -1.79) * mm});
            skLineSegment(sketch, "E1356", {"start": v(-2.95, -1.79) * mm, "end": v(-2.8, -1.74) * mm});
            skLineSegment(sketch, "E1357", {"start": v(-2.8, -1.74) * mm, "end": v(-2.66, -1.69) * mm});
            skLineSegment(sketch, "E1358", {"start": v(-2.66, -1.69) * mm, "end": v(-2.53, -1.64) * mm});
            skLineSegment(sketch, "E1359", {"start": v(-2.53, -1.64) * mm, "end": v(-2.4, -1.58) * mm});
            skLineSegment(sketch, "E1360", {"start": v(-2.4, -1.58) * mm, "end": v(-2.22, -1.5) * mm});
            skLineSegment(sketch, "E1361", {"start": v(-2.22, -1.5) * mm, "end": v(-2.03, -1.4) * mm});
            skLineSegment(sketch, "E1362", {"start": v(-2.03, -1.4) * mm, "end": v(-1.83, -1.28) * mm});
            skLineSegment(sketch, "E1363", {"start": v(-1.83, -1.28) * mm, "end": v(-1.64, -1.17) * mm});
            skLineSegment(sketch, "E1364", {"start": v(-1.64, -1.17) * mm, "end": v(-1.47, -1.07) * mm});
            skLineSegment(sketch, "E1365", {"start": v(-1.47, -1.07) * mm, "end": v(-1.34, -0.98) * mm});
            skLineSegment(sketch, "E1366", {"start": v(-1.34, -0.98) * mm, "end": v(-1.25, -0.92) * mm});
            skLineSegment(sketch, "E1367", {"start": v(-1.25, -0.92) * mm, "end": v(-1.2, -0.87) * mm});
            skLineSegment(sketch, "E1368", {"start": v(-1.2, -0.87) * mm, "end": v(-1.2, -0.57) * mm});
            skLineSegment(sketch, "E1369", {"start": v(-1.2, -0.57) * mm, "end": v(-1.32, -0.54) * mm});
            skLineSegment(sketch, "E1370", {"start": v(-1.32, -0.54) * mm, "end": v(-1.5, -0.5) * mm});
            skLineSegment(sketch, "E1371", {"start": v(-1.5, -0.5) * mm, "end": v(-1.62, -0.48) * mm});
            skLineSegment(sketch, "E1372", {"start": v(-1.62, -0.48) * mm, "end": v(-1.73, -0.47) * mm});
            skLineSegment(sketch, "E1373", {"start": v(-1.73, -0.47) * mm, "end": v(-1.85, -0.47) * mm});
            skLineSegment(sketch, "E1374", {"start": v(-1.85, -0.47) * mm, "end": v(-2.01, -0.47) * mm});
            skLineSegment(sketch, "E1375", {"start": v(-2.01, -0.47) * mm, "end": v(-2.19, -0.5) * mm});
            skLineSegment(sketch, "E1376", {"start": v(-2.19, -0.5) * mm, "end": v(-2.36, -0.52) * mm});
            skLineSegment(sketch, "E1377", {"start": v(-2.36, -0.52) * mm, "end": v(-2.52, -0.56) * mm});
            skLineSegment(sketch, "E1378", {"start": v(-2.52, -0.56) * mm, "end": v(-2.57, -0.57) * mm});
            skLineSegment(sketch, "E1379", {"start": v(-2.57, -0.57) * mm, "end": v(-2.63, -0.6) * mm});
            skLineSegment(sketch, "E1380", {"start": v(-2.63, -0.6) * mm, "end": v(-2.7, -0.62) * mm});
            skLineSegment(sketch, "E1381", {"start": v(-2.7, -0.62) * mm, "end": v(-2.77, -0.65) * mm});
            skLineSegment(sketch, "E1382", {"start": v(-2.77, -0.65) * mm, "end": v(-2.83, -0.68) * mm});
            skLineSegment(sketch, "E1383", {"start": v(-2.83, -0.68) * mm, "end": v(-2.9, -0.7) * mm});
            skLineSegment(sketch, "E1384", {"start": v(-2.9, -0.7) * mm, "end": v(-2.95, -0.73) * mm});
            skLineSegment(sketch, "E1385", {"start": v(-2.95, -0.73) * mm, "end": v(-2.98, -0.74) * mm});
            skLineSegment(sketch, "E1386", {"start": v(-2.98, -0.74) * mm, "end": v(-3.02, -0.76) * mm});
            skLineSegment(sketch, "E1387", {"start": v(-3.02, -0.76) * mm, "end": v(-3.07, -0.79) * mm});
            skLineSegment(sketch, "E1388", {"start": v(-3.07, -0.79) * mm, "end": v(-3.14, -0.82) * mm});
            skLineSegment(sketch, "E1389", {"start": v(-3.14, -0.82) * mm, "end": v(-3.2, -0.87) * mm});
            skLineSegment(sketch, "E1390", {"start": v(-3.2, -0.87) * mm, "end": v(-3.27, -0.91) * mm});
            skLineSegment(sketch, "E1391", {"start": v(-3.27, -0.91) * mm, "end": v(-3.34, -0.96) * mm});
            skLineSegment(sketch, "E1392", {"start": v(-3.34, -0.96) * mm, "end": v(-3.4, -1) * mm});
            skLineSegment(sketch, "E1393", {"start": v(-3.4, -1) * mm, "end": v(-3.45, -1.04) * mm});
            skLineSegment(sketch, "E1394", {"start": v(-3.45, -1.04) * mm, "end": v(-3.67, -1.21) * mm});
            skLineSegment(sketch, "E1395", {"start": v(-3.67, -1.21) * mm, "end": v(-3.87, -1.37) * mm});
            skLineSegment(sketch, "E1396", {"start": v(-3.87, -1.37) * mm, "end": v(-4.03, -1.52) * mm});
            skLineSegment(sketch, "E1397", {"start": v(-4.03, -1.52) * mm, "end": v(-4.16, -1.64) * mm});
            skLineSegment(sketch, "E1398", {"start": v(-4.16, -1.64) * mm, "end": v(-4.32, -1.8) * mm});
            skLineSegment(sketch, "E1399", {"start": v(-4.32, -1.8) * mm, "end": v(-4.44, -1.9) * mm});
            skLineSegment(sketch, "E1400", {"start": v(-4.44, -1.9) * mm, "end": v(-4.51, -1.99) * mm});
            skLineSegment(sketch, "E1401", {"start": v(-4.51, -1.99) * mm, "end": v(-4.56, -2.04) * mm});
            skLineSegment(sketch, "E1402", {"start": v(-4.56, -2.04) * mm, "end": v(-4.6, -2.1) * mm});
            skLineSegment(sketch, "E1403", {"start": v(-4.6, -2.1) * mm, "end": v(-4.54, -2.1) * mm});
            skLineSegment(sketch, "E1404", {"start": v(-4.54, -2.1) * mm, "end": v(-4.5, -2.1) * mm});
            skLineSegment(sketch, "E1405", {"start": v(-4.5, -2.1) * mm, "end": v(-4.46, -2.1) * mm});
            skLineSegment(sketch, "E1406", {"start": v(-4.46, -2.1) * mm, "end": v(-4.4, -2.1) * mm});
            skLineSegment(sketch, "E1407", {"start": v(-4.4, -2.1) * mm, "end": v(-4.35, -2.1) * mm});
            skLineSegment(sketch, "E1408", {"start": v(8.73, -2.05) * mm, "end": v(8.73, -2) * mm});
            skLineSegment(sketch, "E1409", {"start": v(8.73, -2) * mm, "end": v(8.72, -1.92) * mm});
            skLineSegment(sketch, "E1410", {"start": v(8.72, -1.92) * mm, "end": v(8.7, -1.83) * mm});
            skLineSegment(sketch, "E1411", {"start": v(8.7, -1.83) * mm, "end": v(8.68, -1.74) * mm});
            skLineSegment(sketch, "E1412", {"start": v(8.68, -1.74) * mm, "end": v(8.65, -1.64) * mm});
            skLineSegment(sketch, "E1413", {"start": v(8.65, -1.64) * mm, "end": v(8.63, -1.55) * mm});
            skLineSegment(sketch, "E1414", {"start": v(8.63, -1.55) * mm, "end": v(8.6, -1.48) * mm});
            skLineSegment(sketch, "E1415", {"start": v(8.6, -1.48) * mm, "end": v(8.58, -1.43) * mm});
            skLineSegment(sketch, "E1416", {"start": v(8.58, -1.43) * mm, "end": v(8.51, -1.31) * mm});
            skLineSegment(sketch, "E1417", {"start": v(8.51, -1.31) * mm, "end": v(8.42, -1.2) * mm});
            skLineSegment(sketch, "E1418", {"start": v(8.42, -1.2) * mm, "end": v(8.32, -1.08) * mm});
            skLineSegment(sketch, "E1419", {"start": v(8.32, -1.08) * mm, "end": v(8.2, -0.99) * mm});
            skLineSegment(sketch, "E1420", {"start": v(8.2, -0.99) * mm, "end": v(8.14, -0.94) * mm});
            skLineSegment(sketch, "E1421", {"start": v(8.14, -0.94) * mm, "end": v(8.06, -0.9) * mm});
            skLineSegment(sketch, "E1422", {"start": v(8.06, -0.9) * mm, "end": v(7.96, -0.87) * mm});
            skLineSegment(sketch, "E1423", {"start": v(7.96, -0.87) * mm, "end": v(7.84, -0.84) * mm});
            skLineSegment(sketch, "E1424", {"start": v(7.84, -0.84) * mm, "end": v(7.75, -0.82) * mm});
            skLineSegment(sketch, "E1425", {"start": v(7.75, -0.82) * mm, "end": v(7.68, -0.81) * mm});
            skLineSegment(sketch, "E1426", {"start": v(7.68, -0.81) * mm, "end": v(7.6, -0.8) * mm});
            skLineSegment(sketch, "E1427", {"start": v(7.6, -0.8) * mm, "end": v(7.47, -0.8) * mm});
            skLineSegment(sketch, "E1428", {"start": v(7.47, -0.8) * mm, "end": v(7.34, -0.8) * mm});
            skLineSegment(sketch, "E1429", {"start": v(7.34, -0.8) * mm, "end": v(7.26, -0.81) * mm});
            skLineSegment(sketch, "E1430", {"start": v(7.26, -0.81) * mm, "end": v(7.2, -0.82) * mm});
            skLineSegment(sketch, "E1431", {"start": v(7.2, -0.82) * mm, "end": v(7.15, -0.83) * mm});
            skLineSegment(sketch, "E1432", {"start": v(7.15, -0.83) * mm, "end": v(6.93, -0.91) * mm});
            skLineSegment(sketch, "E1433", {"start": v(6.93, -0.91) * mm, "end": v(6.77, -1) * mm});
            skLineSegment(sketch, "E1434", {"start": v(6.77, -1) * mm, "end": v(6.73, -1.03) * mm});
            skLineSegment(sketch, "E1435", {"start": v(6.73, -1.03) * mm, "end": v(6.67, -1.07) * mm});
            skLineSegment(sketch, "E1436", {"start": v(6.67, -1.07) * mm, "end": v(6.6, -1.12) * mm});
            skLineSegment(sketch, "E1437", {"start": v(6.6, -1.12) * mm, "end": v(6.53, -1.17) * mm});
            skLineSegment(sketch, "E1438", {"start": v(6.53, -1.17) * mm, "end": v(6.46, -1.21) * mm});
            skLineSegment(sketch, "E1439", {"start": v(6.46, -1.21) * mm, "end": v(6.4, -1.25) * mm});
            skLineSegment(sketch, "E1440", {"start": v(6.4, -1.25) * mm, "end": v(6.35, -1.29) * mm});
            skLineSegment(sketch, "E1441", {"start": v(6.35, -1.29) * mm, "end": v(6.31, -1.31) * mm});
            skLineSegment(sketch, "E1442", {"start": v(6.31, -1.31) * mm, "end": v(6.24, -1.35) * mm});
            skLineSegment(sketch, "E1443", {"start": v(6.24, -1.35) * mm, "end": v(6.16, -1.4) * mm});
            skLineSegment(sketch, "E1444", {"start": v(6.16, -1.4) * mm, "end": v(6.08, -1.43) * mm});
            skLineSegment(sketch, "E1445", {"start": v(6.08, -1.43) * mm, "end": v(6.01, -1.45) * mm});
            skLineSegment(sketch, "E1446", {"start": v(6.01, -1.45) * mm, "end": v(5.98, -1.45) * mm});
            skLineSegment(sketch, "E1447", {"start": v(5.98, -1.45) * mm, "end": v(5.97, -1.46) * mm});
            skLineSegment(sketch, "E1448", {"start": v(5.97, -1.46) * mm, "end": v(5.96, -1.47) * mm});
            skLineSegment(sketch, "E1449", {"start": v(5.96, -1.47) * mm, "end": v(5.97, -1.47) * mm});
            skLineSegment(sketch, "E1450", {"start": v(5.97, -1.47) * mm, "end": v(5.98, -1.49) * mm});
            skLineSegment(sketch, "E1451", {"start": v(5.98, -1.49) * mm, "end": v(6.01, -1.5) * mm});
            skLineSegment(sketch, "E1452", {"start": v(6.01, -1.5) * mm, "end": v(6.05, -1.54) * mm});
            skLineSegment(sketch, "E1453", {"start": v(6.05, -1.54) * mm, "end": v(6.1, -1.58) * mm});
            skLineSegment(sketch, "E1454", {"start": v(6.1, -1.58) * mm, "end": v(6.2, -1.66) * mm});
            skLineSegment(sketch, "E1455", {"start": v(6.2, -1.66) * mm, "end": v(6.31, -1.77) * mm});
            skLineSegment(sketch, "E1456", {"start": v(6.31, -1.77) * mm, "end": v(6.43, -1.9) * mm});
            skLineSegment(sketch, "E1457", {"start": v(6.43, -1.9) * mm, "end": v(6.53, -2) * mm});
            skLineSegment(sketch, "E1458", {"start": v(6.53, -2) * mm, "end": v(6.57, -2.04) * mm});
            skLineSegment(sketch, "E1459", {"start": v(6.57, -2.04) * mm, "end": v(6.6, -2.06) * mm});
            skLineSegment(sketch, "E1460", {"start": v(6.6, -2.06) * mm, "end": v(6.6, -2.07) * mm});
            skLineSegment(sketch, "E1461", {"start": v(6.6, -2.07) * mm, "end": v(6.62, -2.07) * mm});
            skLineSegment(sketch, "E1462", {"start": v(6.62, -2.07) * mm, "end": v(6.67, -2.05) * mm});
            skLineSegment(sketch, "E1463", {"start": v(6.67, -2.05) * mm, "end": v(6.75, -2.03) * mm});
            skLineSegment(sketch, "E1464", {"start": v(6.75, -2.03) * mm, "end": v(6.82, -2.01) * mm});
            skLineSegment(sketch, "E1465", {"start": v(6.82, -2.01) * mm, "end": v(6.89, -2) * mm});
            skLineSegment(sketch, "E1466", {"start": v(6.89, -2) * mm, "end": v(7.07, -1.98) * mm});
            skLineSegment(sketch, "E1467", {"start": v(7.07, -1.98) * mm, "end": v(7.24, -1.96) * mm});
            skLineSegment(sketch, "E1468", {"start": v(7.24, -1.96) * mm, "end": v(7.38, -1.94) * mm});
            skLineSegment(sketch, "E1469", {"start": v(7.38, -1.94) * mm, "end": v(7.5, -1.93) * mm});
            skLineSegment(sketch, "E1470", {"start": v(7.5, -1.93) * mm, "end": v(7.62, -1.92) * mm});
            skLineSegment(sketch, "E1471", {"start": v(7.62, -1.92) * mm, "end": v(7.72, -1.92) * mm});
            skLineSegment(sketch, "E1472", {"start": v(7.72, -1.92) * mm, "end": v(7.82, -1.92) * mm});
            skLineSegment(sketch, "E1473", {"start": v(7.82, -1.92) * mm, "end": v(7.91, -1.92) * mm});
            skLineSegment(sketch, "E1474", {"start": v(7.91, -1.92) * mm, "end": v(8.29, -1.97) * mm});
            skLineSegment(sketch, "E1475", {"start": v(8.29, -1.97) * mm, "end": v(8.63, -2.06) * mm});
            skLineSegment(sketch, "E1476", {"start": v(8.63, -2.06) * mm, "end": v(8.69, -2.08) * mm});
            skLineSegment(sketch, "E1477", {"start": v(8.69, -2.08) * mm, "end": v(8.72, -2.09) * mm});
            skLineSegment(sketch, "E1478", {"start": v(8.72, -2.09) * mm, "end": v(8.73, -2.08) * mm});
            skLineSegment(sketch, "E1479", {"start": v(8.73, -2.08) * mm, "end": v(8.73, -2.05) * mm});
            skLineSegment(sketch, "E1480", {"start": v(-8.59, -1.9) * mm, "end": v(-8.55, -1.9) * mm});
            skLineSegment(sketch, "E1481", {"start": v(-8.55, -1.9) * mm, "end": v(-8.5, -1.87) * mm});
            skLineSegment(sketch, "E1482", {"start": v(-8.5, -1.87) * mm, "end": v(-8.45, -1.85) * mm});
            skLineSegment(sketch, "E1483", {"start": v(-8.45, -1.85) * mm, "end": v(-8.39, -1.83) * mm});
            skLineSegment(sketch, "E1484", {"start": v(-8.39, -1.83) * mm, "end": v(-8.2, -1.75) * mm});
            skLineSegment(sketch, "E1485", {"start": v(-8.2, -1.75) * mm, "end": v(-8, -1.71) * mm});
            skLineSegment(sketch, "E1486", {"start": v(-8, -1.71) * mm, "end": v(-7.82, -1.7) * mm});
            skLineSegment(sketch, "E1487", {"start": v(-7.82, -1.7) * mm, "end": v(-7.63, -1.7) * mm});
            skLineSegment(sketch, "E1488", {"start": v(-7.63, -1.7) * mm, "end": v(-7.5, -1.72) * mm});
            skLineSegment(sketch, "E1489", {"start": v(-7.5, -1.72) * mm, "end": v(-7.42, -1.72) * mm});
            skLineSegment(sketch, "E1490", {"start": v(-7.42, -1.72) * mm, "end": v(-7.38, -1.7) * mm});
            skLineSegment(sketch, "E1491", {"start": v(-7.38, -1.7) * mm, "end": v(-7.35, -1.68) * mm});
            skLineSegment(sketch, "E1492", {"start": v(-7.35, -1.68) * mm, "end": v(-7.33, -1.66) * mm});
            skLineSegment(sketch, "E1493", {"start": v(-7.33, -1.66) * mm, "end": v(-7.3, -1.64) * mm});
            skLineSegment(sketch, "E1494", {"start": v(-7.3, -1.64) * mm, "end": v(-7.29, -1.6) * mm});
            skLineSegment(sketch, "E1495", {"start": v(-7.29, -1.6) * mm, "end": v(-7.26, -1.58) * mm});
            skLineSegment(sketch, "E1496", {"start": v(-7.26, -1.58) * mm, "end": v(-7.11, -1.43) * mm});
            skLineSegment(sketch, "E1497", {"start": v(-7.11, -1.43) * mm, "end": v(-6.91, -1.3) * mm});
            skLineSegment(sketch, "E1498", {"start": v(-6.91, -1.3) * mm, "end": v(-6.66, -1.18) * mm});
            skLineSegment(sketch, "E1499", {"start": v(-6.66, -1.18) * mm, "end": v(-6.37, -1.08) * mm});
            skLineSegment(sketch, "E1500", {"start": v(-6.37, -1.08) * mm, "end": v(-6.24, -1.04) * mm});
            skLineSegment(sketch, "E1501", {"start": v(-6.24, -1.04) * mm, "end": v(-6.14, -1.02) * mm});
            skLineSegment(sketch, "E1502", {"start": v(-6.14, -1.02) * mm, "end": v(-6.07, -1) * mm});
            skLineSegment(sketch, "E1503", {"start": v(-6.07, -1) * mm, "end": v(-6.02, -0.98) * mm});
            skLineSegment(sketch, "E1504", {"start": v(-6.02, -0.98) * mm, "end": v(-6, -0.97) * mm});
            skLineSegment(sketch, "E1505", {"start": v(-6, -0.97) * mm, "end": v(-6, -0.96) * mm});
            skLineSegment(sketch, "E1506", {"start": v(-6, -0.96) * mm, "end": v(-6.02, -0.96) * mm});
            skLineSegment(sketch, "E1507", {"start": v(-6.02, -0.96) * mm, "end": v(-6.05, -0.95) * mm});
            skLineSegment(sketch, "E1508", {"start": v(-6.05, -0.95) * mm, "end": v(-6.2, -0.93) * mm});
            skLineSegment(sketch, "E1509", {"start": v(-6.2, -0.93) * mm, "end": v(-6.38, -0.9) * mm});
            skLineSegment(sketch, "E1510", {"start": v(-6.38, -0.9) * mm, "end": v(-6.6, -0.84) * mm});
            skLineSegment(sketch, "E1511", {"start": v(-6.6, -0.84) * mm, "end": v(-6.8, -0.78) * mm});
            skLineSegment(sketch, "E1512", {"start": v(-6.8, -0.78) * mm, "end": v(-6.93, -0.74) * mm});
            skLineSegment(sketch, "E1513", {"start": v(-6.93, -0.74) * mm, "end": v(-7.05, -0.72) * mm});
            skLineSegment(sketch, "E1514", {"start": v(-7.05, -0.72) * mm, "end": v(-7.17, -0.7) * mm});
            skLineSegment(sketch, "E1515", {"start": v(-7.17, -0.7) * mm, "end": v(-7.3, -0.7) * mm});
            skLineSegment(sketch, "E1516", {"start": v(-7.3, -0.7) * mm, "end": v(-7.48, -0.7) * mm});
            skLineSegment(sketch, "E1517", {"start": v(-7.48, -0.7) * mm, "end": v(-7.66, -0.71) * mm});
            skLineSegment(sketch, "E1518", {"start": v(-7.66, -0.71) * mm, "end": v(-7.81, -0.74) * mm});
            skLineSegment(sketch, "E1519", {"start": v(-7.81, -0.74) * mm, "end": v(-7.94, -0.78) * mm});
            skLineSegment(sketch, "E1520", {"start": v(-7.94, -0.78) * mm, "end": v(-8.12, -0.87) * mm});
            skLineSegment(sketch, "E1521", {"start": v(-8.12, -0.87) * mm, "end": v(-8.25, -0.94) * mm});
            skLineSegment(sketch, "E1522", {"start": v(-8.25, -0.94) * mm, "end": v(-8.36, -1.03) * mm});
            skLineSegment(sketch, "E1523", {"start": v(-8.36, -1.03) * mm, "end": v(-8.47, -1.14) * mm});
            skLineSegment(sketch, "E1524", {"start": v(-8.47, -1.14) * mm, "end": v(-8.6, -1.32) * mm});
            skLineSegment(sketch, "E1525", {"start": v(-8.6, -1.32) * mm, "end": v(-8.7, -1.48) * mm});
            skLineSegment(sketch, "E1526", {"start": v(-8.7, -1.48) * mm, "end": v(-8.74, -1.65) * mm});
            skLineSegment(sketch, "E1527", {"start": v(-8.74, -1.65) * mm, "end": v(-8.76, -1.85) * mm});
            skLineSegment(sketch, "E1528", {"start": v(-8.76, -1.85) * mm, "end": v(-8.76, -1.95) * mm});
            skLineSegment(sketch, "E1529", {"start": v(-8.76, -1.95) * mm, "end": v(-8.7, -1.94) * mm});
            skLineSegment(sketch, "E1530", {"start": v(-8.7, -1.94) * mm, "end": v(-8.69, -1.94) * mm});
            skLineSegment(sketch, "E1531", {"start": v(-8.69, -1.94) * mm, "end": v(-8.65, -1.93) * mm});
            skLineSegment(sketch, "E1532", {"start": v(-8.65, -1.93) * mm, "end": v(-8.62, -1.92) * mm});
            skLineSegment(sketch, "E1533", {"start": v(-8.62, -1.92) * mm, "end": v(-8.59, -1.9) * mm});
            skLineSegment(sketch, "E1534", {"start": v(-0.36, -1.68) * mm, "end": v(-0.34, -1.67) * mm});
            skLineSegment(sketch, "E1535", {"start": v(-0.34, -1.67) * mm, "end": v(-0.32, -1.66) * mm});
            skLineSegment(sketch, "E1536", {"start": v(-0.32, -1.66) * mm, "end": v(-0.3, -1.64) * mm});
            skLineSegment(sketch, "E1537", {"start": v(-0.3, -1.64) * mm, "end": v(-0.27, -1.62) * mm});
            skLineSegment(sketch, "E1538", {"start": v(-0.27, -1.62) * mm, "end": v(-0.24, -1.6) * mm});
            skLineSegment(sketch, "E1539", {"start": v(-0.24, -1.6) * mm, "end": v(-0.22, -1.58) * mm});
            skLineSegment(sketch, "E1540", {"start": v(-0.22, -1.58) * mm, "end": v(-0.2, -1.56) * mm});
            skLineSegment(sketch, "E1541", {"start": v(-0.2, -1.56) * mm, "end": v(-0.2, -1.53) * mm});
            skLineSegment(sketch, "E1542", {"start": v(-0.2, -1.53) * mm, "end": v(-0.18, -1.48) * mm});
            skLineSegment(sketch, "E1543", {"start": v(-0.18, -1.48) * mm, "end": v(-0.18, -1.45) * mm});
            skLineSegment(sketch, "E1544", {"start": v(-0.18, -1.45) * mm, "end": v(-0.17, -1.43) * mm});
            skLineSegment(sketch, "E1545", {"start": v(-0.17, -1.43) * mm, "end": v(-0.16, -1.41) * mm});
            skLineSegment(sketch, "E1546", {"start": v(-0.16, -1.41) * mm, "end": v(-0.14, -1.4) * mm});
            skLineSegment(sketch, "E1547", {"start": v(-0.14, -1.4) * mm, "end": v(-0.11, -1.42) * mm});
            skLineSegment(sketch, "E1548", {"start": v(-0.11, -1.42) * mm, "end": v(-0.02, -1.47) * mm});
            skLineSegment(sketch, "E1549", {"start": v(-0.02, -1.47) * mm, "end": v(0.09, -1.5) * mm});
            skLineSegment(sketch, "E1550", {"start": v(0.09, -1.5) * mm, "end": v(0.2, -1.52) * mm});
            skLineSegment(sketch, "E1551", {"start": v(0.2, -1.52) * mm, "end": v(0.3, -1.52) * mm});
            skLineSegment(sketch, "E1552", {"start": v(0.3, -1.52) * mm, "end": v(0.32, -1.51) * mm});
            skLineSegment(sketch, "E1553", {"start": v(0.32, -1.51) * mm, "end": v(0.35, -1.5) * mm});
            skLineSegment(sketch, "E1554", {"start": v(0.35, -1.5) * mm, "end": v(0.36, -1.5) * mm});
            skLineSegment(sketch, "E1555", {"start": v(0.36, -1.5) * mm, "end": v(0.37, -1.47) * mm});
            skLineSegment(sketch, "E1556", {"start": v(0.37, -1.47) * mm, "end": v(0.39, -1.41) * mm});
            skLineSegment(sketch, "E1557", {"start": v(0.39, -1.41) * mm, "end": v(0.4, -1.33) * mm});
            skLineSegment(sketch, "E1558", {"start": v(0.4, -1.33) * mm, "end": v(0.42, -1.22) * mm});
            skLineSegment(sketch, "E1559", {"start": v(0.42, -1.22) * mm, "end": v(0.43, -1.1) * mm});
            skLineSegment(sketch, "E1560", {"start": v(0.43, -1.1) * mm, "end": v(0.44, -0.98) * mm});
            skLineSegment(sketch, "E1561", {"start": v(0.44, -0.98) * mm, "end": v(0.44, -0.86) * mm});
            skLineSegment(sketch, "E1562", {"start": v(0.44, -0.86) * mm, "end": v(0.44, -0.74) * mm});
            skLineSegment(sketch, "E1563", {"start": v(0.44, -0.74) * mm, "end": v(0.44, -0.63) * mm});
            skLineSegment(sketch, "E1564", {"start": v(0.44, -0.63) * mm, "end": v(0.43, -0.55) * mm});
            skLineSegment(sketch, "E1565", {"start": v(0.43, -0.55) * mm, "end": v(0.33, -0.64) * mm});
            skLineSegment(sketch, "E1566", {"start": v(0.33, -0.64) * mm, "end": v(0.28, -0.7) * mm});
            skLineSegment(sketch, "E1567", {"start": v(0.28, -0.7) * mm, "end": v(0.23, -0.73) * mm});
            skLineSegment(sketch, "E1568", {"start": v(0.23, -0.73) * mm, "end": v(0.18, -0.76) * mm});
            skLineSegment(sketch, "E1569", {"start": v(0.18, -0.76) * mm, "end": v(0.1, -0.8) * mm});
            skLineSegment(sketch, "E1570", {"start": v(0.1, -0.8) * mm, "end": v(0.03, -0.84) * mm});
            skLineSegment(sketch, "E1571", {"start": v(0.03, -0.84) * mm, "end": v(-0.02, -0.86) * mm});
            skLineSegment(sketch, "E1572", {"start": v(-0.02, -0.86) * mm, "end": v(-0.06, -0.87) * mm});
            skLineSegment(sketch, "E1573", {"start": v(-0.06, -0.87) * mm, "end": v(-0.1, -0.88) * mm});
            skLineSegment(sketch, "E1574", {"start": v(-0.1, -0.88) * mm, "end": v(-0.18, -0.88) * mm});
            skLineSegment(sketch, "E1575", {"start": v(-0.18, -0.88) * mm, "end": v(-0.24, -0.87) * mm});
            skLineSegment(sketch, "E1576", {"start": v(-0.24, -0.87) * mm, "end": v(-0.29, -0.85) * mm});
            skLineSegment(sketch, "E1577", {"start": v(-0.29, -0.85) * mm, "end": v(-0.34, -0.82) * mm});
            skLineSegment(sketch, "E1578", {"start": v(-0.34, -0.82) * mm, "end": v(-0.4, -0.78) * mm});
            skLineSegment(sketch, "E1579", {"start": v(-0.4, -0.78) * mm, "end": v(-0.47, -0.82) * mm});
            skLineSegment(sketch, "E1580", {"start": v(-0.47, -0.82) * mm, "end": v(-0.5, -0.84) * mm});
            skLineSegment(sketch, "E1581", {"start": v(-0.5, -0.84) * mm, "end": v(-0.52, -0.86) * mm});
            skLineSegment(sketch, "E1582", {"start": v(-0.52, -0.86) * mm, "end": v(-0.55, -0.88) * mm});
            skLineSegment(sketch, "E1583", {"start": v(-0.55, -0.88) * mm, "end": v(-0.57, -0.9) * mm});
            skLineSegment(sketch, "E1584", {"start": v(-0.57, -0.9) * mm, "end": v(-0.6, -0.92) * mm});
            skLineSegment(sketch, "E1585", {"start": v(-0.6, -0.92) * mm, "end": v(-0.61, -0.92) * mm});
            skLineSegment(sketch, "E1586", {"start": v(-0.61, -0.92) * mm, "end": v(-0.62, -0.93) * mm});
            skLineSegment(sketch, "E1587", {"start": v(-0.62, -0.93) * mm, "end": v(-0.64, -0.93) * mm});
            skLineSegment(sketch, "E1588", {"start": v(-0.64, -0.93) * mm, "end": v(-0.67, -0.94) * mm});
            skLineSegment(sketch, "E1589", {"start": v(-0.67, -0.94) * mm, "end": v(-0.7, -0.96) * mm});
            skLineSegment(sketch, "E1590", {"start": v(-0.7, -0.96) * mm, "end": v(-0.76, -0.98) * mm});
            skLineSegment(sketch, "E1591", {"start": v(-0.76, -0.98) * mm, "end": v(-0.8, -0.99) * mm});
            skLineSegment(sketch, "E1592", {"start": v(-0.8, -0.99) * mm, "end": v(-0.84, -0.99) * mm});
            skLineSegment(sketch, "E1593", {"start": v(-0.84, -0.99) * mm, "end": v(-0.89, -0.97) * mm});
            skLineSegment(sketch, "E1594", {"start": v(-0.89, -0.97) * mm, "end": v(-0.93, -0.95) * mm});
            skLineSegment(sketch, "E1595", {"start": v(-0.93, -0.95) * mm, "end": v(-0.93, -0.98) * mm});
            skLineSegment(sketch, "E1596", {"start": v(-0.93, -0.98) * mm, "end": v(-0.92, -1.02) * mm});
            skLineSegment(sketch, "E1597", {"start": v(-0.92, -1.02) * mm, "end": v(-0.9, -1.09) * mm});
            skLineSegment(sketch, "E1598", {"start": v(-0.9, -1.09) * mm, "end": v(-0.9, -1.17) * mm});
            skLineSegment(sketch, "E1599", {"start": v(-0.9, -1.17) * mm, "end": v(-0.88, -1.26) * mm});
            skLineSegment(sketch, "E1600", {"start": v(-0.88, -1.26) * mm, "end": v(-0.87, -1.35) * mm});
            skLineSegment(sketch, "E1601", {"start": v(-0.87, -1.35) * mm, "end": v(-0.85, -1.42) * mm});
            skLineSegment(sketch, "E1602", {"start": v(-0.85, -1.42) * mm, "end": v(-0.84, -1.48) * mm});
            skLineSegment(sketch, "E1603", {"start": v(-0.84, -1.48) * mm, "end": v(-0.84, -1.52) * mm});
            skLineSegment(sketch, "E1604", {"start": v(-0.84, -1.52) * mm, "end": v(-0.8, -1.56) * mm});
            skLineSegment(sketch, "E1605", {"start": v(-0.8, -1.56) * mm, "end": v(-0.76, -1.61) * mm});
            skLineSegment(sketch, "E1606", {"start": v(-0.76, -1.61) * mm, "end": v(-0.7, -1.66) * mm});
            skLineSegment(sketch, "E1607", {"start": v(-0.7, -1.66) * mm, "end": v(-0.61, -1.69) * mm});
            skLineSegment(sketch, "E1608", {"start": v(-0.61, -1.69) * mm, "end": v(-0.56, -1.7) * mm});
            skLineSegment(sketch, "E1609", {"start": v(-0.56, -1.7) * mm, "end": v(-0.49, -1.7) * mm});
            skLineSegment(sketch, "E1610", {"start": v(-0.49, -1.7) * mm, "end": v(-0.41, -1.7) * mm});
            skLineSegment(sketch, "E1611", {"start": v(-0.41, -1.7) * mm, "end": v(-0.36, -1.68) * mm});
            skLineSegment(sketch, "E1612", {"start": v(5.68, -1.2) * mm, "end": v(5.79, -1.18) * mm});
            skLineSegment(sketch, "E1613", {"start": v(5.79, -1.18) * mm, "end": v(5.88, -1.17) * mm});
            skLineSegment(sketch, "E1614", {"start": v(5.88, -1.17) * mm, "end": v(5.95, -1.15) * mm});
            skLineSegment(sketch, "E1615", {"start": v(5.95, -1.15) * mm, "end": v(6.02, -1.12) * mm});
            skLineSegment(sketch, "E1616", {"start": v(6.02, -1.12) * mm, "end": v(6.08, -1.09) * mm});
            skLineSegment(sketch, "E1617", {"start": v(6.08, -1.09) * mm, "end": v(6.15, -1.04) * mm});
            skLineSegment(sketch, "E1618", {"start": v(6.15, -1.04) * mm, "end": v(6.23, -0.98) * mm});
            skLineSegment(sketch, "E1619", {"start": v(6.23, -0.98) * mm, "end": v(6.32, -0.9) * mm});
            skLineSegment(sketch, "E1620", {"start": v(6.32, -0.9) * mm, "end": v(6.37, -0.85) * mm});
            skLineSegment(sketch, "E1621", {"start": v(6.37, -0.85) * mm, "end": v(6.41, -0.8) * mm});
            skLineSegment(sketch, "E1622", {"start": v(6.41, -0.8) * mm, "end": v(6.45, -0.78) * mm});
            skLineSegment(sketch, "E1623", {"start": v(6.45, -0.78) * mm, "end": v(6.48, -0.76) * mm});
            skLineSegment(sketch, "E1624", {"start": v(6.48, -0.76) * mm, "end": v(6.52, -0.74) * mm});
            skLineSegment(sketch, "E1625", {"start": v(6.52, -0.74) * mm, "end": v(6.45, -0.73) * mm});
            skLineSegment(sketch, "E1626", {"start": v(6.45, -0.73) * mm, "end": v(6.4, -0.73) * mm});
            skLineSegment(sketch, "E1627", {"start": v(6.4, -0.73) * mm, "end": v(6.32, -0.73) * mm});
            skLineSegment(sketch, "E1628", {"start": v(6.32, -0.73) * mm, "end": v(6.22, -0.73) * mm});
            skLineSegment(sketch, "E1629", {"start": v(6.22, -0.73) * mm, "end": v(6.12, -0.73) * mm});
            skLineSegment(sketch, "E1630", {"start": v(6.12, -0.73) * mm, "end": v(5.88, -0.72) * mm});
            skLineSegment(sketch, "E1631", {"start": v(5.88, -0.72) * mm, "end": v(5.65, -0.7) * mm});
            skLineSegment(sketch, "E1632", {"start": v(5.65, -0.7) * mm, "end": v(5.43, -0.7) * mm});
            skLineSegment(sketch, "E1633", {"start": v(5.43, -0.7) * mm, "end": v(5.26, -0.67) * mm});
            skLineSegment(sketch, "E1634", {"start": v(5.26, -0.67) * mm, "end": v(5.17, -0.66) * mm});
            skLineSegment(sketch, "E1635", {"start": v(5.17, -0.66) * mm, "end": v(5.06, -0.64) * mm});
            skLineSegment(sketch, "E1636", {"start": v(5.06, -0.64) * mm, "end": v(4.93, -0.62) * mm});
            skLineSegment(sketch, "E1637", {"start": v(4.93, -0.62) * mm, "end": v(4.8, -0.59) * mm});
            skLineSegment(sketch, "E1638", {"start": v(4.8, -0.59) * mm, "end": v(4.67, -0.56) * mm});
            skLineSegment(sketch, "E1639", {"start": v(4.67, -0.56) * mm, "end": v(4.55, -0.54) * mm});
            skLineSegment(sketch, "E1640", {"start": v(4.55, -0.54) * mm, "end": v(4.45, -0.52) * mm});
            skLineSegment(sketch, "E1641", {"start": v(4.45, -0.52) * mm, "end": v(4.38, -0.5) * mm});
            skLineSegment(sketch, "E1642", {"start": v(4.38, -0.5) * mm, "end": v(4.23, -0.46) * mm});
            skLineSegment(sketch, "E1643", {"start": v(4.23, -0.46) * mm, "end": v(4.1, -0.44) * mm});
            skLineSegment(sketch, "E1644", {"start": v(4.1, -0.44) * mm, "end": v(4, -0.43) * mm});
            skLineSegment(sketch, "E1645", {"start": v(4, -0.43) * mm, "end": v(3.93, -0.43) * mm});
            skLineSegment(sketch, "E1646", {"start": v(3.93, -0.43) * mm, "end": v(3.9, -0.45) * mm});
            skLineSegment(sketch, "E1647", {"start": v(3.9, -0.45) * mm, "end": v(3.89, -0.48) * mm});
            skLineSegment(sketch, "E1648", {"start": v(3.89, -0.48) * mm, "end": v(3.88, -0.5) * mm});
            skLineSegment(sketch, "E1649", {"start": v(3.88, -0.5) * mm, "end": v(3.88, -0.53) * mm});
            skLineSegment(sketch, "E1650", {"start": v(3.88, -0.53) * mm, "end": v(3.9, -0.57) * mm});
            skLineSegment(sketch, "E1651", {"start": v(3.9, -0.57) * mm, "end": v(3.91, -0.63) * mm});
            skLineSegment(sketch, "E1652", {"start": v(3.91, -0.63) * mm, "end": v(3.93, -0.67) * mm});
            skLineSegment(sketch, "E1653", {"start": v(3.93, -0.67) * mm, "end": v(3.95, -0.72) * mm});
            skLineSegment(sketch, "E1654", {"start": v(3.95, -0.72) * mm, "end": v(3.97, -0.76) * mm});
            skLineSegment(sketch, "E1655", {"start": v(3.97, -0.76) * mm, "end": v(3.98, -0.8) * mm});
            skLineSegment(sketch, "E1656", {"start": v(3.98, -0.8) * mm, "end": v(4.02, -0.86) * mm});
            skLineSegment(sketch, "E1657", {"start": v(4.02, -0.86) * mm, "end": v(4.06, -0.94) * mm});
            skLineSegment(sketch, "E1658", {"start": v(4.06, -0.94) * mm, "end": v(4.09, -1.01) * mm});
            skLineSegment(sketch, "E1659", {"start": v(4.09, -1.01) * mm, "end": v(4.1, -1.06) * mm});
            skLineSegment(sketch, "E1660", {"start": v(4.1, -1.06) * mm, "end": v(4.11, -1.08) * mm});
            skLineSegment(sketch, "E1661", {"start": v(4.11, -1.08) * mm, "end": v(4.12, -1.1) * mm});
            skLineSegment(sketch, "E1662", {"start": v(4.12, -1.1) * mm, "end": v(4.13, -1.1) * mm});
            skLineSegment(sketch, "E1663", {"start": v(4.13, -1.1) * mm, "end": v(4.17, -1.1) * mm});
            skLineSegment(sketch, "E1664", {"start": v(4.17, -1.1) * mm, "end": v(4.22, -1.12) * mm});
            skLineSegment(sketch, "E1665", {"start": v(4.22, -1.12) * mm, "end": v(4.27, -1.13) * mm});
            skLineSegment(sketch, "E1666", {"start": v(4.27, -1.13) * mm, "end": v(4.35, -1.15) * mm});
            skLineSegment(sketch, "E1667", {"start": v(4.35, -1.15) * mm, "end": v(4.42, -1.16) * mm});
            skLineSegment(sketch, "E1668", {"start": v(4.42, -1.16) * mm, "end": v(4.5, -1.16) * mm});
            skLineSegment(sketch, "E1669", {"start": v(4.5, -1.16) * mm, "end": v(4.6, -1.16) * mm});
            skLineSegment(sketch, "E1670", {"start": v(4.6, -1.16) * mm, "end": v(4.68, -1.16) * mm});
            skLineSegment(sketch, "E1671", {"start": v(4.68, -1.16) * mm, "end": v(4.75, -1.16) * mm});
            skLineSegment(sketch, "E1672", {"start": v(4.75, -1.16) * mm, "end": v(4.8, -1.15) * mm});
            skLineSegment(sketch, "E1673", {"start": v(4.8, -1.15) * mm, "end": v(4.85, -1.15) * mm});
            skLineSegment(sketch, "E1674", {"start": v(4.85, -1.15) * mm, "end": v(4.89, -1.14) * mm});
            skLineSegment(sketch, "E1675", {"start": v(4.89, -1.14) * mm, "end": v(4.94, -1.14) * mm});
            skLineSegment(sketch, "E1676", {"start": v(4.94, -1.14) * mm, "end": v(5, -1.14) * mm});
            skLineSegment(sketch, "E1677", {"start": v(5, -1.14) * mm, "end": v(5.07, -1.14) * mm});
            skLineSegment(sketch, "E1678", {"start": v(5.07, -1.14) * mm, "end": v(5.15, -1.14) * mm});
            skLineSegment(sketch, "E1679", {"start": v(5.15, -1.14) * mm, "end": v(5.22, -1.14) * mm});
            skLineSegment(sketch, "E1680", {"start": v(5.22, -1.14) * mm, "end": v(5.28, -1.15) * mm});
            skLineSegment(sketch, "E1681", {"start": v(5.28, -1.15) * mm, "end": v(5.36, -1.17) * mm});
            skLineSegment(sketch, "E1682", {"start": v(5.36, -1.17) * mm, "end": v(5.41, -1.18) * mm});
            skLineSegment(sketch, "E1683", {"start": v(5.41, -1.18) * mm, "end": v(5.45, -1.2) * mm});
            skLineSegment(sketch, "E1684", {"start": v(5.45, -1.2) * mm, "end": v(5.48, -1.2) * mm});
            skLineSegment(sketch, "E1685", {"start": v(5.48, -1.2) * mm, "end": v(5.5, -1.2) * mm});
            skLineSegment(sketch, "E1686", {"start": v(5.5, -1.2) * mm, "end": v(5.5, -1.21) * mm});
            skLineSegment(sketch, "E1687", {"start": v(5.5, -1.21) * mm, "end": v(5.5, -1.21) * mm});
            skLineSegment(sketch, "E1688", {"start": v(5.5, -1.21) * mm, "end": v(5.52, -1.21) * mm});
            skLineSegment(sketch, "E1689", {"start": v(5.52, -1.21) * mm, "end": v(5.54, -1.21) * mm});
            skLineSegment(sketch, "E1690", {"start": v(5.54, -1.21) * mm, "end": v(5.57, -1.2) * mm});
            skLineSegment(sketch, "E1691", {"start": v(5.57, -1.2) * mm, "end": v(5.62, -1.2) * mm});
            skLineSegment(sketch, "E1692", {"start": v(5.62, -1.2) * mm, "end": v(5.68, -1.2) * mm});
            skLineSegment(sketch, "E1693", {"start": v(3.78, -0.93) * mm, "end": v(3.74, -0.83) * mm});
            skLineSegment(sketch, "E1694", {"start": v(3.74, -0.83) * mm, "end": v(3.68, -0.74) * mm});
            skLineSegment(sketch, "E1695", {"start": v(3.68, -0.74) * mm, "end": v(3.62, -0.64) * mm});
            skLineSegment(sketch, "E1696", {"start": v(3.62, -0.64) * mm, "end": v(3.53, -0.53) * mm});
            skLineSegment(sketch, "E1697", {"start": v(3.53, -0.53) * mm, "end": v(3.5, -0.5) * mm});
            skLineSegment(sketch, "E1698", {"start": v(3.5, -0.5) * mm, "end": v(3.47, -0.46) * mm});
            skLineSegment(sketch, "E1699", {"start": v(3.47, -0.46) * mm, "end": v(3.45, -0.43) * mm});
            skLineSegment(sketch, "E1700", {"start": v(3.45, -0.43) * mm, "end": v(3.44, -0.41) * mm});
            skLineSegment(sketch, "E1701", {"start": v(3.44, -0.41) * mm, "end": v(3.38, -0.35) * mm});
            skLineSegment(sketch, "E1702", {"start": v(3.38, -0.35) * mm, "end": v(3.3, -0.27) * mm});
            skLineSegment(sketch, "E1703", {"start": v(3.3, -0.27) * mm, "end": v(3.2, -0.2) * mm});
            skLineSegment(sketch, "E1704", {"start": v(3.2, -0.2) * mm, "end": v(3.1, -0.13) * mm});
            skLineSegment(sketch, "E1705", {"start": v(3.1, -0.13) * mm, "end": v(3.05, -0.1) * mm});
            skLineSegment(sketch, "E1706", {"start": v(3.05, -0.1) * mm, "end": v(2.98, -0.06) * mm});
            skLineSegment(sketch, "E1707", {"start": v(2.98, -0.06) * mm, "end": v(2.91, -0.02) * mm});
            skLineSegment(sketch, "E1708", {"start": v(2.91, -0.02) * mm, "end": v(2.84, 0.02) * mm});
            skLineSegment(sketch, "E1709", {"start": v(2.84, 0.02) * mm, "end": v(2.77, 0.05) * mm});
            skLineSegment(sketch, "E1710", {"start": v(2.77, 0.05) * mm, "end": v(2.7, 0.08) * mm});
            skLineSegment(sketch, "E1711", {"start": v(2.7, 0.08) * mm, "end": v(2.65, 0.1) * mm});
            skLineSegment(sketch, "E1712", {"start": v(2.65, 0.1) * mm, "end": v(2.61, 0.12) * mm});
            skLineSegment(sketch, "E1713", {"start": v(2.61, 0.12) * mm, "end": v(2.55, 0.13) * mm});
            skLineSegment(sketch, "E1714", {"start": v(2.55, 0.13) * mm, "end": v(2.5, 0.15) * mm});
            skLineSegment(sketch, "E1715", {"start": v(2.5, 0.15) * mm, "end": v(2.48, 0.16) * mm});
            skLineSegment(sketch, "E1716", {"start": v(2.48, 0.16) * mm, "end": v(2.44, 0.17) * mm});
            skLineSegment(sketch, "E1717", {"start": v(2.44, 0.17) * mm, "end": v(2.4, 0.17) * mm});
            skLineSegment(sketch, "E1718", {"start": v(2.4, 0.17) * mm, "end": v(2.36, 0.18) * mm});
            skLineSegment(sketch, "E1719", {"start": v(2.36, 0.18) * mm, "end": v(2.3, 0.19) * mm});
            skLineSegment(sketch, "E1720", {"start": v(2.3, 0.19) * mm, "end": v(2.26, 0.2) * mm});
            skLineSegment(sketch, "E1721", {"start": v(2.26, 0.2) * mm, "end": v(2.21, 0.2) * mm});
            skLineSegment(sketch, "E1722", {"start": v(2.21, 0.2) * mm, "end": v(2.18, 0.2) * mm});
            skLineSegment(sketch, "E1723", {"start": v(2.18, 0.2) * mm, "end": v(2.06, 0.22) * mm});
            skLineSegment(sketch, "E1724", {"start": v(2.06, 0.22) * mm, "end": v(1.92, 0.23) * mm});
            skLineSegment(sketch, "E1725", {"start": v(1.92, 0.23) * mm, "end": v(1.74, 0.23) * mm});
            skLineSegment(sketch, "E1726", {"start": v(1.74, 0.23) * mm, "end": v(1.51, 0.22) * mm});
            skLineSegment(sketch, "E1727", {"start": v(1.51, 0.22) * mm, "end": v(1.4, 0.22) * mm});
            skLineSegment(sketch, "E1728", {"start": v(1.4, 0.22) * mm, "end": v(1.31, 0.22) * mm});
            skLineSegment(sketch, "E1729", {"start": v(1.31, 0.22) * mm, "end": v(1.25, 0.21) * mm});
            skLineSegment(sketch, "E1730", {"start": v(1.25, 0.21) * mm, "end": v(1.2, 0.2) * mm});
            skLineSegment(sketch, "E1731", {"start": v(1.2, 0.2) * mm, "end": v(1.15, 0.2) * mm});
            skLineSegment(sketch, "E1732", {"start": v(1.15, 0.2) * mm, "end": v(1.1, 0.2) * mm});
            skLineSegment(sketch, "E1733", {"start": v(1.1, 0.2) * mm, "end": v(1.07, 0.18) * mm});
            skLineSegment(sketch, "E1734", {"start": v(1.07, 0.18) * mm, "end": v(1.01, 0.17) * mm});
            skLineSegment(sketch, "E1735", {"start": v(1.01, 0.17) * mm, "end": v(0.94, 0.15) * mm});
            skLineSegment(sketch, "E1736", {"start": v(0.94, 0.15) * mm, "end": v(0.87, 0.13) * mm});
            skLineSegment(sketch, "E1737", {"start": v(0.87, 0.13) * mm, "end": v(0.81, 0.11) * mm});
            skLineSegment(sketch, "E1738", {"start": v(0.81, 0.11) * mm, "end": v(0.76, 0.1) * mm});
            skLineSegment(sketch, "E1739", {"start": v(0.76, 0.1) * mm, "end": v(0.7, 0.08) * mm});
            skLineSegment(sketch, "E1740", {"start": v(0.7, 0.08) * mm, "end": v(0.68, 0.06) * mm});
            skLineSegment(sketch, "E1741", {"start": v(0.68, 0.06) * mm, "end": v(0.67, 0.05) * mm});
            skLineSegment(sketch, "E1742", {"start": v(0.67, 0.05) * mm, "end": v(0.67, 0.03) * mm});
            skLineSegment(sketch, "E1743", {"start": v(0.67, 0.03) * mm, "end": v(0.67, 0) * mm});
            skLineSegment(sketch, "E1744", {"start": v(0.67, 0) * mm, "end": v(0.67, -0.05) * mm});
            skLineSegment(sketch, "E1745", {"start": v(0.67, -0.05) * mm, "end": v(0.68, -0.13) * mm});
            skLineSegment(sketch, "E1746", {"start": v(0.68, -0.13) * mm, "end": v(0.69, -0.22) * mm});
            skLineSegment(sketch, "E1747", {"start": v(0.69, -0.22) * mm, "end": v(0.7, -0.45) * mm});
            skLineSegment(sketch, "E1748", {"start": v(0.7, -0.45) * mm, "end": v(0.83, -0.45) * mm});
            skLineSegment(sketch, "E1749", {"start": v(0.83, -0.45) * mm, "end": v(0.93, -0.46) * mm});
            skLineSegment(sketch, "E1750", {"start": v(0.93, -0.46) * mm, "end": v(1.05, -0.47) * mm});
            skLineSegment(sketch, "E1751", {"start": v(1.05, -0.47) * mm, "end": v(1.19, -0.48) * mm});
            skLineSegment(sketch, "E1752", {"start": v(1.19, -0.48) * mm, "end": v(1.32, -0.5) * mm});
            skLineSegment(sketch, "E1753", {"start": v(1.32, -0.5) * mm, "end": v(1.46, -0.52) * mm});
            skLineSegment(sketch, "E1754", {"start": v(1.46, -0.52) * mm, "end": v(1.57, -0.54) * mm});
            skLineSegment(sketch, "E1755", {"start": v(1.57, -0.54) * mm, "end": v(1.67, -0.55) * mm});
            skLineSegment(sketch, "E1756", {"start": v(1.67, -0.55) * mm, "end": v(1.73, -0.57) * mm});
            skLineSegment(sketch, "E1757", {"start": v(1.73, -0.57) * mm, "end": v(1.75, -0.57) * mm});
            skLineSegment(sketch, "E1758", {"start": v(1.75, -0.57) * mm, "end": v(1.78, -0.58) * mm});
            skLineSegment(sketch, "E1759", {"start": v(1.78, -0.58) * mm, "end": v(1.82, -0.59) * mm});
            skLineSegment(sketch, "E1760", {"start": v(1.82, -0.59) * mm, "end": v(1.86, -0.6) * mm});
            skLineSegment(sketch, "E1761", {"start": v(1.86, -0.6) * mm, "end": v(2.03, -0.64) * mm});
            skLineSegment(sketch, "E1762", {"start": v(2.03, -0.64) * mm, "end": v(2.22, -0.7) * mm});
            skLineSegment(sketch, "E1763", {"start": v(2.22, -0.7) * mm, "end": v(2.41, -0.79) * mm});
            skLineSegment(sketch, "E1764", {"start": v(2.41, -0.79) * mm, "end": v(2.58, -0.88) * mm});
            skLineSegment(sketch, "E1765", {"start": v(2.58, -0.88) * mm, "end": v(2.69, -0.94) * mm});
            skLineSegment(sketch, "E1766", {"start": v(2.69, -0.94) * mm, "end": v(2.8, -0.92) * mm});
            skLineSegment(sketch, "E1767", {"start": v(2.8, -0.92) * mm, "end": v(2.89, -0.92) * mm});
            skLineSegment(sketch, "E1768", {"start": v(2.89, -0.92) * mm, "end": v(3, -0.91) * mm});
            skLineSegment(sketch, "E1769", {"start": v(3, -0.91) * mm, "end": v(3.13, -0.92) * mm});
            skLineSegment(sketch, "E1770", {"start": v(3.13, -0.92) * mm, "end": v(3.27, -0.92) * mm});
            skLineSegment(sketch, "E1771", {"start": v(3.27, -0.92) * mm, "end": v(3.4, -0.93) * mm});
            skLineSegment(sketch, "E1772", {"start": v(3.4, -0.93) * mm, "end": v(3.53, -0.94) * mm});
            skLineSegment(sketch, "E1773", {"start": v(3.53, -0.94) * mm, "end": v(3.64, -0.96) * mm});
            skLineSegment(sketch, "E1774", {"start": v(3.64, -0.96) * mm, "end": v(3.73, -0.98) * mm});
            skLineSegment(sketch, "E1775", {"start": v(3.73, -0.98) * mm, "end": v(3.78, -0.99) * mm});
            skLineSegment(sketch, "E1776", {"start": v(3.78, -0.99) * mm, "end": v(3.8, -0.99) * mm});
            skLineSegment(sketch, "E1777", {"start": v(3.8, -0.99) * mm, "end": v(3.8, -0.97) * mm});
            skLineSegment(sketch, "E1778", {"start": v(3.8, -0.97) * mm, "end": v(3.78, -0.93) * mm});
            skLineSegment(sketch, "E1779", {"start": v(-5.4, -0.66) * mm, "end": v(-5.29, -0.63) * mm});
            skLineSegment(sketch, "E1780", {"start": v(-5.29, -0.63) * mm, "end": v(-5.21, -0.62) * mm});
            skLineSegment(sketch, "E1781", {"start": v(-5.21, -0.62) * mm, "end": v(-5.13, -0.6) * mm});
            skLineSegment(sketch, "E1782", {"start": v(-5.13, -0.6) * mm, "end": v(-5, -0.6) * mm});
            skLineSegment(sketch, "E1783", {"start": v(-5, -0.6) * mm, "end": v(-4.92, -0.6) * mm});
            skLineSegment(sketch, "E1784", {"start": v(-4.92, -0.6) * mm, "end": v(-4.84, -0.6) * mm});
            skLineSegment(sketch, "E1785", {"start": v(-4.84, -0.6) * mm, "end": v(-4.77, -0.61) * mm});
            skLineSegment(sketch, "E1786", {"start": v(-4.77, -0.61) * mm, "end": v(-4.72, -0.61) * mm});
            skLineSegment(sketch, "E1787", {"start": v(-4.72, -0.61) * mm, "end": v(-4.65, -0.62) * mm});
            skLineSegment(sketch, "E1788", {"start": v(-4.65, -0.62) * mm, "end": v(-4.57, -0.47) * mm});
            skLineSegment(sketch, "E1789", {"start": v(-4.57, -0.47) * mm, "end": v(-4.54, -0.4) * mm});
            skLineSegment(sketch, "E1790", {"start": v(-4.54, -0.4) * mm, "end": v(-4.5, -0.34) * mm});
            skLineSegment(sketch, "E1791", {"start": v(-4.5, -0.34) * mm, "end": v(-4.46, -0.29) * mm});
            skLineSegment(sketch, "E1792", {"start": v(-4.46, -0.29) * mm, "end": v(-4.43, -0.25) * mm});
            skLineSegment(sketch, "E1793", {"start": v(-4.43, -0.25) * mm, "end": v(-4.33, -0.13) * mm});
            skLineSegment(sketch, "E1794", {"start": v(-4.33, -0.13) * mm, "end": v(-4.23, -0.02) * mm});
            skLineSegment(sketch, "E1795", {"start": v(-4.23, -0.02) * mm, "end": v(-4.14, 0.07) * mm});
            skLineSegment(sketch, "E1796", {"start": v(-4.14, 0.07) * mm, "end": v(-4.07, 0.14) * mm});
            skLineSegment(sketch, "E1797", {"start": v(-4.07, 0.14) * mm, "end": v(-3.97, 0.22) * mm});
            skLineSegment(sketch, "E1798", {"start": v(-3.97, 0.22) * mm, "end": v(-3.83, 0.31) * mm});
            skLineSegment(sketch, "E1799", {"start": v(-3.83, 0.31) * mm, "end": v(-3.68, 0.4) * mm});
            skLineSegment(sketch, "E1800", {"start": v(-3.68, 0.4) * mm, "end": v(-3.52, 0.5) * mm});
            skLineSegment(sketch, "E1801", {"start": v(-3.52, 0.5) * mm, "end": v(-3.33, 0.6) * mm});
            skLineSegment(sketch, "E1802", {"start": v(-3.33, 0.6) * mm, "end": v(-3.43, 0.6) * mm});
            skLineSegment(sketch, "E1803", {"start": v(-3.43, 0.6) * mm, "end": v(-3.5, 0.59) * mm});
            skLineSegment(sketch, "E1804", {"start": v(-3.5, 0.59) * mm, "end": v(-3.6, 0.57) * mm});
            skLineSegment(sketch, "E1805", {"start": v(-3.6, 0.57) * mm, "end": v(-3.72, 0.55) * mm});
            skLineSegment(sketch, "E1806", {"start": v(-3.72, 0.55) * mm, "end": v(-3.86, 0.52) * mm});
            skLineSegment(sketch, "E1807", {"start": v(-3.86, 0.52) * mm, "end": v(-4, 0.48) * mm});
            skLineSegment(sketch, "E1808", {"start": v(-4, 0.48) * mm, "end": v(-4.15, 0.45) * mm});
            skLineSegment(sketch, "E1809", {"start": v(-4.15, 0.45) * mm, "end": v(-4.29, 0.42) * mm});
            skLineSegment(sketch, "E1810", {"start": v(-4.29, 0.42) * mm, "end": v(-4.4, 0.39) * mm});
            skLineSegment(sketch, "E1811", {"start": v(-4.4, 0.39) * mm, "end": v(-4.6, 0.33) * mm});
            skLineSegment(sketch, "E1812", {"start": v(-4.6, 0.33) * mm, "end": v(-4.79, 0.27) * mm});
            skLineSegment(sketch, "E1813", {"start": v(-4.79, 0.27) * mm, "end": v(-4.95, 0.22) * mm});
            skLineSegment(sketch, "E1814", {"start": v(-4.95, 0.22) * mm, "end": v(-5.1, 0.16) * mm});
            skLineSegment(sketch, "E1815", {"start": v(-5.1, 0.16) * mm, "end": v(-5.24, 0.1) * mm});
            skLineSegment(sketch, "E1816", {"start": v(-5.24, 0.1) * mm, "end": v(-5.37, 0.04) * mm});
            skLineSegment(sketch, "E1817", {"start": v(-5.37, 0.04) * mm, "end": v(-5.5, -0.04) * mm});
            skLineSegment(sketch, "E1818", {"start": v(-5.5, -0.04) * mm, "end": v(-5.65, -0.12) * mm});
            skLineSegment(sketch, "E1819", {"start": v(-5.65, -0.12) * mm, "end": v(-5.7, -0.15) * mm});
            skLineSegment(sketch, "E1820", {"start": v(-5.7, -0.15) * mm, "end": v(-5.78, -0.2) * mm});
            skLineSegment(sketch, "E1821", {"start": v(-5.78, -0.2) * mm, "end": v(-5.87, -0.24) * mm});
            skLineSegment(sketch, "E1822", {"start": v(-5.87, -0.24) * mm, "end": v(-5.96, -0.28) * mm});
            skLineSegment(sketch, "E1823", {"start": v(-5.96, -0.28) * mm, "end": v(-6.05, -0.33) * mm});
            skLineSegment(sketch, "E1824", {"start": v(-6.05, -0.33) * mm, "end": v(-6.13, -0.37) * mm});
            skLineSegment(sketch, "E1825", {"start": v(-6.13, -0.37) * mm, "end": v(-6.19, -0.4) * mm});
            skLineSegment(sketch, "E1826", {"start": v(-6.19, -0.4) * mm, "end": v(-6.22, -0.4) * mm});
            skLineSegment(sketch, "E1827", {"start": v(-6.22, -0.4) * mm, "end": v(-6.24, -0.41) * mm});
            skLineSegment(sketch, "E1828", {"start": v(-6.24, -0.41) * mm, "end": v(-6.28, -0.43) * mm});
            skLineSegment(sketch, "E1829", {"start": v(-6.28, -0.43) * mm, "end": v(-6.32, -0.45) * mm});
            skLineSegment(sketch, "E1830", {"start": v(-6.32, -0.45) * mm, "end": v(-6.37, -0.47) * mm});
            skLineSegment(sketch, "E1831", {"start": v(-6.37, -0.47) * mm, "end": v(-6.42, -0.5) * mm});
            skLineSegment(sketch, "E1832", {"start": v(-6.42, -0.5) * mm, "end": v(-6.47, -0.51) * mm});
            skLineSegment(sketch, "E1833", {"start": v(-6.47, -0.51) * mm, "end": v(-6.51, -0.53) * mm});
            skLineSegment(sketch, "E1834", {"start": v(-6.51, -0.53) * mm, "end": v(-6.55, -0.54) * mm});
            skLineSegment(sketch, "E1835", {"start": v(-6.55, -0.54) * mm, "end": v(-6.58, -0.55) * mm});
            skLineSegment(sketch, "E1836", {"start": v(-6.58, -0.55) * mm, "end": v(-6.6, -0.56) * mm});
            skLineSegment(sketch, "E1837", {"start": v(-6.6, -0.56) * mm, "end": v(-6.57, -0.57) * mm});
            skLineSegment(sketch, "E1838", {"start": v(-6.57, -0.57) * mm, "end": v(-6.53, -0.57) * mm});
            skLineSegment(sketch, "E1839", {"start": v(-6.53, -0.57) * mm, "end": v(-6.5, -0.58) * mm});
            skLineSegment(sketch, "E1840", {"start": v(-6.5, -0.58) * mm, "end": v(-6.44, -0.6) * mm});
            skLineSegment(sketch, "E1841", {"start": v(-6.44, -0.6) * mm, "end": v(-6.38, -0.6) * mm});
            skLineSegment(sketch, "E1842", {"start": v(-6.38, -0.6) * mm, "end": v(-6.3, -0.62) * mm});
            skLineSegment(sketch, "E1843", {"start": v(-6.3, -0.62) * mm, "end": v(-6.14, -0.66) * mm});
            skLineSegment(sketch, "E1844", {"start": v(-6.14, -0.66) * mm, "end": v(-6, -0.68) * mm});
            skLineSegment(sketch, "E1845", {"start": v(-6, -0.68) * mm, "end": v(-5.85, -0.7) * mm});
            skLineSegment(sketch, "E1846", {"start": v(-5.85, -0.7) * mm, "end": v(-5.72, -0.7) * mm});
            skLineSegment(sketch, "E1847", {"start": v(-5.72, -0.7) * mm, "end": v(-5.64, -0.7) * mm});
            skLineSegment(sketch, "E1848", {"start": v(-5.64, -0.7) * mm, "end": v(-5.57, -0.7) * mm});
            skLineSegment(sketch, "E1849", {"start": v(-5.57, -0.7) * mm, "end": v(-5.5, -0.68) * mm});
            skLineSegment(sketch, "E1850", {"start": v(-5.5, -0.68) * mm, "end": v(-5.4, -0.66) * mm});
            skLineSegment(sketch, "E1851", {"start": v(-3.45, -0.68) * mm, "end": v(-3.38, -0.66) * mm});
            skLineSegment(sketch, "E1852", {"start": v(-3.38, -0.66) * mm, "end": v(-3.31, -0.64) * mm});
            skLineSegment(sketch, "E1853", {"start": v(-3.31, -0.64) * mm, "end": v(-3.18, -0.57) * mm});
            skLineSegment(sketch, "E1854", {"start": v(-3.18, -0.57) * mm, "end": v(-3.04, -0.5) * mm});
            skLineSegment(sketch, "E1855", {"start": v(-3.04, -0.5) * mm, "end": v(-2.92, -0.45) * mm});
            skLineSegment(sketch, "E1856", {"start": v(-2.92, -0.45) * mm, "end": v(-2.82, -0.42) * mm});
            skLineSegment(sketch, "E1857", {"start": v(-2.82, -0.42) * mm, "end": v(-2.8, -0.4) * mm});
            skLineSegment(sketch, "E1858", {"start": v(-2.8, -0.4) * mm, "end": v(-2.75, -0.4) * mm});
            skLineSegment(sketch, "E1859", {"start": v(-2.75, -0.4) * mm, "end": v(-2.7, -0.37) * mm});
            skLineSegment(sketch, "E1860", {"start": v(-2.7, -0.37) * mm, "end": v(-2.65, -0.36) * mm});
            skLineSegment(sketch, "E1861", {"start": v(-2.65, -0.36) * mm, "end": v(-2.48, -0.3) * mm});
            skLineSegment(sketch, "E1862", {"start": v(-2.48, -0.3) * mm, "end": v(-2.31, -0.26) * mm});
            skLineSegment(sketch, "E1863", {"start": v(-2.31, -0.26) * mm, "end": v(-2.13, -0.23) * mm});
            skLineSegment(sketch, "E1864", {"start": v(-2.13, -0.23) * mm, "end": v(-1.93, -0.21) * mm});
            skLineSegment(sketch, "E1865", {"start": v(-1.93, -0.21) * mm, "end": v(-1.78, -0.2) * mm});
            skLineSegment(sketch, "E1866", {"start": v(-1.78, -0.2) * mm, "end": v(-1.65, -0.2) * mm});
            skLineSegment(sketch, "E1867", {"start": v(-1.65, -0.2) * mm, "end": v(-1.52, -0.22) * mm});
            skLineSegment(sketch, "E1868", {"start": v(-1.52, -0.22) * mm, "end": v(-1.39, -0.23) * mm});
            skLineSegment(sketch, "E1869", {"start": v(-1.39, -0.23) * mm, "end": v(-1.34, -0.24) * mm});
            skLineSegment(sketch, "E1870", {"start": v(-1.34, -0.24) * mm, "end": v(-1.3, -0.24) * mm});
            skLineSegment(sketch, "E1871", {"start": v(-1.3, -0.24) * mm, "end": v(-1.27, -0.25) * mm});
            skLineSegment(sketch, "E1872", {"start": v(-1.27, -0.25) * mm, "end": v(-1.26, -0.25) * mm});
            skLineSegment(sketch, "E1873", {"start": v(-1.26, -0.25) * mm, "end": v(-1.26, -0.23) * mm});
            skLineSegment(sketch, "E1874", {"start": v(-1.26, -0.23) * mm, "end": v(-1.27, -0.2) * mm});
            skLineSegment(sketch, "E1875", {"start": v(-1.27, -0.2) * mm, "end": v(-1.28, -0.15) * mm});
            skLineSegment(sketch, "E1876", {"start": v(-1.28, -0.15) * mm, "end": v(-1.3, -0.1) * mm});
            skLineSegment(sketch, "E1877", {"start": v(-1.3, -0.1) * mm, "end": v(-1.33, -0.05) * mm});
            skLineSegment(sketch, "E1878", {"start": v(-1.33, -0.05) * mm, "end": v(-1.35, 0) * mm});
            skLineSegment(sketch, "E1879", {"start": v(-1.35, 0) * mm, "end": v(-1.37, 0.04) * mm});
            skLineSegment(sketch, "E1880", {"start": v(-1.37, 0.04) * mm, "end": v(-1.4, 0.07) * mm});
            skLineSegment(sketch, "E1881", {"start": v(-1.4, 0.07) * mm, "end": v(-1.43, 0.1) * mm});
            skLineSegment(sketch, "E1882", {"start": v(-1.43, 0.1) * mm, "end": v(-1.47, 0.12) * mm});
            skLineSegment(sketch, "E1883", {"start": v(-1.47, 0.12) * mm, "end": v(-1.52, 0.15) * mm});
            skLineSegment(sketch, "E1884", {"start": v(-1.52, 0.15) * mm, "end": v(-1.58, 0.18) * mm});
            skLineSegment(sketch, "E1885", {"start": v(-1.58, 0.18) * mm, "end": v(-1.66, 0.2) * mm});
            skLineSegment(sketch, "E1886", {"start": v(-1.66, 0.2) * mm, "end": v(-1.76, 0.24) * mm});
            skLineSegment(sketch, "E1887", {"start": v(-1.76, 0.24) * mm, "end": v(-1.87, 0.28) * mm});
            skLineSegment(sketch, "E1888", {"start": v(-1.87, 0.28) * mm, "end": v(-2.01, 0.32) * mm});
            skLineSegment(sketch, "E1889", {"start": v(-2.01, 0.32) * mm, "end": v(-2.25, 0.38) * mm});
            skLineSegment(sketch, "E1890", {"start": v(-2.25, 0.38) * mm, "end": v(-2.44, 0.42) * mm});
            skLineSegment(sketch, "E1891", {"start": v(-2.44, 0.42) * mm, "end": v(-2.61, 0.44) * mm});
            skLineSegment(sketch, "E1892", {"start": v(-2.61, 0.44) * mm, "end": v(-2.8, 0.44) * mm});
            skLineSegment(sketch, "E1893", {"start": v(-2.8, 0.44) * mm, "end": v(-2.95, 0.43) * mm});
            skLineSegment(sketch, "E1894", {"start": v(-2.95, 0.43) * mm, "end": v(-3.07, 0.41) * mm});
            skLineSegment(sketch, "E1895", {"start": v(-3.07, 0.41) * mm, "end": v(-3.18, 0.38) * mm});
            skLineSegment(sketch, "E1896", {"start": v(-3.18, 0.38) * mm, "end": v(-3.3, 0.34) * mm});
            skLineSegment(sketch, "E1897", {"start": v(-3.3, 0.34) * mm, "end": v(-3.41, 0.28) * mm});
            skLineSegment(sketch, "E1898", {"start": v(-3.41, 0.28) * mm, "end": v(-3.55, 0.2) * mm});
            skLineSegment(sketch, "E1899", {"start": v(-3.55, 0.2) * mm, "end": v(-3.68, 0.12) * mm});
            skLineSegment(sketch, "E1900", {"start": v(-3.68, 0.12) * mm, "end": v(-3.77, 0.05) * mm});
            skLineSegment(sketch, "E1901", {"start": v(-3.77, 0.05) * mm, "end": v(-3.87, -0.03) * mm});
            skLineSegment(sketch, "E1902", {"start": v(-3.87, -0.03) * mm, "end": v(-3.96, -0.12) * mm});
            skLineSegment(sketch, "E1903", {"start": v(-3.96, -0.12) * mm, "end": v(-4.05, -0.2) * mm});
            skLineSegment(sketch, "E1904", {"start": v(-4.05, -0.2) * mm, "end": v(-4.1, -0.26) * mm});
            skLineSegment(sketch, "E1905", {"start": v(-4.1, -0.26) * mm, "end": v(-4.13, -0.3) * mm});
            skLineSegment(sketch, "E1906", {"start": v(-4.13, -0.3) * mm, "end": v(-4.16, -0.35) * mm});
            skLineSegment(sketch, "E1907", {"start": v(-4.16, -0.35) * mm, "end": v(-4.2, -0.4) * mm});
            skLineSegment(sketch, "E1908", {"start": v(-4.2, -0.4) * mm, "end": v(-4.25, -0.48) * mm});
            skLineSegment(sketch, "E1909", {"start": v(-4.25, -0.48) * mm, "end": v(-4.3, -0.57) * mm});
            skLineSegment(sketch, "E1910", {"start": v(-4.3, -0.57) * mm, "end": v(-4.32, -0.63) * mm});
            skLineSegment(sketch, "E1911", {"start": v(-4.32, -0.63) * mm, "end": v(-4.32, -0.64) * mm});
            skLineSegment(sketch, "E1912", {"start": v(-4.32, -0.64) * mm, "end": v(-4.32, -0.64) * mm});
            skLineSegment(sketch, "E1913", {"start": v(-4.32, -0.64) * mm, "end": v(-4.31, -0.65) * mm});
            skLineSegment(sketch, "E1914", {"start": v(-4.31, -0.65) * mm, "end": v(-4.3, -0.65) * mm});
            skLineSegment(sketch, "E1915", {"start": v(-4.3, -0.65) * mm, "end": v(-4.27, -0.66) * mm});
            skLineSegment(sketch, "E1916", {"start": v(-4.27, -0.66) * mm, "end": v(-4.24, -0.66) * mm});
            skLineSegment(sketch, "E1917", {"start": v(-4.24, -0.66) * mm, "end": v(-4.2, -0.67) * mm});
            skLineSegment(sketch, "E1918", {"start": v(-4.2, -0.67) * mm, "end": v(-4.14, -0.67) * mm});
            skLineSegment(sketch, "E1919", {"start": v(-4.14, -0.67) * mm, "end": v(-3.95, -0.68) * mm});
            skLineSegment(sketch, "E1920", {"start": v(-3.95, -0.68) * mm, "end": v(-3.75, -0.69) * mm});
            skLineSegment(sketch, "E1921", {"start": v(-3.75, -0.69) * mm, "end": v(-3.58, -0.69) * mm});
            skLineSegment(sketch, "E1922", {"start": v(-3.58, -0.69) * mm, "end": v(-3.45, -0.68) * mm});
            skLineSegment(sketch, "E1923", {"start": v(-0.68, -0.55) * mm, "end": v(-0.64, -0.53) * mm});
            skLineSegment(sketch, "E1924", {"start": v(-0.64, -0.53) * mm, "end": v(-0.6, -0.5) * mm});
            skLineSegment(sketch, "E1925", {"start": v(-0.6, -0.5) * mm, "end": v(-0.58, -0.46) * mm});
            skLineSegment(sketch, "E1926", {"start": v(-0.58, -0.46) * mm, "end": v(-0.55, -0.43) * mm});
            skLineSegment(sketch, "E1927", {"start": v(-0.55, -0.43) * mm, "end": v(-0.53, -0.41) * mm});
            skLineSegment(sketch, "E1928", {"start": v(-0.53, -0.41) * mm, "end": v(-0.52, -0.4) * mm});
            skLineSegment(sketch, "E1929", {"start": v(-0.52, -0.4) * mm, "end": v(-0.5, -0.4) * mm});
            skLineSegment(sketch, "E1930", {"start": v(-0.5, -0.4) * mm, "end": v(-0.48, -0.4) * mm});
            skLineSegment(sketch, "E1931", {"start": v(-0.48, -0.4) * mm, "end": v(-0.47, -0.4) * mm});
            skLineSegment(sketch, "E1932", {"start": v(-0.47, -0.4) * mm, "end": v(-0.45, -0.41) * mm});
            skLineSegment(sketch, "E1933", {"start": v(-0.45, -0.41) * mm, "end": v(-0.31, -0.48) * mm});
            skLineSegment(sketch, "E1934", {"start": v(-0.31, -0.48) * mm, "end": v(-0.16, -0.52) * mm});
            skLineSegment(sketch, "E1935", {"start": v(-0.16, -0.52) * mm, "end": v(-0.02, -0.53) * mm});
            skLineSegment(sketch, "E1936", {"start": v(-0.02, -0.53) * mm, "end": v(0.1, -0.5) * mm});
            skLineSegment(sketch, "E1937", {"start": v(0.1, -0.5) * mm, "end": v(0.13, -0.48) * mm});
            skLineSegment(sketch, "E1938", {"start": v(0.13, -0.48) * mm, "end": v(0.17, -0.46) * mm});
            skLineSegment(sketch, "E1939", {"start": v(0.17, -0.46) * mm, "end": v(0.2, -0.42) * mm});
            skLineSegment(sketch, "E1940", {"start": v(0.2, -0.42) * mm, "end": v(0.25, -0.38) * mm});
            skLineSegment(sketch, "E1941", {"start": v(0.25, -0.38) * mm, "end": v(0.3, -0.33) * mm});
            skLineSegment(sketch, "E1942", {"start": v(0.3, -0.33) * mm, "end": v(0.34, -0.3) * mm});
            skLineSegment(sketch, "E1943", {"start": v(0.34, -0.3) * mm, "end": v(0.37, -0.26) * mm});
            skLineSegment(sketch, "E1944", {"start": v(0.37, -0.26) * mm, "end": v(0.38, -0.23) * mm});
            skLineSegment(sketch, "E1945", {"start": v(0.38, -0.23) * mm, "end": v(0.4, -0.19) * mm});
            skLineSegment(sketch, "E1946", {"start": v(0.4, -0.19) * mm, "end": v(0.4, -0.12) * mm});
            skLineSegment(sketch, "E1947", {"start": v(0.4, -0.12) * mm, "end": v(0.38, -0.02) * mm});
            skLineSegment(sketch, "E1948", {"start": v(0.38, -0.02) * mm, "end": v(0.36, 0.09) * mm});
            skLineSegment(sketch, "E1949", {"start": v(0.36, 0.09) * mm, "end": v(0.34, 0.2) * mm});
            skLineSegment(sketch, "E1950", {"start": v(0.34, 0.2) * mm, "end": v(0.32, 0.32) * mm});
            skLineSegment(sketch, "E1951", {"start": v(0.32, 0.32) * mm, "end": v(0.3, 0.39) * mm});
            skLineSegment(sketch, "E1952", {"start": v(0.3, 0.39) * mm, "end": v(0.3, 0.43) * mm});
            skLineSegment(sketch, "E1953", {"start": v(0.3, 0.43) * mm, "end": v(0.28, 0.44) * mm});
            skLineSegment(sketch, "E1954", {"start": v(0.28, 0.44) * mm, "end": v(0.27, 0.44) * mm});
            skLineSegment(sketch, "E1955", {"start": v(0.27, 0.44) * mm, "end": v(0.17, 0.43) * mm});
            skLineSegment(sketch, "E1956", {"start": v(0.17, 0.43) * mm, "end": v(0.1, 0.42) * mm});
            skLineSegment(sketch, "E1957", {"start": v(0.1, 0.42) * mm, "end": v(0.04, 0.42) * mm});
            skLineSegment(sketch, "E1958", {"start": v(0.04, 0.42) * mm, "end": v(-0.01, 0.43) * mm});
            skLineSegment(sketch, "E1959", {"start": v(-0.01, 0.43) * mm, "end": v(-0.07, 0.44) * mm});
            skLineSegment(sketch, "E1960", {"start": v(-0.07, 0.44) * mm, "end": v(-0.12, 0.4) * mm});
            skLineSegment(sketch, "E1961", {"start": v(-0.12, 0.4) * mm, "end": v(-0.14, 0.38) * mm});
            skLineSegment(sketch, "E1962", {"start": v(-0.14, 0.38) * mm, "end": v(-0.17, 0.36) * mm});
            skLineSegment(sketch, "E1963", {"start": v(-0.17, 0.36) * mm, "end": v(-0.2, 0.34) * mm});
            skLineSegment(sketch, "E1964", {"start": v(-0.2, 0.34) * mm, "end": v(-0.23, 0.33) * mm});
            skLineSegment(sketch, "E1965", {"start": v(-0.23, 0.33) * mm, "end": v(-0.28, 0.31) * mm});
            skLineSegment(sketch, "E1966", {"start": v(-0.28, 0.31) * mm, "end": v(-0.32, 0.3) * mm});
            skLineSegment(sketch, "E1967", {"start": v(-0.32, 0.3) * mm, "end": v(-0.38, 0.3) * mm});
            skLineSegment(sketch, "E1968", {"start": v(-0.38, 0.3) * mm, "end": v(-0.47, 0.29) * mm});
            skLineSegment(sketch, "E1969", {"start": v(-0.47, 0.29) * mm, "end": v(-0.56, 0.29) * mm});
            skLineSegment(sketch, "E1970", {"start": v(-0.56, 0.29) * mm, "end": v(-0.62, 0.29) * mm});
            skLineSegment(sketch, "E1971", {"start": v(-0.62, 0.29) * mm, "end": v(-0.67, 0.3) * mm});
            skLineSegment(sketch, "E1972", {"start": v(-0.67, 0.3) * mm, "end": v(-0.71, 0.3) * mm});
            skLineSegment(sketch, "E1973", {"start": v(-0.71, 0.3) * mm, "end": v(-0.77, 0.32) * mm});
            skLineSegment(sketch, "E1974", {"start": v(-0.77, 0.32) * mm, "end": v(-0.83, 0.35) * mm});
            skLineSegment(sketch, "E1975", {"start": v(-0.83, 0.35) * mm, "end": v(-0.9, 0.38) * mm});
            skLineSegment(sketch, "E1976", {"start": v(-0.9, 0.38) * mm, "end": v(-0.95, 0.41) * mm});
            skLineSegment(sketch, "E1977", {"start": v(-0.95, 0.41) * mm, "end": v(-0.98, 0.43) * mm});
            skLineSegment(sketch, "E1978", {"start": v(-0.98, 0.43) * mm, "end": v(-0.99, 0.39) * mm});
            skLineSegment(sketch, "E1979", {"start": v(-0.99, 0.39) * mm, "end": v(-0.99, 0.34) * mm});
            skLineSegment(sketch, "E1980", {"start": v(-0.99, 0.34) * mm, "end": v(-1, 0.24) * mm});
            skLineSegment(sketch, "E1981", {"start": v(-1, 0.24) * mm, "end": v(-1, 0.1) * mm});
            skLineSegment(sketch, "E1982", {"start": v(-1, 0.1) * mm, "end": v(-1, -0.04) * mm});
            skLineSegment(sketch, "E1983", {"start": v(-1, -0.04) * mm, "end": v(-1, -0.2) * mm});
            skLineSegment(sketch, "E1984", {"start": v(-1, -0.2) * mm, "end": v(-1, -0.33) * mm});
            skLineSegment(sketch, "E1985", {"start": v(-1, -0.33) * mm, "end": v(-0.99, -0.43) * mm});
            skLineSegment(sketch, "E1986", {"start": v(-0.99, -0.43) * mm, "end": v(-0.99, -0.47) * mm});
            skLineSegment(sketch, "E1987", {"start": v(-0.99, -0.47) * mm, "end": v(-0.98, -0.5) * mm});
            skLineSegment(sketch, "E1988", {"start": v(-0.98, -0.5) * mm, "end": v(-0.96, -0.51) * mm});
            skLineSegment(sketch, "E1989", {"start": v(-0.96, -0.51) * mm, "end": v(-0.92, -0.53) * mm});
            skLineSegment(sketch, "E1990", {"start": v(-0.92, -0.53) * mm, "end": v(-0.86, -0.55) * mm});
            skLineSegment(sketch, "E1991", {"start": v(-0.86, -0.55) * mm, "end": v(-0.8, -0.56) * mm});
            skLineSegment(sketch, "E1992", {"start": v(-0.8, -0.56) * mm, "end": v(-0.76, -0.57) * mm});
            skLineSegment(sketch, "E1993", {"start": v(-0.76, -0.57) * mm, "end": v(-0.72, -0.56) * mm});
            skLineSegment(sketch, "E1994", {"start": v(-0.72, -0.56) * mm, "end": v(-0.68, -0.55) * mm});
            skLineSegment(sketch, "E1995", {"start": v(4.26, 0.27) * mm, "end": v(4.35, 0.28) * mm});
            skLineSegment(sketch, "E1996", {"start": v(4.35, 0.28) * mm, "end": v(4.35, 0.33) * mm});
            skLineSegment(sketch, "E1997", {"start": v(4.35, 0.33) * mm, "end": v(4.34, 0.43) * mm});
            skLineSegment(sketch, "E1998", {"start": v(4.34, 0.43) * mm, "end": v(4.3, 0.54) * mm});
            skLineSegment(sketch, "E1999", {"start": v(4.3, 0.54) * mm, "end": v(4.24, 0.65) * mm});
            skLineSegment(sketch, "E2000", {"start": v(4.24, 0.65) * mm, "end": v(4.17, 0.76) * mm});
            skLineSegment(sketch, "E2001", {"start": v(4.17, 0.76) * mm, "end": v(4.14, 0.79) * mm});
            skLineSegment(sketch, "E2002", {"start": v(4.14, 0.79) * mm, "end": v(4.1, 0.83) * mm});
            skLineSegment(sketch, "E2003", {"start": v(4.1, 0.83) * mm, "end": v(4.04, 0.87) * mm});
            skLineSegment(sketch, "E2004", {"start": v(4.04, 0.87) * mm, "end": v(3.97, 0.92) * mm});
            skLineSegment(sketch, "E2005", {"start": v(3.97, 0.92) * mm, "end": v(3.9, 0.96) * mm});
            skLineSegment(sketch, "E2006", {"start": v(3.9, 0.96) * mm, "end": v(3.84, 1) * mm});
            skLineSegment(sketch, "E2007", {"start": v(3.84, 1) * mm, "end": v(3.78, 1.04) * mm});
            skLineSegment(sketch, "E2008", {"start": v(3.78, 1.04) * mm, "end": v(3.73, 1.07) * mm});
            skLineSegment(sketch, "E2009", {"start": v(3.73, 1.07) * mm, "end": v(3.56, 1.13) * mm});
            skLineSegment(sketch, "E2010", {"start": v(3.56, 1.13) * mm, "end": v(3.38, 1.17) * mm});
            skLineSegment(sketch, "E2011", {"start": v(3.38, 1.17) * mm, "end": v(3.18, 1.2) * mm});
            skLineSegment(sketch, "E2012", {"start": v(3.18, 1.2) * mm, "end": v(2.98, 1.2) * mm});
            skLineSegment(sketch, "E2013", {"start": v(2.98, 1.2) * mm, "end": v(2.85, 1.18) * mm});
            skLineSegment(sketch, "E2014", {"start": v(2.85, 1.18) * mm, "end": v(2.7, 1.17) * mm});
            skLineSegment(sketch, "E2015", {"start": v(2.7, 1.17) * mm, "end": v(2.56, 1.15) * mm});
            skLineSegment(sketch, "E2016", {"start": v(2.56, 1.15) * mm, "end": v(2.47, 1.14) * mm});
            skLineSegment(sketch, "E2017", {"start": v(2.47, 1.14) * mm, "end": v(2.39, 1.11) * mm});
            skLineSegment(sketch, "E2018", {"start": v(2.39, 1.11) * mm, "end": v(2.29, 1.08) * mm});
            skLineSegment(sketch, "E2019", {"start": v(2.29, 1.08) * mm, "end": v(2.16, 1.04) * mm});
            skLineSegment(sketch, "E2020", {"start": v(2.16, 1.04) * mm, "end": v(2.03, 0.99) * mm});
            skLineSegment(sketch, "E2021", {"start": v(2.03, 0.99) * mm, "end": v(1.89, 0.94) * mm});
            skLineSegment(sketch, "E2022", {"start": v(1.89, 0.94) * mm, "end": v(1.75, 0.88) * mm});
            skLineSegment(sketch, "E2023", {"start": v(1.75, 0.88) * mm, "end": v(1.62, 0.83) * mm});
            skLineSegment(sketch, "E2024", {"start": v(1.62, 0.83) * mm, "end": v(1.5, 0.78) * mm});
            skLineSegment(sketch, "E2025", {"start": v(1.5, 0.78) * mm, "end": v(1.4, 0.73) * mm});
            skLineSegment(sketch, "E2026", {"start": v(1.4, 0.73) * mm, "end": v(1.27, 0.67) * mm});
            skLineSegment(sketch, "E2027", {"start": v(1.27, 0.67) * mm, "end": v(1.17, 0.64) * mm});
            skLineSegment(sketch, "E2028", {"start": v(1.17, 0.64) * mm, "end": v(1.12, 0.61) * mm});
            skLineSegment(sketch, "E2029", {"start": v(1.12, 0.61) * mm, "end": v(1.11, 0.6) * mm});
            skLineSegment(sketch, "E2030", {"start": v(1.11, 0.6) * mm, "end": v(1.14, 0.6) * mm});
            skLineSegment(sketch, "E2031", {"start": v(1.14, 0.6) * mm, "end": v(1.2, 0.61) * mm});
            skLineSegment(sketch, "E2032", {"start": v(1.2, 0.61) * mm, "end": v(1.31, 0.62) * mm});
            skLineSegment(sketch, "E2033", {"start": v(1.31, 0.62) * mm, "end": v(1.44, 0.64) * mm});
            skLineSegment(sketch, "E2034", {"start": v(1.44, 0.64) * mm, "end": v(1.58, 0.65) * mm});
            skLineSegment(sketch, "E2035", {"start": v(1.58, 0.65) * mm, "end": v(1.7, 0.66) * mm});
            skLineSegment(sketch, "E2036", {"start": v(1.7, 0.66) * mm, "end": v(1.83, 0.66) * mm});
            skLineSegment(sketch, "E2037", {"start": v(1.83, 0.66) * mm, "end": v(2.01, 0.66) * mm});
            skLineSegment(sketch, "E2038", {"start": v(2.01, 0.66) * mm, "end": v(2.23, 0.65) * mm});
            skLineSegment(sketch, "E2039", {"start": v(2.23, 0.65) * mm, "end": v(2.43, 0.63) * mm});
            skLineSegment(sketch, "E2040", {"start": v(2.43, 0.63) * mm, "end": v(2.58, 0.62) * mm});
            skLineSegment(sketch, "E2041", {"start": v(2.58, 0.62) * mm, "end": v(2.7, 0.6) * mm});
            skLineSegment(sketch, "E2042", {"start": v(2.7, 0.6) * mm, "end": v(2.84, 0.56) * mm});
            skLineSegment(sketch, "E2043", {"start": v(2.84, 0.56) * mm, "end": v(3, 0.51) * mm});
            skLineSegment(sketch, "E2044", {"start": v(3, 0.51) * mm, "end": v(3.1, 0.48) * mm});
            skLineSegment(sketch, "E2045", {"start": v(3.1, 0.48) * mm, "end": v(3.2, 0.44) * mm});
            skLineSegment(sketch, "E2046", {"start": v(3.2, 0.44) * mm, "end": v(3.32, 0.4) * mm});
            skLineSegment(sketch, "E2047", {"start": v(3.32, 0.4) * mm, "end": v(3.4, 0.36) * mm});
            skLineSegment(sketch, "E2048", {"start": v(3.4, 0.36) * mm, "end": v(3.46, 0.34) * mm});
            skLineSegment(sketch, "E2049", {"start": v(3.46, 0.34) * mm, "end": v(3.5, 0.32) * mm});
            skLineSegment(sketch, "E2050", {"start": v(3.5, 0.32) * mm, "end": v(3.54, 0.31) * mm});
            skLineSegment(sketch, "E2051", {"start": v(3.54, 0.31) * mm, "end": v(3.73, 0.26) * mm});
            skLineSegment(sketch, "E2052", {"start": v(3.73, 0.26) * mm, "end": v(3.9, 0.24) * mm});
            skLineSegment(sketch, "E2053", {"start": v(3.9, 0.24) * mm, "end": v(4.06, 0.24) * mm});
            skLineSegment(sketch, "E2054", {"start": v(4.06, 0.24) * mm, "end": v(4.26, 0.27) * mm});
            skLineSegment(sketch, "E2055", {"start": v(4.8, 0.45) * mm, "end": v(4.86, 0.49) * mm});
            skLineSegment(sketch, "E2056", {"start": v(4.86, 0.49) * mm, "end": v(4.91, 0.53) * mm});
            skLineSegment(sketch, "E2057", {"start": v(4.91, 0.53) * mm, "end": v(4.96, 0.57) * mm});
            skLineSegment(sketch, "E2058", {"start": v(4.96, 0.57) * mm, "end": v(5, 0.6) * mm});
            skLineSegment(sketch, "E2059", {"start": v(5, 0.6) * mm, "end": v(5.05, 0.63) * mm});
            skLineSegment(sketch, "E2060", {"start": v(5.05, 0.63) * mm, "end": v(5.1, 0.67) * mm});
            skLineSegment(sketch, "E2061", {"start": v(5.1, 0.67) * mm, "end": v(5.16, 0.71) * mm});
            skLineSegment(sketch, "E2062", {"start": v(5.16, 0.71) * mm, "end": v(5.21, 0.75) * mm});
            skLineSegment(sketch, "E2063", {"start": v(5.21, 0.75) * mm, "end": v(5.27, 0.8) * mm});
            skLineSegment(sketch, "E2064", {"start": v(5.27, 0.8) * mm, "end": v(5.32, 0.83) * mm});
            skLineSegment(sketch, "E2065", {"start": v(5.32, 0.83) * mm, "end": v(5.36, 0.86) * mm});
            skLineSegment(sketch, "E2066", {"start": v(5.36, 0.86) * mm, "end": v(5.4, 0.88) * mm});
            skLineSegment(sketch, "E2067", {"start": v(5.4, 0.88) * mm, "end": v(5.44, 0.91) * mm});
            skLineSegment(sketch, "E2068", {"start": v(5.44, 0.91) * mm, "end": v(5.48, 0.94) * mm});
            skLineSegment(sketch, "E2069", {"start": v(5.48, 0.94) * mm, "end": v(5.54, 0.97) * mm});
            skLineSegment(sketch, "E2070", {"start": v(5.54, 0.97) * mm, "end": v(5.61, 1) * mm});
            skLineSegment(sketch, "E2071", {"start": v(5.61, 1) * mm, "end": v(5.7, 1.05) * mm});
            skLineSegment(sketch, "E2072", {"start": v(5.7, 1.05) * mm, "end": v(5.77, 1.07) * mm});
            skLineSegment(sketch, "E2073", {"start": v(5.77, 1.07) * mm, "end": v(5.9, 1.11) * mm});
            skLineSegment(sketch, "E2074", {"start": v(5.9, 1.11) * mm, "end": v(6.05, 1.14) * mm});
            skLineSegment(sketch, "E2075", {"start": v(6.05, 1.14) * mm, "end": v(6.2, 1.15) * mm});
            skLineSegment(sketch, "E2076", {"start": v(6.2, 1.15) * mm, "end": v(6.33, 1.15) * mm});
            skLineSegment(sketch, "E2077", {"start": v(6.33, 1.15) * mm, "end": v(6.43, 1.14) * mm});
            skLineSegment(sketch, "E2078", {"start": v(6.43, 1.14) * mm, "end": v(6.36, 1.18) * mm});
            skLineSegment(sketch, "E2079", {"start": v(6.36, 1.18) * mm, "end": v(6.33, 1.2) * mm});
            skLineSegment(sketch, "E2080", {"start": v(6.33, 1.2) * mm, "end": v(6.3, 1.22) * mm});
            skLineSegment(sketch, "E2081", {"start": v(6.3, 1.22) * mm, "end": v(6.27, 1.24) * mm});
            skLineSegment(sketch, "E2082", {"start": v(6.27, 1.24) * mm, "end": v(6.25, 1.26) * mm});
            skLineSegment(sketch, "E2083", {"start": v(6.25, 1.26) * mm, "end": v(6.17, 1.3) * mm});
            skLineSegment(sketch, "E2084", {"start": v(6.17, 1.3) * mm, "end": v(6.04, 1.36) * mm});
            skLineSegment(sketch, "E2085", {"start": v(6.04, 1.36) * mm, "end": v(5.89, 1.41) * mm});
            skLineSegment(sketch, "E2086", {"start": v(5.89, 1.41) * mm, "end": v(5.72, 1.46) * mm});
            skLineSegment(sketch, "E2087", {"start": v(5.72, 1.46) * mm, "end": v(5.46, 1.52) * mm});
            skLineSegment(sketch, "E2088", {"start": v(5.46, 1.52) * mm, "end": v(5.24, 1.55) * mm});
            skLineSegment(sketch, "E2089", {"start": v(5.24, 1.55) * mm, "end": v(5.04, 1.57) * mm});
            skLineSegment(sketch, "E2090", {"start": v(5.04, 1.57) * mm, "end": v(4.88, 1.56) * mm});
            skLineSegment(sketch, "E2091", {"start": v(4.88, 1.56) * mm, "end": v(4.79, 1.54) * mm});
            skLineSegment(sketch, "E2092", {"start": v(4.79, 1.54) * mm, "end": v(4.7, 1.52) * mm});
            skLineSegment(sketch, "E2093", {"start": v(4.7, 1.52) * mm, "end": v(4.61, 1.49) * mm});
            skLineSegment(sketch, "E2094", {"start": v(4.61, 1.49) * mm, "end": v(4.48, 1.43) * mm});
            skLineSegment(sketch, "E2095", {"start": v(4.48, 1.43) * mm, "end": v(4.36, 1.38) * mm});
            skLineSegment(sketch, "E2096", {"start": v(4.36, 1.38) * mm, "end": v(4.25, 1.35) * mm});
            skLineSegment(sketch, "E2097", {"start": v(4.25, 1.35) * mm, "end": v(4.15, 1.34) * mm});
            skLineSegment(sketch, "E2098", {"start": v(4.15, 1.34) * mm, "end": v(4.02, 1.33) * mm});
            skLineSegment(sketch, "E2099", {"start": v(4.02, 1.33) * mm, "end": v(3.9, 1.33) * mm});
            skLineSegment(sketch, "E2100", {"start": v(3.9, 1.33) * mm, "end": v(3.95, 1.3) * mm});
            skLineSegment(sketch, "E2101", {"start": v(3.95, 1.3) * mm, "end": v(3.98, 1.28) * mm});
            skLineSegment(sketch, "E2102", {"start": v(3.98, 1.28) * mm, "end": v(4, 1.27) * mm});
            skLineSegment(sketch, "E2103", {"start": v(4, 1.27) * mm, "end": v(4.02, 1.26) * mm});
            skLineSegment(sketch, "E2104", {"start": v(4.02, 1.26) * mm, "end": v(4.03, 1.25) * mm});
            skLineSegment(sketch, "E2105", {"start": v(4.03, 1.25) * mm, "end": v(4.04, 1.24) * mm});
            skLineSegment(sketch, "E2106", {"start": v(4.04, 1.24) * mm, "end": v(4.07, 1.23) * mm});
            skLineSegment(sketch, "E2107", {"start": v(4.07, 1.23) * mm, "end": v(4.1, 1.2) * mm});
            skLineSegment(sketch, "E2108", {"start": v(4.1, 1.2) * mm, "end": v(4.15, 1.18) * mm});
            skLineSegment(sketch, "E2109", {"start": v(4.15, 1.18) * mm, "end": v(4.28, 1.11) * mm});
            skLineSegment(sketch, "E2110", {"start": v(4.28, 1.11) * mm, "end": v(4.36, 1.06) * mm});
            skLineSegment(sketch, "E2111", {"start": v(4.36, 1.06) * mm, "end": v(4.43, 1.02) * mm});
            skLineSegment(sketch, "E2112", {"start": v(4.43, 1.02) * mm, "end": v(4.49, 0.96) * mm});
            skLineSegment(sketch, "E2113", {"start": v(4.49, 0.96) * mm, "end": v(4.55, 0.9) * mm});
            skLineSegment(sketch, "E2114", {"start": v(4.55, 0.9) * mm, "end": v(4.6, 0.86) * mm});
            skLineSegment(sketch, "E2115", {"start": v(4.6, 0.86) * mm, "end": v(4.62, 0.8) * mm});
            skLineSegment(sketch, "E2116", {"start": v(4.62, 0.8) * mm, "end": v(4.64, 0.74) * mm});
            skLineSegment(sketch, "E2117", {"start": v(4.64, 0.74) * mm, "end": v(4.66, 0.7) * mm});
            skLineSegment(sketch, "E2118", {"start": v(4.66, 0.7) * mm, "end": v(4.67, 0.65) * mm});
            skLineSegment(sketch, "E2119", {"start": v(4.67, 0.65) * mm, "end": v(4.67, 0.59) * mm});
            skLineSegment(sketch, "E2120", {"start": v(4.67, 0.59) * mm, "end": v(4.67, 0.5) * mm});
            skLineSegment(sketch, "E2121", {"start": v(4.67, 0.5) * mm, "end": v(4.67, 0.45) * mm});
            skLineSegment(sketch, "E2122", {"start": v(4.67, 0.45) * mm, "end": v(4.67, 0.4) * mm});
            skLineSegment(sketch, "E2123", {"start": v(4.67, 0.4) * mm, "end": v(4.67, 0.37) * mm});
            skLineSegment(sketch, "E2124", {"start": v(4.67, 0.37) * mm, "end": v(4.68, 0.35) * mm});
            skLineSegment(sketch, "E2125", {"start": v(4.68, 0.35) * mm, "end": v(4.69, 0.36) * mm});
            skLineSegment(sketch, "E2126", {"start": v(4.69, 0.36) * mm, "end": v(4.72, 0.38) * mm});
            skLineSegment(sketch, "E2127", {"start": v(4.72, 0.38) * mm, "end": v(4.76, 0.4) * mm});
            skLineSegment(sketch, "E2128", {"start": v(4.76, 0.4) * mm, "end": v(4.8, 0.45) * mm});
            skLineSegment(sketch, "E2129", {"start": v(-5.46, 0.5) * mm, "end": v(-5.46, 0.5) * mm});
            skLineSegment(sketch, "E2130", {"start": v(-5.46, 0.5) * mm, "end": v(-5.46, 0.52) * mm});
            skLineSegment(sketch, "E2131", {"start": v(-5.46, 0.52) * mm, "end": v(-5.47, 0.55) * mm});
            skLineSegment(sketch, "E2132", {"start": v(-5.47, 0.55) * mm, "end": v(-5.48, 0.58) * mm});
            skLineSegment(sketch, "E2133", {"start": v(-5.48, 0.58) * mm, "end": v(-5.5, 0.65) * mm});
            skLineSegment(sketch, "E2134", {"start": v(-5.5, 0.65) * mm, "end": v(-5.51, 0.72) * mm});
            skLineSegment(sketch, "E2135", {"start": v(-5.51, 0.72) * mm, "end": v(-5.5, 0.8) * mm});
            skLineSegment(sketch, "E2136", {"start": v(-5.5, 0.8) * mm, "end": v(-5.5, 0.88) * mm});
            skLineSegment(sketch, "E2137", {"start": v(-5.5, 0.88) * mm, "end": v(-5.46, 1) * mm});
            skLineSegment(sketch, "E2138", {"start": v(-5.46, 1) * mm, "end": v(-5.42, 1.11) * mm});
            skLineSegment(sketch, "E2139", {"start": v(-5.42, 1.11) * mm, "end": v(-5.36, 1.2) * mm});
            skLineSegment(sketch, "E2140", {"start": v(-5.36, 1.2) * mm, "end": v(-5.28, 1.3) * mm});
            skLineSegment(sketch, "E2141", {"start": v(-5.28, 1.3) * mm, "end": v(-5.19, 1.4) * mm});
            skLineSegment(sketch, "E2142", {"start": v(-5.19, 1.4) * mm, "end": v(-5.09, 1.48) * mm});
            skLineSegment(sketch, "E2143", {"start": v(-5.09, 1.48) * mm, "end": v(-4.97, 1.55) * mm});
            skLineSegment(sketch, "E2144", {"start": v(-4.97, 1.55) * mm, "end": v(-4.83, 1.6) * mm});
            skLineSegment(sketch, "E2145", {"start": v(-4.83, 1.6) * mm, "end": v(-4.8, 1.62) * mm});
            skLineSegment(sketch, "E2146", {"start": v(-4.8, 1.62) * mm, "end": v(-4.79, 1.63) * mm});
            skLineSegment(sketch, "E2147", {"start": v(-4.79, 1.63) * mm, "end": v(-4.78, 1.64) * mm});
            skLineSegment(sketch, "E2148", {"start": v(-4.78, 1.64) * mm, "end": v(-4.78, 1.64) * mm});
            skLineSegment(sketch, "E2149", {"start": v(-4.78, 1.64) * mm, "end": v(-4.82, 1.64) * mm});
            skLineSegment(sketch, "E2150", {"start": v(-4.82, 1.64) * mm, "end": v(-4.9, 1.63) * mm});
            skLineSegment(sketch, "E2151", {"start": v(-4.9, 1.63) * mm, "end": v(-5.01, 1.62) * mm});
            skLineSegment(sketch, "E2152", {"start": v(-5.01, 1.62) * mm, "end": v(-5.13, 1.6) * mm});
            skLineSegment(sketch, "E2153", {"start": v(-5.13, 1.6) * mm, "end": v(-5.32, 1.56) * mm});
            skLineSegment(sketch, "E2154", {"start": v(-5.32, 1.56) * mm, "end": v(-5.51, 1.51) * mm});
            skLineSegment(sketch, "E2155", {"start": v(-5.51, 1.51) * mm, "end": v(-5.68, 1.46) * mm});
            skLineSegment(sketch, "E2156", {"start": v(-5.68, 1.46) * mm, "end": v(-5.82, 1.42) * mm});
            skLineSegment(sketch, "E2157", {"start": v(-5.82, 1.42) * mm, "end": v(-5.86, 1.4) * mm});
            skLineSegment(sketch, "E2158", {"start": v(-5.86, 1.4) * mm, "end": v(-5.92, 1.37) * mm});
            skLineSegment(sketch, "E2159", {"start": v(-5.92, 1.37) * mm, "end": v(-6, 1.33) * mm});
            skLineSegment(sketch, "E2160", {"start": v(-6, 1.33) * mm, "end": v(-6.07, 1.29) * mm});
            skLineSegment(sketch, "E2161", {"start": v(-6.07, 1.29) * mm, "end": v(-6.14, 1.24) * mm});
            skLineSegment(sketch, "E2162", {"start": v(-6.14, 1.24) * mm, "end": v(-6.21, 1.2) * mm});
            skLineSegment(sketch, "E2163", {"start": v(-6.21, 1.2) * mm, "end": v(-6.27, 1.17) * mm});
            skLineSegment(sketch, "E2164", {"start": v(-6.27, 1.17) * mm, "end": v(-6.31, 1.14) * mm});
            skLineSegment(sketch, "E2165", {"start": v(-6.31, 1.14) * mm, "end": v(-6.47, 1.03) * mm});
            skLineSegment(sketch, "E2166", {"start": v(-6.47, 1.03) * mm, "end": v(-6.61, 0.9) * mm});
            skLineSegment(sketch, "E2167", {"start": v(-6.61, 0.9) * mm, "end": v(-6.73, 0.78) * mm});
            skLineSegment(sketch, "E2168", {"start": v(-6.73, 0.78) * mm, "end": v(-6.82, 0.68) * mm});
            skLineSegment(sketch, "E2169", {"start": v(-6.82, 0.68) * mm, "end": v(-6.85, 0.64) * mm});
            skLineSegment(sketch, "E2170", {"start": v(-6.85, 0.64) * mm, "end": v(-6.78, 0.63) * mm});
            skLineSegment(sketch, "E2171", {"start": v(-6.78, 0.63) * mm, "end": v(-6.74, 0.63) * mm});
            skLineSegment(sketch, "E2172", {"start": v(-6.74, 0.63) * mm, "end": v(-6.7, 0.62) * mm});
            skLineSegment(sketch, "E2173", {"start": v(-6.7, 0.62) * mm, "end": v(-6.66, 0.61) * mm});
            skLineSegment(sketch, "E2174", {"start": v(-6.66, 0.61) * mm, "end": v(-6.62, 0.6) * mm});
            skLineSegment(sketch, "E2175", {"start": v(-6.62, 0.6) * mm, "end": v(-6.58, 0.6) * mm});
            skLineSegment(sketch, "E2176", {"start": v(-6.58, 0.6) * mm, "end": v(-6.53, 0.6) * mm});
            skLineSegment(sketch, "E2177", {"start": v(-6.53, 0.6) * mm, "end": v(-6.5, 0.59) * mm});
            skLineSegment(sketch, "E2178", {"start": v(-6.5, 0.59) * mm, "end": v(-6.45, 0.58) * mm});
            skLineSegment(sketch, "E2179", {"start": v(-6.45, 0.58) * mm, "end": v(-6.34, 0.56) * mm});
            skLineSegment(sketch, "E2180", {"start": v(-6.34, 0.56) * mm, "end": v(-6.19, 0.53) * mm});
            skLineSegment(sketch, "E2181", {"start": v(-6.19, 0.53) * mm, "end": v(-6.04, 0.51) * mm});
            skLineSegment(sketch, "E2182", {"start": v(-6.04, 0.51) * mm, "end": v(-5.93, 0.5) * mm});
            skLineSegment(sketch, "E2183", {"start": v(-5.93, 0.5) * mm, "end": v(-5.88, 0.5) * mm});
            skLineSegment(sketch, "E2184", {"start": v(-5.88, 0.5) * mm, "end": v(-5.8, 0.5) * mm});
            skLineSegment(sketch, "E2185", {"start": v(-5.8, 0.5) * mm, "end": v(-5.73, 0.5) * mm});
            skLineSegment(sketch, "E2186", {"start": v(-5.73, 0.5) * mm, "end": v(-5.65, 0.49) * mm});
            skLineSegment(sketch, "E2187", {"start": v(-5.65, 0.49) * mm, "end": v(-5.58, 0.49) * mm});
            skLineSegment(sketch, "E2188", {"start": v(-5.58, 0.49) * mm, "end": v(-5.52, 0.49) * mm});
            skLineSegment(sketch, "E2189", {"start": v(-5.52, 0.49) * mm, "end": v(-5.47, 0.49) * mm});
            skLineSegment(sketch, "E2190", {"start": v(-5.47, 0.49) * mm, "end": v(-5.46, 0.5) * mm});
            skLineSegment(sketch, "E2191", {"start": v(0.63, 0.55) * mm, "end": v(0.66, 0.57) * mm});
            skLineSegment(sketch, "E2192", {"start": v(0.66, 0.57) * mm, "end": v(0.7, 0.6) * mm});
            skLineSegment(sketch, "E2193", {"start": v(0.7, 0.6) * mm, "end": v(0.75, 0.65) * mm});
            skLineSegment(sketch, "E2194", {"start": v(0.75, 0.65) * mm, "end": v(0.8, 0.7) * mm});
            skLineSegment(sketch, "E2195", {"start": v(0.8, 0.7) * mm, "end": v(0.86, 0.74) * mm});
            skLineSegment(sketch, "E2196", {"start": v(0.86, 0.74) * mm, "end": v(0.92, 0.78) * mm});
            skLineSegment(sketch, "E2197", {"start": v(0.92, 0.78) * mm, "end": v(0.97, 0.82) * mm});
            skLineSegment(sketch, "E2198", {"start": v(0.97, 0.82) * mm, "end": v(1.02, 0.86) * mm});
            skLineSegment(sketch, "E2199", {"start": v(1.02, 0.86) * mm, "end": v(1.07, 0.89) * mm});
            skLineSegment(sketch, "E2200", {"start": v(1.07, 0.89) * mm, "end": v(1.13, 0.92) * mm});
            skLineSegment(sketch, "E2201", {"start": v(1.13, 0.92) * mm, "end": v(1.2, 0.96) * mm});
            skLineSegment(sketch, "E2202", {"start": v(1.2, 0.96) * mm, "end": v(1.25, 0.99) * mm});
            skLineSegment(sketch, "E2203", {"start": v(1.25, 0.99) * mm, "end": v(1.3, 1.02) * mm});
            skLineSegment(sketch, "E2204", {"start": v(1.3, 1.02) * mm, "end": v(1.36, 1.05) * mm});
            skLineSegment(sketch, "E2205", {"start": v(1.36, 1.05) * mm, "end": v(1.4, 1.08) * mm});
            skLineSegment(sketch, "E2206", {"start": v(1.4, 1.08) * mm, "end": v(1.44, 1.1) * mm});
            skLineSegment(sketch, "E2207", {"start": v(1.44, 1.1) * mm, "end": v(1.5, 1.15) * mm});
            skLineSegment(sketch, "E2208", {"start": v(1.5, 1.15) * mm, "end": v(1.56, 1.22) * mm});
            skLineSegment(sketch, "E2209", {"start": v(1.56, 1.22) * mm, "end": v(1.63, 1.3) * mm});
            skLineSegment(sketch, "E2210", {"start": v(1.63, 1.3) * mm, "end": v(1.68, 1.37) * mm});
            skLineSegment(sketch, "E2211", {"start": v(1.68, 1.37) * mm, "end": v(1.7, 1.42) * mm});
            skLineSegment(sketch, "E2212", {"start": v(1.7, 1.42) * mm, "end": v(1.74, 1.46) * mm});
            skLineSegment(sketch, "E2213", {"start": v(1.74, 1.46) * mm, "end": v(1.76, 1.49) * mm});
            skLineSegment(sketch, "E2214", {"start": v(1.76, 1.49) * mm, "end": v(1.78, 1.53) * mm});
            skLineSegment(sketch, "E2215", {"start": v(1.78, 1.53) * mm, "end": v(1.8, 1.57) * mm});
            skLineSegment(sketch, "E2216", {"start": v(1.8, 1.57) * mm, "end": v(1.84, 1.61) * mm});
            skLineSegment(sketch, "E2217", {"start": v(1.84, 1.61) * mm, "end": v(1.92, 1.73) * mm});
            skLineSegment(sketch, "E2218", {"start": v(1.92, 1.73) * mm, "end": v(2.02, 1.86) * mm});
            skLineSegment(sketch, "E2219", {"start": v(2.02, 1.86) * mm, "end": v(2.13, 1.97) * mm});
            skLineSegment(sketch, "E2220", {"start": v(2.13, 1.97) * mm, "end": v(2.26, 2.08) * mm});
            skLineSegment(sketch, "E2221", {"start": v(2.26, 2.08) * mm, "end": v(2.4, 2.2) * mm});
            skLineSegment(sketch, "E2222", {"start": v(2.4, 2.2) * mm, "end": v(2.54, 2.29) * mm});
            skLineSegment(sketch, "E2223", {"start": v(2.54, 2.29) * mm, "end": v(2.66, 2.36) * mm});
            skLineSegment(sketch, "E2224", {"start": v(2.66, 2.36) * mm, "end": v(2.81, 2.43) * mm});
            skLineSegment(sketch, "E2225", {"start": v(2.81, 2.43) * mm, "end": v(3.03, 2.53) * mm});
            skLineSegment(sketch, "E2226", {"start": v(3.03, 2.53) * mm, "end": v(2.95, 2.53) * mm});
            skLineSegment(sketch, "E2227", {"start": v(2.95, 2.53) * mm, "end": v(2.91, 2.52) * mm});
            skLineSegment(sketch, "E2228", {"start": v(2.91, 2.52) * mm, "end": v(2.87, 2.51) * mm});
            skLineSegment(sketch, "E2229", {"start": v(2.87, 2.51) * mm, "end": v(2.83, 2.5) * mm});
            skLineSegment(sketch, "E2230", {"start": v(2.83, 2.5) * mm, "end": v(2.79, 2.5) * mm});
            skLineSegment(sketch, "E2231", {"start": v(2.79, 2.5) * mm, "end": v(2.75, 2.49) * mm});
            skLineSegment(sketch, "E2232", {"start": v(2.75, 2.49) * mm, "end": v(2.7, 2.48) * mm});
            skLineSegment(sketch, "E2233", {"start": v(2.7, 2.48) * mm, "end": v(2.64, 2.46) * mm});
            skLineSegment(sketch, "E2234", {"start": v(2.64, 2.46) * mm, "end": v(2.6, 2.45) * mm});
            skLineSegment(sketch, "E2235", {"start": v(2.6, 2.45) * mm, "end": v(2.35, 2.38) * mm});
            skLineSegment(sketch, "E2236", {"start": v(2.35, 2.38) * mm, "end": v(2.1, 2.28) * mm});
            skLineSegment(sketch, "E2237", {"start": v(2.1, 2.28) * mm, "end": v(1.86, 2.13) * mm});
            skLineSegment(sketch, "E2238", {"start": v(1.86, 2.13) * mm, "end": v(1.6, 1.94) * mm});
            skLineSegment(sketch, "E2239", {"start": v(1.6, 1.94) * mm, "end": v(1.45, 1.83) * mm});
            skLineSegment(sketch, "E2240", {"start": v(1.45, 1.83) * mm, "end": v(1.33, 1.72) * mm});
            skLineSegment(sketch, "E2241", {"start": v(1.33, 1.72) * mm, "end": v(1.22, 1.63) * mm});
            skLineSegment(sketch, "E2242", {"start": v(1.22, 1.63) * mm, "end": v(1.13, 1.55) * mm});
            skLineSegment(sketch, "E2243", {"start": v(1.13, 1.55) * mm, "end": v(1.04, 1.48) * mm});
            skLineSegment(sketch, "E2244", {"start": v(1.04, 1.48) * mm, "end": v(0.98, 1.42) * mm});
            skLineSegment(sketch, "E2245", {"start": v(0.98, 1.42) * mm, "end": v(0.92, 1.36) * mm});
            skLineSegment(sketch, "E2246", {"start": v(0.92, 1.36) * mm, "end": v(0.87, 1.3) * mm});
            skLineSegment(sketch, "E2247", {"start": v(0.87, 1.3) * mm, "end": v(0.81, 1.24) * mm});
            skLineSegment(sketch, "E2248", {"start": v(0.81, 1.24) * mm, "end": v(0.76, 1.18) * mm});
            skLineSegment(sketch, "E2249", {"start": v(0.76, 1.18) * mm, "end": v(0.7, 1.1) * mm});
            skLineSegment(sketch, "E2250", {"start": v(0.7, 1.1) * mm, "end": v(0.66, 1.05) * mm});
            skLineSegment(sketch, "E2251", {"start": v(0.66, 1.05) * mm, "end": v(0.61, 1) * mm});
            skLineSegment(sketch, "E2252", {"start": v(0.61, 1) * mm, "end": v(0.58, 0.95) * mm});
            skLineSegment(sketch, "E2253", {"start": v(0.58, 0.95) * mm, "end": v(0.56, 0.91) * mm});
            skLineSegment(sketch, "E2254", {"start": v(0.56, 0.91) * mm, "end": v(0.55, 0.9) * mm});
            skLineSegment(sketch, "E2255", {"start": v(0.55, 0.9) * mm, "end": v(0.56, 0.87) * mm});
            skLineSegment(sketch, "E2256", {"start": v(0.56, 0.87) * mm, "end": v(0.56, 0.83) * mm});
            skLineSegment(sketch, "E2257", {"start": v(0.56, 0.83) * mm, "end": v(0.56, 0.77) * mm});
            skLineSegment(sketch, "E2258", {"start": v(0.56, 0.77) * mm, "end": v(0.57, 0.7) * mm});
            skLineSegment(sketch, "E2259", {"start": v(0.57, 0.7) * mm, "end": v(0.58, 0.63) * mm});
            skLineSegment(sketch, "E2260", {"start": v(0.58, 0.63) * mm, "end": v(0.58, 0.58) * mm});
            skLineSegment(sketch, "E2261", {"start": v(0.58, 0.58) * mm, "end": v(0.59, 0.53) * mm});
            skLineSegment(sketch, "E2262", {"start": v(0.59, 0.53) * mm, "end": v(0.59, 0.52) * mm});
            skLineSegment(sketch, "E2263", {"start": v(0.59, 0.52) * mm, "end": v(0.6, 0.5) * mm});
            skLineSegment(sketch, "E2264", {"start": v(0.6, 0.5) * mm, "end": v(0.6, 0.51) * mm});
            skLineSegment(sketch, "E2265", {"start": v(0.6, 0.51) * mm, "end": v(0.61, 0.52) * mm});
            skLineSegment(sketch, "E2266", {"start": v(0.61, 0.52) * mm, "end": v(0.63, 0.55) * mm});
            skLineSegment(sketch, "E2267", {"start": v(-4.85, 0.6) * mm, "end": v(-4.75, 0.63) * mm});
            skLineSegment(sketch, "E2268", {"start": v(-4.75, 0.63) * mm, "end": v(-4.64, 0.67) * mm});
            skLineSegment(sketch, "E2269", {"start": v(-4.64, 0.67) * mm, "end": v(-4.54, 0.71) * mm});
            skLineSegment(sketch, "E2270", {"start": v(-4.54, 0.71) * mm, "end": v(-4.46, 0.75) * mm});
            skLineSegment(sketch, "E2271", {"start": v(-4.46, 0.75) * mm, "end": v(-4.41, 0.77) * mm});
            skLineSegment(sketch, "E2272", {"start": v(-4.41, 0.77) * mm, "end": v(-4.33, 0.8) * mm});
            skLineSegment(sketch, "E2273", {"start": v(-4.33, 0.8) * mm, "end": v(-4.2, 0.83) * mm});
            skLineSegment(sketch, "E2274", {"start": v(-4.2, 0.83) * mm, "end": v(-4.04, 0.87) * mm});
            skLineSegment(sketch, "E2275", {"start": v(-4.04, 0.87) * mm, "end": v(-4, 0.88) * mm});
            skLineSegment(sketch, "E2276", {"start": v(-4, 0.88) * mm, "end": v(-3.94, 0.89) * mm});
            skLineSegment(sketch, "E2277", {"start": v(-3.94, 0.89) * mm, "end": v(-3.87, 0.9) * mm});
            skLineSegment(sketch, "E2278", {"start": v(-3.87, 0.9) * mm, "end": v(-3.79, 0.9) * mm});
            skLineSegment(sketch, "E2279", {"start": v(-3.79, 0.9) * mm, "end": v(-3.67, 0.92) * mm});
            skLineSegment(sketch, "E2280", {"start": v(-3.67, 0.92) * mm, "end": v(-3.57, 0.93) * mm});
            skLineSegment(sketch, "E2281", {"start": v(-3.57, 0.93) * mm, "end": v(-3.44, 0.93) * mm});
            skLineSegment(sketch, "E2282", {"start": v(-3.44, 0.93) * mm, "end": v(-3.24, 0.93) * mm});
            skLineSegment(sketch, "E2283", {"start": v(-3.24, 0.93) * mm, "end": v(-2.97, 0.92) * mm});
            skLineSegment(sketch, "E2284", {"start": v(-2.97, 0.92) * mm, "end": v(-2.75, 0.9) * mm});
            skLineSegment(sketch, "E2285", {"start": v(-2.75, 0.9) * mm, "end": v(-2.57, 0.89) * mm});
            skLineSegment(sketch, "E2286", {"start": v(-2.57, 0.89) * mm, "end": v(-2.43, 0.86) * mm});
            skLineSegment(sketch, "E2287", {"start": v(-2.43, 0.86) * mm, "end": v(-2.35, 0.84) * mm});
            skLineSegment(sketch, "E2288", {"start": v(-2.35, 0.84) * mm, "end": v(-2.29, 0.82) * mm});
            skLineSegment(sketch, "E2289", {"start": v(-2.29, 0.82) * mm, "end": v(-2.22, 0.8) * mm});
            skLineSegment(sketch, "E2290", {"start": v(-2.22, 0.8) * mm, "end": v(-2.12, 0.8) * mm});
            skLineSegment(sketch, "E2291", {"start": v(-2.12, 0.8) * mm, "end": v(-2.08, 0.79) * mm});
            skLineSegment(sketch, "E2292", {"start": v(-2.08, 0.79) * mm, "end": v(-2.04, 0.78) * mm});
            skLineSegment(sketch, "E2293", {"start": v(-2.04, 0.78) * mm, "end": v(-2.01, 0.77) * mm});
            skLineSegment(sketch, "E2294", {"start": v(-2.01, 0.77) * mm, "end": v(-2, 0.77) * mm});
            skLineSegment(sketch, "E2295", {"start": v(-2, 0.77) * mm, "end": v(-1.99, 0.77) * mm});
            skLineSegment(sketch, "E2296", {"start": v(-1.99, 0.77) * mm, "end": v(-1.99, 0.77) * mm});
            skLineSegment(sketch, "E2297", {"start": v(-1.99, 0.77) * mm, "end": v(-2, 0.79) * mm});
            skLineSegment(sketch, "E2298", {"start": v(-2, 0.79) * mm, "end": v(-2.03, 0.8) * mm});
            skLineSegment(sketch, "E2299", {"start": v(-2.03, 0.8) * mm, "end": v(-2.06, 0.84) * mm});
            skLineSegment(sketch, "E2300", {"start": v(-2.06, 0.84) * mm, "end": v(-2.11, 0.88) * mm});
            skLineSegment(sketch, "E2301", {"start": v(-2.11, 0.88) * mm, "end": v(-2.18, 0.93) * mm});
            skLineSegment(sketch, "E2302", {"start": v(-2.18, 0.93) * mm, "end": v(-2.26, 1) * mm});
            skLineSegment(sketch, "E2303", {"start": v(-2.26, 1) * mm, "end": v(-2.45, 1.13) * mm});
            skLineSegment(sketch, "E2304", {"start": v(-2.45, 1.13) * mm, "end": v(-2.61, 1.22) * mm});
            skLineSegment(sketch, "E2305", {"start": v(-2.61, 1.22) * mm, "end": v(-2.78, 1.3) * mm});
            skLineSegment(sketch, "E2306", {"start": v(-2.78, 1.3) * mm, "end": v(-2.99, 1.37) * mm});
            skLineSegment(sketch, "E2307", {"start": v(-2.99, 1.37) * mm, "end": v(-3.22, 1.44) * mm});
            skLineSegment(sketch, "E2308", {"start": v(-3.22, 1.44) * mm, "end": v(-3.44, 1.5) * mm});
            skLineSegment(sketch, "E2309", {"start": v(-3.44, 1.5) * mm, "end": v(-3.66, 1.53) * mm});
            skLineSegment(sketch, "E2310", {"start": v(-3.66, 1.53) * mm, "end": v(-3.87, 1.55) * mm});
            skLineSegment(sketch, "E2311", {"start": v(-3.87, 1.55) * mm, "end": v(-4, 1.56) * mm});
            skLineSegment(sketch, "E2312", {"start": v(-4, 1.56) * mm, "end": v(-4.12, 1.56) * mm});
            skLineSegment(sketch, "E2313", {"start": v(-4.12, 1.56) * mm, "end": v(-4.23, 1.55) * mm});
            skLineSegment(sketch, "E2314", {"start": v(-4.23, 1.55) * mm, "end": v(-4.35, 1.52) * mm});
            skLineSegment(sketch, "E2315", {"start": v(-4.35, 1.52) * mm, "end": v(-4.6, 1.46) * mm});
            skLineSegment(sketch, "E2316", {"start": v(-4.6, 1.46) * mm, "end": v(-4.8, 1.37) * mm});
            skLineSegment(sketch, "E2317", {"start": v(-4.8, 1.37) * mm, "end": v(-4.95, 1.25) * mm});
            skLineSegment(sketch, "E2318", {"start": v(-4.95, 1.25) * mm, "end": v(-5.05, 1.11) * mm});
            skLineSegment(sketch, "E2319", {"start": v(-5.05, 1.11) * mm, "end": v(-5.1, 1) * mm});
            skLineSegment(sketch, "E2320", {"start": v(-5.1, 1) * mm, "end": v(-5.12, 0.87) * mm});
            skLineSegment(sketch, "E2321", {"start": v(-5.12, 0.87) * mm, "end": v(-5.13, 0.75) * mm});
            skLineSegment(sketch, "E2322", {"start": v(-5.13, 0.75) * mm, "end": v(-5.13, 0.6) * mm});
            skLineSegment(sketch, "E2323", {"start": v(-5.13, 0.6) * mm, "end": v(-5.12, 0.53) * mm});
            skLineSegment(sketch, "E2324", {"start": v(-5.12, 0.53) * mm, "end": v(-5.04, 0.55) * mm});
            skLineSegment(sketch, "E2325", {"start": v(-5.04, 0.55) * mm, "end": v(-5, 0.56) * mm});
            skLineSegment(sketch, "E2326", {"start": v(-5, 0.56) * mm, "end": v(-4.95, 0.57) * mm});
            skLineSegment(sketch, "E2327", {"start": v(-4.95, 0.57) * mm, "end": v(-4.9, 0.58) * mm});
            skLineSegment(sketch, "E2328", {"start": v(-4.9, 0.58) * mm, "end": v(-4.85, 0.6) * mm});
            skLineSegment(sketch, "E2329", {"start": v(-0.29, 0.68) * mm, "end": v(-0.24, 0.7) * mm});
            skLineSegment(sketch, "E2330", {"start": v(-0.24, 0.7) * mm, "end": v(-0.2, 0.73) * mm});
            skLineSegment(sketch, "E2331", {"start": v(-0.2, 0.73) * mm, "end": v(-0.16, 0.76) * mm});
            skLineSegment(sketch, "E2332", {"start": v(-0.16, 0.76) * mm, "end": v(-0.13, 0.8) * mm});
            skLineSegment(sketch, "E2333", {"start": v(-0.13, 0.8) * mm, "end": v(-0.1, 0.84) * mm});
            skLineSegment(sketch, "E2334", {"start": v(-0.1, 0.84) * mm, "end": v(-0.06, 0.85) * mm});
            skLineSegment(sketch, "E2335", {"start": v(-0.06, 0.85) * mm, "end": v(-0.02, 0.84) * mm});
            skLineSegment(sketch, "E2336", {"start": v(-0.02, 0.84) * mm, "end": v(0.03, 0.8) * mm});
            skLineSegment(sketch, "E2337", {"start": v(0.03, 0.8) * mm, "end": v(0.07, 0.8) * mm});
            skLineSegment(sketch, "E2338", {"start": v(0.07, 0.8) * mm, "end": v(0.12, 0.78) * mm});
            skLineSegment(sketch, "E2339", {"start": v(0.12, 0.78) * mm, "end": v(0.17, 0.78) * mm});
            skLineSegment(sketch, "E2340", {"start": v(0.17, 0.78) * mm, "end": v(0.2, 0.78) * mm});
            skLineSegment(sketch, "E2341", {"start": v(0.2, 0.78) * mm, "end": v(0.21, 0.82) * mm});
            skLineSegment(sketch, "E2342", {"start": v(0.21, 0.82) * mm, "end": v(0.19, 0.92) * mm});
            skLineSegment(sketch, "E2343", {"start": v(0.19, 0.92) * mm, "end": v(0.14, 1.06) * mm});
            skLineSegment(sketch, "E2344", {"start": v(0.14, 1.06) * mm, "end": v(0.07, 1.26) * mm});
            skLineSegment(sketch, "E2345", {"start": v(0.07, 1.26) * mm, "end": v(0.04, 1.32) * mm});
            skLineSegment(sketch, "E2346", {"start": v(0.04, 1.32) * mm, "end": v(0.02, 1.36) * mm});
            skLineSegment(sketch, "E2347", {"start": v(0.02, 1.36) * mm, "end": v(0, 1.39) * mm});
            skLineSegment(sketch, "E2348", {"start": v(0, 1.39) * mm, "end": v(0, 1.4) * mm});
            skLineSegment(sketch, "E2349", {"start": v(0, 1.4) * mm, "end": v(-0.03, 1.4) * mm});
            skLineSegment(sketch, "E2350", {"start": v(-0.03, 1.4) * mm, "end": v(-0.08, 1.38) * mm});
            skLineSegment(sketch, "E2351", {"start": v(-0.08, 1.38) * mm, "end": v(-0.21, 1.36) * mm});
            skLineSegment(sketch, "E2352", {"start": v(-0.21, 1.36) * mm, "end": v(-0.36, 1.36) * mm});
            skLineSegment(sketch, "E2353", {"start": v(-0.36, 1.36) * mm, "end": v(-0.52, 1.38) * mm});
            skLineSegment(sketch, "E2354", {"start": v(-0.52, 1.38) * mm, "end": v(-0.68, 1.41) * mm});
            skLineSegment(sketch, "E2355", {"start": v(-0.68, 1.41) * mm, "end": v(-0.71, 1.43) * mm});
            skLineSegment(sketch, "E2356", {"start": v(-0.71, 1.43) * mm, "end": v(-0.74, 1.43) * mm});
            skLineSegment(sketch, "E2357", {"start": v(-0.74, 1.43) * mm, "end": v(-0.77, 1.44) * mm});
            skLineSegment(sketch, "E2358", {"start": v(-0.77, 1.44) * mm, "end": v(-0.77, 1.44) * mm});
            skLineSegment(sketch, "E2359", {"start": v(-0.77, 1.44) * mm, "end": v(-0.79, 1.4) * mm});
            skLineSegment(sketch, "E2360", {"start": v(-0.79, 1.4) * mm, "end": v(-0.81, 1.35) * mm});
            skLineSegment(sketch, "E2361", {"start": v(-0.81, 1.35) * mm, "end": v(-0.84, 1.27) * mm});
            skLineSegment(sketch, "E2362", {"start": v(-0.84, 1.27) * mm, "end": v(-0.86, 1.17) * mm});
            skLineSegment(sketch, "E2363", {"start": v(-0.86, 1.17) * mm, "end": v(-0.89, 1.07) * mm});
            skLineSegment(sketch, "E2364", {"start": v(-0.89, 1.07) * mm, "end": v(-0.9, 0.98) * mm});
            skLineSegment(sketch, "E2365", {"start": v(-0.9, 0.98) * mm, "end": v(-0.92, 0.9) * mm});
            skLineSegment(sketch, "E2366", {"start": v(-0.92, 0.9) * mm, "end": v(-0.93, 0.85) * mm});
            skLineSegment(sketch, "E2367", {"start": v(-0.93, 0.85) * mm, "end": v(-0.93, 0.78) * mm});
            skLineSegment(sketch, "E2368", {"start": v(-0.93, 0.78) * mm, "end": v(-0.82, 0.74) * mm});
            skLineSegment(sketch, "E2369", {"start": v(-0.82, 0.74) * mm, "end": v(-0.7, 0.7) * mm});
            skLineSegment(sketch, "E2370", {"start": v(-0.7, 0.7) * mm, "end": v(-0.6, 0.67) * mm});
            skLineSegment(sketch, "E2371", {"start": v(-0.6, 0.67) * mm, "end": v(-0.5, 0.65) * mm});
            skLineSegment(sketch, "E2372", {"start": v(-0.5, 0.65) * mm, "end": v(-0.42, 0.65) * mm});
            skLineSegment(sketch, "E2373", {"start": v(-0.42, 0.65) * mm, "end": v(-0.35, 0.66) * mm});
            skLineSegment(sketch, "E2374", {"start": v(-0.35, 0.66) * mm, "end": v(-0.29, 0.68) * mm});
            skLineSegment(sketch, "E2375", {"start": v(-7, 0.96) * mm, "end": v(-6.85, 1.1) * mm});
            skLineSegment(sketch, "E2376", {"start": v(-6.85, 1.1) * mm, "end": v(-6.72, 1.2) * mm});
            skLineSegment(sketch, "E2377", {"start": v(-6.72, 1.2) * mm, "end": v(-6.62, 1.29) * mm});
            skLineSegment(sketch, "E2378", {"start": v(-6.62, 1.29) * mm, "end": v(-6.52, 1.35) * mm});
            skLineSegment(sketch, "E2379", {"start": v(-6.52, 1.35) * mm, "end": v(-6.44, 1.39) * mm});
            skLineSegment(sketch, "E2380", {"start": v(-6.44, 1.39) * mm, "end": v(-6.4, 1.42) * mm});
            skLineSegment(sketch, "E2381", {"start": v(-6.4, 1.42) * mm, "end": v(-6.37, 1.44) * mm});
            skLineSegment(sketch, "E2382", {"start": v(-6.37, 1.44) * mm, "end": v(-6.37, 1.45) * mm});
            skLineSegment(sketch, "E2383", {"start": v(-6.37, 1.45) * mm, "end": v(-6.39, 1.45) * mm});
            skLineSegment(sketch, "E2384", {"start": v(-6.39, 1.45) * mm, "end": v(-6.44, 1.45) * mm});
            skLineSegment(sketch, "E2385", {"start": v(-6.44, 1.45) * mm, "end": v(-6.5, 1.44) * mm});
            skLineSegment(sketch, "E2386", {"start": v(-6.5, 1.44) * mm, "end": v(-6.6, 1.44) * mm});
            skLineSegment(sketch, "E2387", {"start": v(-6.6, 1.44) * mm, "end": v(-6.69, 1.43) * mm});
            skLineSegment(sketch, "E2388", {"start": v(-6.69, 1.43) * mm, "end": v(-6.79, 1.43) * mm});
            skLineSegment(sketch, "E2389", {"start": v(-6.79, 1.43) * mm, "end": v(-6.89, 1.42) * mm});
            skLineSegment(sketch, "E2390", {"start": v(-6.89, 1.42) * mm, "end": v(-6.97, 1.4) * mm});
            skLineSegment(sketch, "E2391", {"start": v(-6.97, 1.4) * mm, "end": v(-7.13, 1.4) * mm});
            skLineSegment(sketch, "E2392", {"start": v(-7.13, 1.4) * mm, "end": v(-7.29, 1.37) * mm});
            skLineSegment(sketch, "E2393", {"start": v(-7.29, 1.37) * mm, "end": v(-7.45, 1.34) * mm});
            skLineSegment(sketch, "E2394", {"start": v(-7.45, 1.34) * mm, "end": v(-7.64, 1.3) * mm});
            skLineSegment(sketch, "E2395", {"start": v(-7.64, 1.3) * mm, "end": v(-7.7, 1.28) * mm});
            skLineSegment(sketch, "E2396", {"start": v(-7.7, 1.28) * mm, "end": v(-7.76, 1.27) * mm});
            skLineSegment(sketch, "E2397", {"start": v(-7.76, 1.27) * mm, "end": v(-7.8, 1.25) * mm});
            skLineSegment(sketch, "E2398", {"start": v(-7.8, 1.25) * mm, "end": v(-7.83, 1.25) * mm});
            skLineSegment(sketch, "E2399", {"start": v(-7.83, 1.25) * mm, "end": v(-7.85, 1.24) * mm});
            skLineSegment(sketch, "E2400", {"start": v(-7.85, 1.24) * mm, "end": v(-7.86, 1.23) * mm});
            skLineSegment(sketch, "E2401", {"start": v(-7.86, 1.23) * mm, "end": v(-7.86, 1.23) * mm});
            skLineSegment(sketch, "E2402", {"start": v(-7.86, 1.23) * mm, "end": v(-7.86, 1.22) * mm});
            skLineSegment(sketch, "E2403", {"start": v(-7.86, 1.22) * mm, "end": v(-7.85, 1.21) * mm});
            skLineSegment(sketch, "E2404", {"start": v(-7.85, 1.21) * mm, "end": v(-7.81, 1.2) * mm});
            skLineSegment(sketch, "E2405", {"start": v(-7.81, 1.2) * mm, "end": v(-7.77, 1.18) * mm});
            skLineSegment(sketch, "E2406", {"start": v(-7.77, 1.18) * mm, "end": v(-7.71, 1.17) * mm});
            skLineSegment(sketch, "E2407", {"start": v(-7.71, 1.17) * mm, "end": v(-7.62, 1.14) * mm});
            skLineSegment(sketch, "E2408", {"start": v(-7.62, 1.14) * mm, "end": v(-7.56, 1.1) * mm});
            skLineSegment(sketch, "E2409", {"start": v(-7.56, 1.1) * mm, "end": v(-7.51, 1.06) * mm});
            skLineSegment(sketch, "E2410", {"start": v(-7.51, 1.06) * mm, "end": v(-7.47, 1) * mm});
            skLineSegment(sketch, "E2411", {"start": v(-7.47, 1) * mm, "end": v(-7.45, 0.98) * mm});
            skLineSegment(sketch, "E2412", {"start": v(-7.45, 0.98) * mm, "end": v(-7.43, 0.95) * mm});
            skLineSegment(sketch, "E2413", {"start": v(-7.43, 0.95) * mm, "end": v(-7.4, 0.93) * mm});
            skLineSegment(sketch, "E2414", {"start": v(-7.4, 0.93) * mm, "end": v(-7.38, 0.9) * mm});
            skLineSegment(sketch, "E2415", {"start": v(-7.38, 0.9) * mm, "end": v(-7.36, 0.9) * mm});
            skLineSegment(sketch, "E2416", {"start": v(-7.36, 0.9) * mm, "end": v(-7.33, 0.87) * mm});
            skLineSegment(sketch, "E2417", {"start": v(-7.33, 0.87) * mm, "end": v(-7.3, 0.86) * mm});
            skLineSegment(sketch, "E2418", {"start": v(-7.3, 0.86) * mm, "end": v(-7.27, 0.84) * mm});
            skLineSegment(sketch, "E2419", {"start": v(-7.27, 0.84) * mm, "end": v(-7.24, 0.82) * mm});
            skLineSegment(sketch, "E2420", {"start": v(-7.24, 0.82) * mm, "end": v(-7.22, 0.81) * mm});
            skLineSegment(sketch, "E2421", {"start": v(-7.22, 0.81) * mm, "end": v(-7.2, 0.8) * mm});
            skLineSegment(sketch, "E2422", {"start": v(-7.2, 0.8) * mm, "end": v(-7.19, 0.8) * mm});
            skLineSegment(sketch, "E2423", {"start": v(-7.19, 0.8) * mm, "end": v(-7.18, 0.8) * mm});
            skLineSegment(sketch, "E2424", {"start": v(-7.18, 0.8) * mm, "end": v(-7.17, 0.81) * mm});
            skLineSegment(sketch, "E2425", {"start": v(-7.17, 0.81) * mm, "end": v(-7.15, 0.83) * mm});
            skLineSegment(sketch, "E2426", {"start": v(-7.15, 0.83) * mm, "end": v(-7.13, 0.85) * mm});
            skLineSegment(sketch, "E2427", {"start": v(-7.13, 0.85) * mm, "end": v(-7.1, 0.87) * mm});
            skLineSegment(sketch, "E2428", {"start": v(-7.1, 0.87) * mm, "end": v(-7.07, 0.9) * mm});
            skLineSegment(sketch, "E2429", {"start": v(-7.07, 0.9) * mm, "end": v(-7.04, 0.93) * mm});
            skLineSegment(sketch, "E2430", {"start": v(-7.04, 0.93) * mm, "end": v(-7, 0.96) * mm});
            skLineSegment(sketch, "E2431", {"start": v(-1.2, 0.95) * mm, "end": v(-1.2, 0.96) * mm});
            skLineSegment(sketch, "E2432", {"start": v(-1.2, 0.96) * mm, "end": v(-1.21, 0.98) * mm});
            skLineSegment(sketch, "E2433", {"start": v(-1.21, 0.98) * mm, "end": v(-1.23, 1) * mm});
            skLineSegment(sketch, "E2434", {"start": v(-1.23, 1) * mm, "end": v(-1.25, 1.03) * mm});
            skLineSegment(sketch, "E2435", {"start": v(-1.25, 1.03) * mm, "end": v(-1.27, 1.07) * mm});
            skLineSegment(sketch, "E2436", {"start": v(-1.27, 1.07) * mm, "end": v(-1.3, 1.1) * mm});
            skLineSegment(sketch, "E2437", {"start": v(-1.3, 1.1) * mm, "end": v(-1.32, 1.13) * mm});
            skLineSegment(sketch, "E2438", {"start": v(-1.32, 1.13) * mm, "end": v(-1.34, 1.17) * mm});
            skLineSegment(sketch, "E2439", {"start": v(-1.34, 1.17) * mm, "end": v(-1.38, 1.22) * mm});
            skLineSegment(sketch, "E2440", {"start": v(-1.38, 1.22) * mm, "end": v(-1.44, 1.28) * mm});
            skLineSegment(sketch, "E2441", {"start": v(-1.44, 1.28) * mm, "end": v(-1.52, 1.36) * mm});
            skLineSegment(sketch, "E2442", {"start": v(-1.52, 1.36) * mm, "end": v(-1.6, 1.44) * mm});
            skLineSegment(sketch, "E2443", {"start": v(-1.6, 1.44) * mm, "end": v(-1.7, 1.53) * mm});
            skLineSegment(sketch, "E2444", {"start": v(-1.7, 1.53) * mm, "end": v(-1.78, 1.6) * mm});
            skLineSegment(sketch, "E2445", {"start": v(-1.78, 1.6) * mm, "end": v(-1.86, 1.68) * mm});
            skLineSegment(sketch, "E2446", {"start": v(-1.86, 1.68) * mm, "end": v(-1.92, 1.74) * mm});
            skLineSegment(sketch, "E2447", {"start": v(-1.92, 1.74) * mm, "end": v(-1.96, 1.77) * mm});
            skLineSegment(sketch, "E2448", {"start": v(-1.96, 1.77) * mm, "end": v(-2, 1.8) * mm});
            skLineSegment(sketch, "E2449", {"start": v(-2, 1.8) * mm, "end": v(-2.03, 1.82) * mm});
            skLineSegment(sketch, "E2450", {"start": v(-2.03, 1.82) * mm, "end": v(-2.06, 1.84) * mm});
            skLineSegment(sketch, "E2451", {"start": v(-2.06, 1.84) * mm, "end": v(-2.1, 1.86) * mm});
            skLineSegment(sketch, "E2452", {"start": v(-2.1, 1.86) * mm, "end": v(-2.15, 1.9) * mm});
            skLineSegment(sketch, "E2453", {"start": v(-2.15, 1.9) * mm, "end": v(-2.22, 1.94) * mm});
            skLineSegment(sketch, "E2454", {"start": v(-2.22, 1.94) * mm, "end": v(-2.3, 2) * mm});
            skLineSegment(sketch, "E2455", {"start": v(-2.3, 2) * mm, "end": v(-2.37, 2.04) * mm});
            skLineSegment(sketch, "E2456", {"start": v(-2.37, 2.04) * mm, "end": v(-2.44, 2.09) * mm});
            skLineSegment(sketch, "E2457", {"start": v(-2.44, 2.09) * mm, "end": v(-2.5, 2.12) * mm});
            skLineSegment(sketch, "E2458", {"start": v(-2.5, 2.12) * mm, "end": v(-2.53, 2.14) * mm});
            skLineSegment(sketch, "E2459", {"start": v(-2.53, 2.14) * mm, "end": v(-2.56, 2.16) * mm});
            skLineSegment(sketch, "E2460", {"start": v(-2.56, 2.16) * mm, "end": v(-2.6, 2.17) * mm});
            skLineSegment(sketch, "E2461", {"start": v(-2.6, 2.17) * mm, "end": v(-2.65, 2.2) * mm});
            skLineSegment(sketch, "E2462", {"start": v(-2.65, 2.2) * mm, "end": v(-2.7, 2.21) * mm});
            skLineSegment(sketch, "E2463", {"start": v(-2.7, 2.21) * mm, "end": v(-2.74, 2.23) * mm});
            skLineSegment(sketch, "E2464", {"start": v(-2.74, 2.23) * mm, "end": v(-2.78, 2.25) * mm});
            skLineSegment(sketch, "E2465", {"start": v(-2.78, 2.25) * mm, "end": v(-2.8, 2.26) * mm});
            skLineSegment(sketch, "E2466", {"start": v(-2.8, 2.26) * mm, "end": v(-2.82, 2.26) * mm});
            skLineSegment(sketch, "E2467", {"start": v(-2.82, 2.26) * mm, "end": v(-2.84, 2.25) * mm});
            skLineSegment(sketch, "E2468", {"start": v(-2.84, 2.25) * mm, "end": v(-2.85, 2.22) * mm});
            skLineSegment(sketch, "E2469", {"start": v(-2.85, 2.22) * mm, "end": v(-2.86, 2.19) * mm});
            skLineSegment(sketch, "E2470", {"start": v(-2.86, 2.19) * mm, "end": v(-2.87, 2.15) * mm});
            skLineSegment(sketch, "E2471", {"start": v(-2.87, 2.15) * mm, "end": v(-2.86, 2.1) * mm});
            skLineSegment(sketch, "E2472", {"start": v(-2.86, 2.1) * mm, "end": v(-2.84, 2) * mm});
            skLineSegment(sketch, "E2473", {"start": v(-2.84, 2) * mm, "end": v(-2.82, 1.93) * mm});
            skLineSegment(sketch, "E2474", {"start": v(-2.82, 1.93) * mm, "end": v(-2.8, 1.87) * mm});
            skLineSegment(sketch, "E2475", {"start": v(-2.8, 1.87) * mm, "end": v(-2.76, 1.8) * mm});
            skLineSegment(sketch, "E2476", {"start": v(-2.76, 1.8) * mm, "end": v(-2.7, 1.73) * mm});
            skLineSegment(sketch, "E2477", {"start": v(-2.7, 1.73) * mm, "end": v(-2.63, 1.66) * mm});
            skLineSegment(sketch, "E2478", {"start": v(-2.63, 1.66) * mm, "end": v(-2.56, 1.6) * mm});
            skLineSegment(sketch, "E2479", {"start": v(-2.56, 1.6) * mm, "end": v(-2.41, 1.49) * mm});
            skLineSegment(sketch, "E2480", {"start": v(-2.41, 1.49) * mm, "end": v(-2.27, 1.4) * mm});
            skLineSegment(sketch, "E2481", {"start": v(-2.27, 1.4) * mm, "end": v(-2.12, 1.32) * mm});
            skLineSegment(sketch, "E2482", {"start": v(-2.12, 1.32) * mm, "end": v(-1.92, 1.22) * mm});
            skLineSegment(sketch, "E2483", {"start": v(-1.92, 1.22) * mm, "end": v(-1.81, 1.17) * mm});
            skLineSegment(sketch, "E2484", {"start": v(-1.81, 1.17) * mm, "end": v(-1.72, 1.13) * mm});
            skLineSegment(sketch, "E2485", {"start": v(-1.72, 1.13) * mm, "end": v(-1.64, 1.1) * mm});
            skLineSegment(sketch, "E2486", {"start": v(-1.64, 1.1) * mm, "end": v(-1.57, 1.06) * mm});
            skLineSegment(sketch, "E2487", {"start": v(-1.57, 1.06) * mm, "end": v(-1.5, 1.04) * mm});
            skLineSegment(sketch, "E2488", {"start": v(-1.5, 1.04) * mm, "end": v(-1.44, 1.01) * mm});
            skLineSegment(sketch, "E2489", {"start": v(-1.44, 1.01) * mm, "end": v(-1.38, 1) * mm});
            skLineSegment(sketch, "E2490", {"start": v(-1.38, 1) * mm, "end": v(-1.32, 0.97) * mm});
            skLineSegment(sketch, "E2491", {"start": v(-1.32, 0.97) * mm, "end": v(-1.25, 0.95) * mm});
            skLineSegment(sketch, "E2492", {"start": v(-1.25, 0.95) * mm, "end": v(-1.22, 0.95) * mm});
            skLineSegment(sketch, "E2493", {"start": v(-1.22, 0.95) * mm, "end": v(-1.2, 0.94) * mm});
            skLineSegment(sketch, "E2494", {"start": v(-1.2, 0.94) * mm, "end": v(-1.2, 0.95) * mm});
            skLineSegment(sketch, "E2495", {"start": v(6.87, 1.4) * mm, "end": v(6.92, 1.46) * mm});
            skLineSegment(sketch, "E2496", {"start": v(6.92, 1.46) * mm, "end": v(6.97, 1.5) * mm});
            skLineSegment(sketch, "E2497", {"start": v(6.97, 1.5) * mm, "end": v(7.02, 1.55) * mm});
            skLineSegment(sketch, "E2498", {"start": v(7.02, 1.55) * mm, "end": v(7.04, 1.59) * mm});
            skLineSegment(sketch, "E2499", {"start": v(7.04, 1.59) * mm, "end": v(7.07, 1.62) * mm});
            skLineSegment(sketch, "E2500", {"start": v(7.07, 1.62) * mm, "end": v(7.1, 1.65) * mm});
            skLineSegment(sketch, "E2501", {"start": v(7.1, 1.65) * mm, "end": v(7.12, 1.69) * mm});
            skLineSegment(sketch, "E2502", {"start": v(7.12, 1.69) * mm, "end": v(7.14, 1.72) * mm});
            skLineSegment(sketch, "E2503", {"start": v(7.14, 1.72) * mm, "end": v(7.17, 1.76) * mm});
            skLineSegment(sketch, "E2504", {"start": v(7.17, 1.76) * mm, "end": v(7.2, 1.81) * mm});
            skLineSegment(sketch, "E2505", {"start": v(7.2, 1.81) * mm, "end": v(7.25, 1.87) * mm});
            skLineSegment(sketch, "E2506", {"start": v(7.25, 1.87) * mm, "end": v(7.28, 1.93) * mm});
            skLineSegment(sketch, "E2507", {"start": v(7.28, 1.93) * mm, "end": v(7.32, 1.98) * mm});
            skLineSegment(sketch, "E2508", {"start": v(7.32, 1.98) * mm, "end": v(7.34, 2.02) * mm});
            skLineSegment(sketch, "E2509", {"start": v(7.34, 2.02) * mm, "end": v(7.36, 2.06) * mm});
            skLineSegment(sketch, "E2510", {"start": v(7.36, 2.06) * mm, "end": v(7.37, 2.08) * mm});
            skLineSegment(sketch, "E2511", {"start": v(7.37, 2.08) * mm, "end": v(7.33, 2.1) * mm});
            skLineSegment(sketch, "E2512", {"start": v(7.33, 2.1) * mm, "end": v(7.24, 2.1) * mm});
            skLineSegment(sketch, "E2513", {"start": v(7.24, 2.1) * mm, "end": v(7.13, 2.12) * mm});
            skLineSegment(sketch, "E2514", {"start": v(7.13, 2.12) * mm, "end": v(7.04, 2.11) * mm});
            skLineSegment(sketch, "E2515", {"start": v(7.04, 2.11) * mm, "end": v(6.82, 2.08) * mm});
            skLineSegment(sketch, "E2516", {"start": v(6.82, 2.08) * mm, "end": v(6.62, 2.03) * mm});
            skLineSegment(sketch, "E2517", {"start": v(6.62, 2.03) * mm, "end": v(6.42, 1.96) * mm});
            skLineSegment(sketch, "E2518", {"start": v(6.42, 1.96) * mm, "end": v(6.2, 1.86) * mm});
            skLineSegment(sketch, "E2519", {"start": v(6.2, 1.86) * mm, "end": v(6.08, 1.8) * mm});
            skLineSegment(sketch, "E2520", {"start": v(6.08, 1.8) * mm, "end": v(6, 1.77) * mm});
            skLineSegment(sketch, "E2521", {"start": v(6, 1.77) * mm, "end": v(5.92, 1.74) * mm});
            skLineSegment(sketch, "E2522", {"start": v(5.92, 1.74) * mm, "end": v(5.85, 1.72) * mm});
            skLineSegment(sketch, "E2523", {"start": v(5.85, 1.72) * mm, "end": v(5.73, 1.7) * mm});
            skLineSegment(sketch, "E2524", {"start": v(5.73, 1.7) * mm, "end": v(5.83, 1.67) * mm});
            skLineSegment(sketch, "E2525", {"start": v(5.83, 1.67) * mm, "end": v(5.87, 1.66) * mm});
            skLineSegment(sketch, "E2526", {"start": v(5.87, 1.66) * mm, "end": v(5.91, 1.65) * mm});
            skLineSegment(sketch, "E2527", {"start": v(5.91, 1.65) * mm, "end": v(5.95, 1.64) * mm});
            skLineSegment(sketch, "E2528", {"start": v(5.95, 1.64) * mm, "end": v(5.99, 1.63) * mm});
            skLineSegment(sketch, "E2529", {"start": v(5.99, 1.63) * mm, "end": v(6.04, 1.6) * mm});
            skLineSegment(sketch, "E2530", {"start": v(6.04, 1.6) * mm, "end": v(6.1, 1.58) * mm});
            skLineSegment(sketch, "E2531", {"start": v(6.1, 1.58) * mm, "end": v(6.17, 1.55) * mm});
            skLineSegment(sketch, "E2532", {"start": v(6.17, 1.55) * mm, "end": v(6.26, 1.5) * mm});
            skLineSegment(sketch, "E2533", {"start": v(6.26, 1.5) * mm, "end": v(6.32, 1.47) * mm});
            skLineSegment(sketch, "E2534", {"start": v(6.32, 1.47) * mm, "end": v(6.39, 1.44) * mm});
            skLineSegment(sketch, "E2535", {"start": v(6.39, 1.44) * mm, "end": v(6.45, 1.4) * mm});
            skLineSegment(sketch, "E2536", {"start": v(6.45, 1.4) * mm, "end": v(6.52, 1.36) * mm});
            skLineSegment(sketch, "E2537", {"start": v(6.52, 1.36) * mm, "end": v(6.57, 1.33) * mm});
            skLineSegment(sketch, "E2538", {"start": v(6.57, 1.33) * mm, "end": v(6.62, 1.3) * mm});
            skLineSegment(sketch, "E2539", {"start": v(6.62, 1.3) * mm, "end": v(6.65, 1.27) * mm});
            skLineSegment(sketch, "E2540", {"start": v(6.65, 1.27) * mm, "end": v(6.67, 1.25) * mm});
            skLineSegment(sketch, "E2541", {"start": v(6.67, 1.25) * mm, "end": v(6.68, 1.25) * mm});
            skLineSegment(sketch, "E2542", {"start": v(6.68, 1.25) * mm, "end": v(6.68, 1.25) * mm});
            skLineSegment(sketch, "E2543", {"start": v(6.68, 1.25) * mm, "end": v(6.7, 1.26) * mm});
            skLineSegment(sketch, "E2544", {"start": v(6.7, 1.26) * mm, "end": v(6.7, 1.27) * mm});
            skLineSegment(sketch, "E2545", {"start": v(6.7, 1.27) * mm, "end": v(6.73, 1.29) * mm});
            skLineSegment(sketch, "E2546", {"start": v(6.73, 1.29) * mm, "end": v(6.77, 1.32) * mm});
            skLineSegment(sketch, "E2547", {"start": v(6.77, 1.32) * mm, "end": v(6.81, 1.36) * mm});
            skLineSegment(sketch, "E2548", {"start": v(6.81, 1.36) * mm, "end": v(6.87, 1.4) * mm});
            skLineSegment(sketch, "E2549", {"start": v(2.16, 1.35) * mm, "end": v(2.2, 1.37) * mm});
            skLineSegment(sketch, "E2550", {"start": v(2.2, 1.37) * mm, "end": v(2.25, 1.39) * mm});
            skLineSegment(sketch, "E2551", {"start": v(2.25, 1.39) * mm, "end": v(2.3, 1.4) * mm});
            skLineSegment(sketch, "E2552", {"start": v(2.3, 1.4) * mm, "end": v(2.33, 1.42) * mm});
            skLineSegment(sketch, "E2553", {"start": v(2.33, 1.42) * mm, "end": v(2.4, 1.45) * mm});
            skLineSegment(sketch, "E2554", {"start": v(2.4, 1.45) * mm, "end": v(2.51, 1.48) * mm});
            skLineSegment(sketch, "E2555", {"start": v(2.51, 1.48) * mm, "end": v(2.64, 1.5) * mm});
            skLineSegment(sketch, "E2556", {"start": v(2.64, 1.5) * mm, "end": v(2.78, 1.54) * mm});
            skLineSegment(sketch, "E2557", {"start": v(2.78, 1.54) * mm, "end": v(2.92, 1.57) * mm});
            skLineSegment(sketch, "E2558", {"start": v(2.92, 1.57) * mm, "end": v(3.07, 1.6) * mm});
            skLineSegment(sketch, "E2559", {"start": v(3.07, 1.6) * mm, "end": v(3.2, 1.62) * mm});
            skLineSegment(sketch, "E2560", {"start": v(3.2, 1.62) * mm, "end": v(3.33, 1.63) * mm});
            skLineSegment(sketch, "E2561", {"start": v(3.33, 1.63) * mm, "end": v(3.45, 1.64) * mm});
            skLineSegment(sketch, "E2562", {"start": v(3.45, 1.64) * mm, "end": v(3.57, 1.66) * mm});
            skLineSegment(sketch, "E2563", {"start": v(3.57, 1.66) * mm, "end": v(3.7, 1.67) * mm});
            skLineSegment(sketch, "E2564", {"start": v(3.7, 1.67) * mm, "end": v(3.87, 1.69) * mm});
            skLineSegment(sketch, "E2565", {"start": v(3.87, 1.69) * mm, "end": v(3.96, 1.7) * mm});
            skLineSegment(sketch, "E2566", {"start": v(3.96, 1.7) * mm, "end": v(4.06, 1.7) * mm});
            skLineSegment(sketch, "E2567", {"start": v(4.06, 1.7) * mm, "end": v(4.16, 1.71) * mm});
            skLineSegment(sketch, "E2568", {"start": v(4.16, 1.71) * mm, "end": v(4.26, 1.72) * mm});
            skLineSegment(sketch, "E2569", {"start": v(4.26, 1.72) * mm, "end": v(4.35, 1.73) * mm});
            skLineSegment(sketch, "E2570", {"start": v(4.35, 1.73) * mm, "end": v(4.43, 1.74) * mm});
            skLineSegment(sketch, "E2571", {"start": v(4.43, 1.74) * mm, "end": v(4.5, 1.75) * mm});
            skLineSegment(sketch, "E2572", {"start": v(4.5, 1.75) * mm, "end": v(4.54, 1.75) * mm});
            skLineSegment(sketch, "E2573", {"start": v(4.54, 1.75) * mm, "end": v(4.6, 1.76) * mm});
            skLineSegment(sketch, "E2574", {"start": v(4.6, 1.76) * mm, "end": v(4.64, 1.76) * mm});
            skLineSegment(sketch, "E2575", {"start": v(4.64, 1.76) * mm, "end": v(4.7, 1.78) * mm});
            skLineSegment(sketch, "E2576", {"start": v(4.7, 1.78) * mm, "end": v(4.78, 1.8) * mm});
            skLineSegment(sketch, "E2577", {"start": v(4.78, 1.8) * mm, "end": v(4.87, 1.84) * mm});
            skLineSegment(sketch, "E2578", {"start": v(4.87, 1.84) * mm, "end": v(4.95, 1.87) * mm});
            skLineSegment(sketch, "E2579", {"start": v(4.95, 1.87) * mm, "end": v(5, 1.9) * mm});
            skLineSegment(sketch, "E2580", {"start": v(5, 1.9) * mm, "end": v(5.08, 1.95) * mm});
            skLineSegment(sketch, "E2581", {"start": v(5.08, 1.95) * mm, "end": v(5.16, 2) * mm});
            skLineSegment(sketch, "E2582", {"start": v(5.16, 2) * mm, "end": v(5.24, 2.06) * mm});
            skLineSegment(sketch, "E2583", {"start": v(5.24, 2.06) * mm, "end": v(5.32, 2.11) * mm});
            skLineSegment(sketch, "E2584", {"start": v(5.32, 2.11) * mm, "end": v(5.39, 2.16) * mm});
            skLineSegment(sketch, "E2585", {"start": v(5.39, 2.16) * mm, "end": v(5.45, 2.2) * mm});
            skLineSegment(sketch, "E2586", {"start": v(5.45, 2.2) * mm, "end": v(5.48, 2.24) * mm});
            skLineSegment(sketch, "E2587", {"start": v(5.48, 2.24) * mm, "end": v(5.5, 2.26) * mm});
            skLineSegment(sketch, "E2588", {"start": v(5.5, 2.26) * mm, "end": v(5.53, 2.28) * mm});
            skLineSegment(sketch, "E2589", {"start": v(5.53, 2.28) * mm, "end": v(5.56, 2.3) * mm});
            skLineSegment(sketch, "E2590", {"start": v(5.56, 2.3) * mm, "end": v(5.59, 2.33) * mm});
            skLineSegment(sketch, "E2591", {"start": v(5.59, 2.33) * mm, "end": v(5.61, 2.36) * mm});
            skLineSegment(sketch, "E2592", {"start": v(5.61, 2.36) * mm, "end": v(5.63, 2.37) * mm});
            skLineSegment(sketch, "E2593", {"start": v(5.63, 2.37) * mm, "end": v(5.65, 2.39) * mm});
            skLineSegment(sketch, "E2594", {"start": v(5.65, 2.39) * mm, "end": v(5.65, 2.4) * mm});
            skLineSegment(sketch, "E2595", {"start": v(5.65, 2.4) * mm, "end": v(5.64, 2.4) * mm});
            skLineSegment(sketch, "E2596", {"start": v(5.64, 2.4) * mm, "end": v(5.62, 2.4) * mm});
            skLineSegment(sketch, "E2597", {"start": v(5.62, 2.4) * mm, "end": v(5.58, 2.39) * mm});
            skLineSegment(sketch, "E2598", {"start": v(5.58, 2.39) * mm, "end": v(5.54, 2.38) * mm});
            skLineSegment(sketch, "E2599", {"start": v(5.54, 2.38) * mm, "end": v(5.41, 2.35) * mm});
            skLineSegment(sketch, "E2600", {"start": v(5.41, 2.35) * mm, "end": v(5.27, 2.34) * mm});
            skLineSegment(sketch, "E2601", {"start": v(5.27, 2.34) * mm, "end": v(5.1, 2.33) * mm});
            skLineSegment(sketch, "E2602", {"start": v(5.1, 2.33) * mm, "end": v(4.93, 2.32) * mm});
            skLineSegment(sketch, "E2603", {"start": v(4.93, 2.32) * mm, "end": v(4.74, 2.33) * mm});
            skLineSegment(sketch, "E2604", {"start": v(4.74, 2.33) * mm, "end": v(4.56, 2.33) * mm});
            skLineSegment(sketch, "E2605", {"start": v(4.56, 2.33) * mm, "end": v(4.37, 2.35) * mm});
            skLineSegment(sketch, "E2606", {"start": v(4.37, 2.35) * mm, "end": v(4.18, 2.37) * mm});
            skLineSegment(sketch, "E2607", {"start": v(4.18, 2.37) * mm, "end": v(3.98, 2.4) * mm});
            skLineSegment(sketch, "E2608", {"start": v(3.98, 2.4) * mm, "end": v(3.83, 2.4) * mm});
            skLineSegment(sketch, "E2609", {"start": v(3.83, 2.4) * mm, "end": v(3.7, 2.4) * mm});
            skLineSegment(sketch, "E2610", {"start": v(3.7, 2.4) * mm, "end": v(3.57, 2.37) * mm});
            skLineSegment(sketch, "E2611", {"start": v(3.57, 2.37) * mm, "end": v(3.28, 2.29) * mm});
            skLineSegment(sketch, "E2612", {"start": v(3.28, 2.29) * mm, "end": v(3.05, 2.2) * mm});
            skLineSegment(sketch, "E2613", {"start": v(3.05, 2.2) * mm, "end": v(2.85, 2.12) * mm});
            skLineSegment(sketch, "E2614", {"start": v(2.85, 2.12) * mm, "end": v(2.66, 2) * mm});
            skLineSegment(sketch, "E2615", {"start": v(2.66, 2) * mm, "end": v(2.56, 1.93) * mm});
            skLineSegment(sketch, "E2616", {"start": v(2.56, 1.93) * mm, "end": v(2.47, 1.85) * mm});
            skLineSegment(sketch, "E2617", {"start": v(2.47, 1.85) * mm, "end": v(2.37, 1.75) * mm});
            skLineSegment(sketch, "E2618", {"start": v(2.37, 1.75) * mm, "end": v(2.25, 1.6) * mm});
            skLineSegment(sketch, "E2619", {"start": v(2.25, 1.6) * mm, "end": v(2.23, 1.57) * mm});
            skLineSegment(sketch, "E2620", {"start": v(2.23, 1.57) * mm, "end": v(2.2, 1.54) * mm});
            skLineSegment(sketch, "E2621", {"start": v(2.2, 1.54) * mm, "end": v(2.17, 1.51) * mm});
            skLineSegment(sketch, "E2622", {"start": v(2.17, 1.51) * mm, "end": v(2.15, 1.5) * mm});
            skLineSegment(sketch, "E2623", {"start": v(2.15, 1.5) * mm, "end": v(2.14, 1.47) * mm});
            skLineSegment(sketch, "E2624", {"start": v(2.14, 1.47) * mm, "end": v(2.12, 1.45) * mm});
            skLineSegment(sketch, "E2625", {"start": v(2.12, 1.45) * mm, "end": v(2.1, 1.42) * mm});
            skLineSegment(sketch, "E2626", {"start": v(2.1, 1.42) * mm, "end": v(2.08, 1.4) * mm});
            skLineSegment(sketch, "E2627", {"start": v(2.08, 1.4) * mm, "end": v(2.07, 1.37) * mm});
            skLineSegment(sketch, "E2628", {"start": v(2.07, 1.37) * mm, "end": v(2.05, 1.35) * mm});
            skLineSegment(sketch, "E2629", {"start": v(2.05, 1.35) * mm, "end": v(2.05, 1.34) * mm});
            skLineSegment(sketch, "E2630", {"start": v(2.05, 1.34) * mm, "end": v(2.05, 1.32) * mm});
            skLineSegment(sketch, "E2631", {"start": v(2.05, 1.32) * mm, "end": v(2.05, 1.31) * mm});
            skLineSegment(sketch, "E2632", {"start": v(2.05, 1.31) * mm, "end": v(2.06, 1.3) * mm});
            skLineSegment(sketch, "E2633", {"start": v(2.06, 1.3) * mm, "end": v(2.07, 1.31) * mm});
            skLineSegment(sketch, "E2634", {"start": v(2.07, 1.31) * mm, "end": v(2.09, 1.32) * mm});
            skLineSegment(sketch, "E2635", {"start": v(2.09, 1.32) * mm, "end": v(2.12, 1.33) * mm});
            skLineSegment(sketch, "E2636", {"start": v(2.12, 1.33) * mm, "end": v(2.16, 1.35) * mm});
            skLineSegment(sketch, "E2637", {"start": v(-7.96, 1.53) * mm, "end": v(-7.87, 1.55) * mm});
            skLineSegment(sketch, "E2638", {"start": v(-7.87, 1.55) * mm, "end": v(-7.77, 1.57) * mm});
            skLineSegment(sketch, "E2639", {"start": v(-7.77, 1.57) * mm, "end": v(-7.68, 1.58) * mm});
            skLineSegment(sketch, "E2640", {"start": v(-7.68, 1.58) * mm, "end": v(-7.62, 1.6) * mm});
            skLineSegment(sketch, "E2641", {"start": v(-7.62, 1.6) * mm, "end": v(-7.56, 1.6) * mm});
            skLineSegment(sketch, "E2642", {"start": v(-7.56, 1.6) * mm, "end": v(-7.51, 1.6) * mm});
            skLineSegment(sketch, "E2643", {"start": v(-7.51, 1.6) * mm, "end": v(-7.47, 1.61) * mm});
            skLineSegment(sketch, "E2644", {"start": v(-7.47, 1.61) * mm, "end": v(-7.44, 1.62) * mm});
            skLineSegment(sketch, "E2645", {"start": v(-7.44, 1.62) * mm, "end": v(-7.4, 1.63) * mm});
            skLineSegment(sketch, "E2646", {"start": v(-7.4, 1.63) * mm, "end": v(-7.35, 1.63) * mm});
            skLineSegment(sketch, "E2647", {"start": v(-7.35, 1.63) * mm, "end": v(-7.27, 1.64) * mm});
            skLineSegment(sketch, "E2648", {"start": v(-7.27, 1.64) * mm, "end": v(-7.19, 1.65) * mm});
            skLineSegment(sketch, "E2649", {"start": v(-7.19, 1.65) * mm, "end": v(-7.1, 1.66) * mm});
            skLineSegment(sketch, "E2650", {"start": v(-7.1, 1.66) * mm, "end": v(-7.02, 1.67) * mm});
            skLineSegment(sketch, "E2651", {"start": v(-7.02, 1.67) * mm, "end": v(-6.96, 1.68) * mm});
            skLineSegment(sketch, "E2652", {"start": v(-6.96, 1.68) * mm, "end": v(-6.92, 1.69) * mm});
            skLineSegment(sketch, "E2653", {"start": v(-6.92, 1.69) * mm, "end": v(-6.88, 1.7) * mm});
            skLineSegment(sketch, "E2654", {"start": v(-6.88, 1.7) * mm, "end": v(-6.83, 1.7) * mm});
            skLineSegment(sketch, "E2655", {"start": v(-6.83, 1.7) * mm, "end": v(-6.76, 1.7) * mm});
            skLineSegment(sketch, "E2656", {"start": v(-6.76, 1.7) * mm, "end": v(-6.7, 1.7) * mm});
            skLineSegment(sketch, "E2657", {"start": v(-6.7, 1.7) * mm, "end": v(-6.62, 1.7) * mm});
            skLineSegment(sketch, "E2658", {"start": v(-6.62, 1.7) * mm, "end": v(-6.58, 1.71) * mm});
            skLineSegment(sketch, "E2659", {"start": v(-6.58, 1.71) * mm, "end": v(-6.56, 1.72) * mm});
            skLineSegment(sketch, "E2660", {"start": v(-6.56, 1.72) * mm, "end": v(-6.56, 1.72) * mm});
            skLineSegment(sketch, "E2661", {"start": v(-6.56, 1.72) * mm, "end": v(-6.59, 1.74) * mm});
            skLineSegment(sketch, "E2662", {"start": v(-6.59, 1.74) * mm, "end": v(-6.64, 1.76) * mm});
            skLineSegment(sketch, "E2663", {"start": v(-6.64, 1.76) * mm, "end": v(-6.7, 1.8) * mm});
            skLineSegment(sketch, "E2664", {"start": v(-6.7, 1.8) * mm, "end": v(-6.79, 1.83) * mm});
            skLineSegment(sketch, "E2665", {"start": v(-6.79, 1.83) * mm, "end": v(-6.92, 1.89) * mm});
            skLineSegment(sketch, "E2666", {"start": v(-6.92, 1.89) * mm, "end": v(-7.02, 1.94) * mm});
            skLineSegment(sketch, "E2667", {"start": v(-7.02, 1.94) * mm, "end": v(-7.13, 2) * mm});
            skLineSegment(sketch, "E2668", {"start": v(-7.13, 2) * mm, "end": v(-7.25, 2.08) * mm});
            skLineSegment(sketch, "E2669", {"start": v(-7.25, 2.08) * mm, "end": v(-7.3, 2.11) * mm});
            skLineSegment(sketch, "E2670", {"start": v(-7.3, 2.11) * mm, "end": v(-7.34, 2.13) * mm});
            skLineSegment(sketch, "E2671", {"start": v(-7.34, 2.13) * mm, "end": v(-7.37, 2.14) * mm});
            skLineSegment(sketch, "E2672", {"start": v(-7.37, 2.14) * mm, "end": v(-7.42, 2.15) * mm});
            skLineSegment(sketch, "E2673", {"start": v(-7.42, 2.15) * mm, "end": v(-7.58, 2.18) * mm});
            skLineSegment(sketch, "E2674", {"start": v(-7.58, 2.18) * mm, "end": v(-7.75, 2.22) * mm});
            skLineSegment(sketch, "E2675", {"start": v(-7.75, 2.22) * mm, "end": v(-7.9, 2.26) * mm});
            skLineSegment(sketch, "E2676", {"start": v(-7.9, 2.26) * mm, "end": v(-8, 2.29) * mm});
            skLineSegment(sketch, "E2677", {"start": v(-8, 2.29) * mm, "end": v(-8.05, 2.3) * mm});
            skLineSegment(sketch, "E2678", {"start": v(-8.05, 2.3) * mm, "end": v(-8.1, 2.35) * mm});
            skLineSegment(sketch, "E2679", {"start": v(-8.1, 2.35) * mm, "end": v(-8.18, 2.4) * mm});
            skLineSegment(sketch, "E2680", {"start": v(-8.18, 2.4) * mm, "end": v(-8.26, 2.44) * mm});
            skLineSegment(sketch, "E2681", {"start": v(-8.26, 2.44) * mm, "end": v(-8.34, 2.5) * mm});
            skLineSegment(sketch, "E2682", {"start": v(-8.34, 2.5) * mm, "end": v(-8.42, 2.56) * mm});
            skLineSegment(sketch, "E2683", {"start": v(-8.42, 2.56) * mm, "end": v(-8.5, 2.62) * mm});
            skLineSegment(sketch, "E2684", {"start": v(-8.5, 2.62) * mm, "end": v(-8.56, 2.67) * mm});
            skLineSegment(sketch, "E2685", {"start": v(-8.56, 2.67) * mm, "end": v(-8.65, 2.75) * mm});
            skLineSegment(sketch, "E2686", {"start": v(-8.65, 2.75) * mm, "end": v(-8.66, 2.71) * mm});
            skLineSegment(sketch, "E2687", {"start": v(-8.66, 2.71) * mm, "end": v(-8.66, 2.66) * mm});
            skLineSegment(sketch, "E2688", {"start": v(-8.66, 2.66) * mm, "end": v(-8.66, 2.56) * mm});
            skLineSegment(sketch, "E2689", {"start": v(-8.66, 2.56) * mm, "end": v(-8.65, 2.43) * mm});
            skLineSegment(sketch, "E2690", {"start": v(-8.65, 2.43) * mm, "end": v(-8.63, 2.3) * mm});
            skLineSegment(sketch, "E2691", {"start": v(-8.63, 2.3) * mm, "end": v(-8.6, 2.17) * mm});
            skLineSegment(sketch, "E2692", {"start": v(-8.6, 2.17) * mm, "end": v(-8.57, 2.02) * mm});
            skLineSegment(sketch, "E2693", {"start": v(-8.57, 2.02) * mm, "end": v(-8.54, 1.9) * mm});
            skLineSegment(sketch, "E2694", {"start": v(-8.54, 1.9) * mm, "end": v(-8.51, 1.81) * mm});
            skLineSegment(sketch, "E2695", {"start": v(-8.51, 1.81) * mm, "end": v(-8.5, 1.79) * mm});
            skLineSegment(sketch, "E2696", {"start": v(-8.5, 1.79) * mm, "end": v(-8.49, 1.75) * mm});
            skLineSegment(sketch, "E2697", {"start": v(-8.49, 1.75) * mm, "end": v(-8.47, 1.72) * mm});
            skLineSegment(sketch, "E2698", {"start": v(-8.47, 1.72) * mm, "end": v(-8.46, 1.68) * mm});
            skLineSegment(sketch, "E2699", {"start": v(-8.46, 1.68) * mm, "end": v(-8.44, 1.6) * mm});
            skLineSegment(sketch, "E2700", {"start": v(-8.44, 1.6) * mm, "end": v(-8.4, 1.54) * mm});
            skLineSegment(sketch, "E2701", {"start": v(-8.4, 1.54) * mm, "end": v(-8.38, 1.5) * mm});
            skLineSegment(sketch, "E2702", {"start": v(-8.38, 1.5) * mm, "end": v(-8.35, 1.46) * mm});
            skLineSegment(sketch, "E2703", {"start": v(-8.35, 1.46) * mm, "end": v(-8.33, 1.43) * mm});
            skLineSegment(sketch, "E2704", {"start": v(-8.33, 1.43) * mm, "end": v(-8.26, 1.45) * mm});
            skLineSegment(sketch, "E2705", {"start": v(-8.26, 1.45) * mm, "end": v(-8.21, 1.47) * mm});
            skLineSegment(sketch, "E2706", {"start": v(-8.21, 1.47) * mm, "end": v(-8.14, 1.48) * mm});
            skLineSegment(sketch, "E2707", {"start": v(-8.14, 1.48) * mm, "end": v(-8.05, 1.5) * mm});
            skLineSegment(sketch, "E2708", {"start": v(-8.05, 1.5) * mm, "end": v(-7.96, 1.53) * mm});
            skLineSegment(sketch, "E2709", {"start": v(-2.98, 1.63) * mm, "end": v(-2.98, 1.64) * mm});
            skLineSegment(sketch, "E2710", {"start": v(-2.98, 1.64) * mm, "end": v(-3, 1.66) * mm});
            skLineSegment(sketch, "E2711", {"start": v(-3, 1.66) * mm, "end": v(-3.02, 1.69) * mm});
            skLineSegment(sketch, "E2712", {"start": v(-3.02, 1.69) * mm, "end": v(-3.04, 1.72) * mm});
            skLineSegment(sketch, "E2713", {"start": v(-3.04, 1.72) * mm, "end": v(-3.16, 1.9) * mm});
            skLineSegment(sketch, "E2714", {"start": v(-3.16, 1.9) * mm, "end": v(-3.24, 2.07) * mm});
            skLineSegment(sketch, "E2715", {"start": v(-3.24, 2.07) * mm, "end": v(-3.26, 2.12) * mm});
            skLineSegment(sketch, "E2716", {"start": v(-3.26, 2.12) * mm, "end": v(-3.26, 2.16) * mm});
            skLineSegment(sketch, "E2717", {"start": v(-3.26, 2.16) * mm, "end": v(-3.27, 2.2) * mm});
            skLineSegment(sketch, "E2718", {"start": v(-3.27, 2.2) * mm, "end": v(-3.27, 2.26) * mm});
            skLineSegment(sketch, "E2719", {"start": v(-3.27, 2.26) * mm, "end": v(-3.26, 2.3) * mm});
            skLineSegment(sketch, "E2720", {"start": v(-3.26, 2.3) * mm, "end": v(-3.26, 2.34) * mm});
            skLineSegment(sketch, "E2721", {"start": v(-3.26, 2.34) * mm, "end": v(-3.26, 2.36) * mm});
            skLineSegment(sketch, "E2722", {"start": v(-3.26, 2.36) * mm, "end": v(-3.25, 2.38) * mm});
            skLineSegment(sketch, "E2723", {"start": v(-3.25, 2.38) * mm, "end": v(-3.26, 2.4) * mm});
            skLineSegment(sketch, "E2724", {"start": v(-3.26, 2.4) * mm, "end": v(-3.32, 2.41) * mm});
            skLineSegment(sketch, "E2725", {"start": v(-3.32, 2.41) * mm, "end": v(-3.42, 2.44) * mm});
            skLineSegment(sketch, "E2726", {"start": v(-3.42, 2.44) * mm, "end": v(-3.59, 2.48) * mm});
            skLineSegment(sketch, "E2727", {"start": v(-3.59, 2.48) * mm, "end": v(-3.98, 2.55) * mm});
            skLineSegment(sketch, "E2728", {"start": v(-3.98, 2.55) * mm, "end": v(-4.39, 2.57) * mm});
            skLineSegment(sketch, "E2729", {"start": v(-4.39, 2.57) * mm, "end": v(-4.8, 2.56) * mm});
            skLineSegment(sketch, "E2730", {"start": v(-4.8, 2.56) * mm, "end": v(-5.2, 2.5) * mm});
            skLineSegment(sketch, "E2731", {"start": v(-5.2, 2.5) * mm, "end": v(-5.26, 2.49) * mm});
            skLineSegment(sketch, "E2732", {"start": v(-5.26, 2.49) * mm, "end": v(-5.34, 2.47) * mm});
            skLineSegment(sketch, "E2733", {"start": v(-5.34, 2.47) * mm, "end": v(-5.43, 2.45) * mm});
            skLineSegment(sketch, "E2734", {"start": v(-5.43, 2.45) * mm, "end": v(-5.52, 2.44) * mm});
            skLineSegment(sketch, "E2735", {"start": v(-5.52, 2.44) * mm, "end": v(-5.72, 2.4) * mm});
            skLineSegment(sketch, "E2736", {"start": v(-5.72, 2.4) * mm, "end": v(-5.88, 2.37) * mm});
            skLineSegment(sketch, "E2737", {"start": v(-5.88, 2.37) * mm, "end": v(-6, 2.34) * mm});
            skLineSegment(sketch, "E2738", {"start": v(-6, 2.34) * mm, "end": v(-6.1, 2.32) * mm});
            skLineSegment(sketch, "E2739", {"start": v(-6.1, 2.32) * mm, "end": v(-6.14, 2.3) * mm});
            skLineSegment(sketch, "E2740", {"start": v(-6.14, 2.3) * mm, "end": v(-6.2, 2.29) * mm});
            skLineSegment(sketch, "E2741", {"start": v(-6.2, 2.29) * mm, "end": v(-6.29, 2.27) * mm});
            skLineSegment(sketch, "E2742", {"start": v(-6.29, 2.27) * mm, "end": v(-6.37, 2.25) * mm});
            skLineSegment(sketch, "E2743", {"start": v(-6.37, 2.25) * mm, "end": v(-6.45, 2.23) * mm});
            skLineSegment(sketch, "E2744", {"start": v(-6.45, 2.23) * mm, "end": v(-6.52, 2.22) * mm});
            skLineSegment(sketch, "E2745", {"start": v(-6.52, 2.22) * mm, "end": v(-6.57, 2.21) * mm});
            skLineSegment(sketch, "E2746", {"start": v(-6.57, 2.21) * mm, "end": v(-6.6, 2.2) * mm});
            skLineSegment(sketch, "E2747", {"start": v(-6.6, 2.2) * mm, "end": v(-6.64, 2.2) * mm});
            skLineSegment(sketch, "E2748", {"start": v(-6.64, 2.2) * mm, "end": v(-6.65, 2.2) * mm});
            skLineSegment(sketch, "E2749", {"start": v(-6.65, 2.2) * mm, "end": v(-6.63, 2.17) * mm});
            skLineSegment(sketch, "E2750", {"start": v(-6.63, 2.17) * mm, "end": v(-6.58, 2.13) * mm});
            skLineSegment(sketch, "E2751", {"start": v(-6.58, 2.13) * mm, "end": v(-6.49, 2.08) * mm});
            skLineSegment(sketch, "E2752", {"start": v(-6.49, 2.08) * mm, "end": v(-6.37, 2.03) * mm});
            skLineSegment(sketch, "E2753", {"start": v(-6.37, 2.03) * mm, "end": v(-6.23, 1.98) * mm});
            skLineSegment(sketch, "E2754", {"start": v(-6.23, 1.98) * mm, "end": v(-6.08, 1.92) * mm});
            skLineSegment(sketch, "E2755", {"start": v(-6.08, 1.92) * mm, "end": v(-5.93, 1.88) * mm});
            skLineSegment(sketch, "E2756", {"start": v(-5.93, 1.88) * mm, "end": v(-5.78, 1.84) * mm});
            skLineSegment(sketch, "E2757", {"start": v(-5.78, 1.84) * mm, "end": v(-5.65, 1.8) * mm});
            skLineSegment(sketch, "E2758", {"start": v(-5.65, 1.8) * mm, "end": v(-5.54, 1.8) * mm});
            skLineSegment(sketch, "E2759", {"start": v(-5.54, 1.8) * mm, "end": v(-5.5, 1.79) * mm});
            skLineSegment(sketch, "E2760", {"start": v(-5.5, 1.79) * mm, "end": v(-5.48, 1.79) * mm});
            skLineSegment(sketch, "E2761", {"start": v(-5.48, 1.79) * mm, "end": v(-5.44, 1.8) * mm});
            skLineSegment(sketch, "E2762", {"start": v(-5.44, 1.8) * mm, "end": v(-5.4, 1.8) * mm});
            skLineSegment(sketch, "E2763", {"start": v(-5.4, 1.8) * mm, "end": v(-5.34, 1.8) * mm});
            skLineSegment(sketch, "E2764", {"start": v(-5.34, 1.8) * mm, "end": v(-5.26, 1.82) * mm});
            skLineSegment(sketch, "E2765", {"start": v(-5.26, 1.82) * mm, "end": v(-5.15, 1.84) * mm});
            skLineSegment(sketch, "E2766", {"start": v(-5.15, 1.84) * mm, "end": v(-5.01, 1.86) * mm});
            skLineSegment(sketch, "E2767", {"start": v(-5.01, 1.86) * mm, "end": v(-4.81, 1.89) * mm});
            skLineSegment(sketch, "E2768", {"start": v(-4.81, 1.89) * mm, "end": v(-4.66, 1.9) * mm});
            skLineSegment(sketch, "E2769", {"start": v(-4.66, 1.9) * mm, "end": v(-4.54, 1.87) * mm});
            skLineSegment(sketch, "E2770", {"start": v(-4.54, 1.87) * mm, "end": v(-4.42, 1.83) * mm});
            skLineSegment(sketch, "E2771", {"start": v(-4.42, 1.83) * mm, "end": v(-4.32, 1.77) * mm});
            skLineSegment(sketch, "E2772", {"start": v(-4.32, 1.77) * mm, "end": v(-4.15, 1.78) * mm});
            skLineSegment(sketch, "E2773", {"start": v(-4.15, 1.78) * mm, "end": v(-4, 1.78) * mm});
            skLineSegment(sketch, "E2774", {"start": v(-4, 1.78) * mm, "end": v(-3.86, 1.77) * mm});
            skLineSegment(sketch, "E2775", {"start": v(-3.86, 1.77) * mm, "end": v(-3.67, 1.75) * mm});
            skLineSegment(sketch, "E2776", {"start": v(-3.67, 1.75) * mm, "end": v(-3.41, 1.71) * mm});
            skLineSegment(sketch, "E2777", {"start": v(-3.41, 1.71) * mm, "end": v(-3.27, 1.69) * mm});
            skLineSegment(sketch, "E2778", {"start": v(-3.27, 1.69) * mm, "end": v(-3.14, 1.66) * mm});
            skLineSegment(sketch, "E2779", {"start": v(-3.14, 1.66) * mm, "end": v(-3.04, 1.64) * mm});
            skLineSegment(sketch, "E2780", {"start": v(-3.04, 1.64) * mm, "end": v(-2.98, 1.62) * mm});
            skLineSegment(sketch, "E2781", {"start": v(-2.98, 1.62) * mm, "end": v(-2.98, 1.63) * mm});
            skLineSegment(sketch, "E2782", {"start": v(-0.42, 1.7) * mm, "end": v(-0.38, 1.72) * mm});
            skLineSegment(sketch, "E2783", {"start": v(-0.38, 1.72) * mm, "end": v(-0.35, 1.76) * mm});
            skLineSegment(sketch, "E2784", {"start": v(-0.35, 1.76) * mm, "end": v(-0.32, 1.8) * mm});
            skLineSegment(sketch, "E2785", {"start": v(-0.32, 1.8) * mm, "end": v(-0.3, 1.83) * mm});
            skLineSegment(sketch, "E2786", {"start": v(-0.3, 1.83) * mm, "end": v(-0.3, 1.86) * mm});
            skLineSegment(sketch, "E2787", {"start": v(-0.3, 1.86) * mm, "end": v(-0.32, 1.88) * mm});
            skLineSegment(sketch, "E2788", {"start": v(-0.32, 1.88) * mm, "end": v(-0.34, 1.89) * mm});
            skLineSegment(sketch, "E2789", {"start": v(-0.34, 1.89) * mm, "end": v(-0.36, 1.89) * mm});
            skLineSegment(sketch, "E2790", {"start": v(-0.36, 1.89) * mm, "end": v(-0.4, 1.87) * mm});
            skLineSegment(sketch, "E2791", {"start": v(-0.4, 1.87) * mm, "end": v(-0.43, 1.84) * mm});
            skLineSegment(sketch, "E2792", {"start": v(-0.43, 1.84) * mm, "end": v(-0.45, 1.82) * mm});
            skLineSegment(sketch, "E2793", {"start": v(-0.45, 1.82) * mm, "end": v(-0.47, 1.81) * mm});
            skLineSegment(sketch, "E2794", {"start": v(-0.47, 1.81) * mm, "end": v(-0.5, 1.81) * mm});
            skLineSegment(sketch, "E2795", {"start": v(-0.5, 1.81) * mm, "end": v(-0.52, 1.81) * mm});
            skLineSegment(sketch, "E2796", {"start": v(-0.52, 1.81) * mm, "end": v(-0.56, 1.82) * mm});
            skLineSegment(sketch, "E2797", {"start": v(-0.56, 1.82) * mm, "end": v(-0.59, 1.84) * mm});
            skLineSegment(sketch, "E2798", {"start": v(-0.59, 1.84) * mm, "end": v(-0.62, 1.86) * mm});
            skLineSegment(sketch, "E2799", {"start": v(-0.62, 1.86) * mm, "end": v(-0.66, 1.91) * mm});
            skLineSegment(sketch, "E2800", {"start": v(-0.66, 1.91) * mm, "end": v(-0.7, 1.99) * mm});
            skLineSegment(sketch, "E2801", {"start": v(-0.7, 1.99) * mm, "end": v(-0.74, 2.07) * mm});
            skLineSegment(sketch, "E2802", {"start": v(-0.74, 2.07) * mm, "end": v(-0.76, 2.17) * mm});
            skLineSegment(sketch, "E2803", {"start": v(-0.76, 2.17) * mm, "end": v(-0.76, 2.28) * mm});
            skLineSegment(sketch, "E2804", {"start": v(-0.76, 2.28) * mm, "end": v(-0.76, 2.38) * mm});
            skLineSegment(sketch, "E2805", {"start": v(-0.76, 2.38) * mm, "end": v(-0.74, 2.46) * mm});
            skLineSegment(sketch, "E2806", {"start": v(-0.74, 2.46) * mm, "end": v(-0.72, 2.54) * mm});
            skLineSegment(sketch, "E2807", {"start": v(-0.72, 2.54) * mm, "end": v(-0.68, 2.62) * mm});
            skLineSegment(sketch, "E2808", {"start": v(-0.68, 2.62) * mm, "end": v(-0.6, 2.73) * mm});
            skLineSegment(sketch, "E2809", {"start": v(-0.6, 2.73) * mm, "end": v(-0.5, 2.84) * mm});
            skLineSegment(sketch, "E2810", {"start": v(-0.5, 2.84) * mm, "end": v(-0.4, 2.93) * mm});
            skLineSegment(sketch, "E2811", {"start": v(-0.4, 2.93) * mm, "end": v(-0.3, 2.98) * mm});
            skLineSegment(sketch, "E2812", {"start": v(-0.3, 2.98) * mm, "end": v(-0.18, 3) * mm});
            skLineSegment(sketch, "E2813", {"start": v(-0.18, 3) * mm, "end": v(-0.07, 2.98) * mm});
            skLineSegment(sketch, "E2814", {"start": v(-0.07, 2.98) * mm, "end": v(-0.02, 2.95) * mm});
            skLineSegment(sketch, "E2815", {"start": v(-0.02, 2.95) * mm, "end": v(0.04, 2.9) * mm});
            skLineSegment(sketch, "E2816", {"start": v(0.04, 2.9) * mm, "end": v(0.09, 2.86) * mm});
            skLineSegment(sketch, "E2817", {"start": v(0.09, 2.86) * mm, "end": v(0.12, 2.8) * mm});
            skLineSegment(sketch, "E2818", {"start": v(0.12, 2.8) * mm, "end": v(0.13, 2.76) * mm});
            skLineSegment(sketch, "E2819", {"start": v(0.13, 2.76) * mm, "end": v(0.13, 2.72) * mm});
            skLineSegment(sketch, "E2820", {"start": v(0.13, 2.72) * mm, "end": v(0.13, 2.68) * mm});
            skLineSegment(sketch, "E2821", {"start": v(0.13, 2.68) * mm, "end": v(0.12, 2.64) * mm});
            skLineSegment(sketch, "E2822", {"start": v(0.12, 2.64) * mm, "end": v(0.1, 2.61) * mm});
            skLineSegment(sketch, "E2823", {"start": v(0.1, 2.61) * mm, "end": v(0.06, 2.58) * mm});
            skLineSegment(sketch, "E2824", {"start": v(0.06, 2.58) * mm, "end": v(0.03, 2.56) * mm});
            skLineSegment(sketch, "E2825", {"start": v(0.03, 2.56) * mm, "end": v(0, 2.55) * mm});
            skLineSegment(sketch, "E2826", {"start": v(0, 2.55) * mm, "end": v(-0.04, 2.54) * mm});
            skLineSegment(sketch, "E2827", {"start": v(-0.04, 2.54) * mm, "end": v(-0.08, 2.5) * mm});
            skLineSegment(sketch, "E2828", {"start": v(-0.08, 2.5) * mm, "end": v(-0.12, 2.46) * mm});
            skLineSegment(sketch, "E2829", {"start": v(-0.12, 2.46) * mm, "end": v(-0.15, 2.4) * mm});
            skLineSegment(sketch, "E2830", {"start": v(-0.15, 2.4) * mm, "end": v(-0.16, 2.35) * mm});
            skLineSegment(sketch, "E2831", {"start": v(-0.16, 2.35) * mm, "end": v(-0.17, 2.3) * mm});
            skLineSegment(sketch, "E2832", {"start": v(-0.17, 2.3) * mm, "end": v(-0.16, 2.25) * mm});
            skLineSegment(sketch, "E2833", {"start": v(-0.16, 2.25) * mm, "end": v(-0.14, 2.2) * mm});
            skLineSegment(sketch, "E2834", {"start": v(-0.14, 2.2) * mm, "end": v(-0.13, 2.18) * mm});
            skLineSegment(sketch, "E2835", {"start": v(-0.13, 2.18) * mm, "end": v(-0.11, 2.16) * mm});
            skLineSegment(sketch, "E2836", {"start": v(-0.11, 2.16) * mm, "end": v(-0.1, 2.15) * mm});
            skLineSegment(sketch, "E2837", {"start": v(-0.1, 2.15) * mm, "end": v(-0.06, 2.14) * mm});
            skLineSegment(sketch, "E2838", {"start": v(-0.06, 2.14) * mm, "end": v(0, 2.13) * mm});
            skLineSegment(sketch, "E2839", {"start": v(0, 2.13) * mm, "end": v(0.05, 2.12) * mm});
            skLineSegment(sketch, "E2840", {"start": v(0.05, 2.12) * mm, "end": v(0.1, 2.12) * mm});
            skLineSegment(sketch, "E2841", {"start": v(0.1, 2.12) * mm, "end": v(0.15, 2.14) * mm});
            skLineSegment(sketch, "E2842", {"start": v(0.15, 2.14) * mm, "end": v(0.2, 2.17) * mm});
            skLineSegment(sketch, "E2843", {"start": v(0.2, 2.17) * mm, "end": v(0.26, 2.22) * mm});
            skLineSegment(sketch, "E2844", {"start": v(0.26, 2.22) * mm, "end": v(0.3, 2.29) * mm});
            skLineSegment(sketch, "E2845", {"start": v(0.3, 2.29) * mm, "end": v(0.34, 2.38) * mm});
            skLineSegment(sketch, "E2846", {"start": v(0.34, 2.38) * mm, "end": v(0.35, 2.43) * mm});
            skLineSegment(sketch, "E2847", {"start": v(0.35, 2.43) * mm, "end": v(0.36, 2.47) * mm});
            skLineSegment(sketch, "E2848", {"start": v(0.36, 2.47) * mm, "end": v(0.37, 2.52) * mm});
            skLineSegment(sketch, "E2849", {"start": v(0.37, 2.52) * mm, "end": v(0.36, 2.6) * mm});
            skLineSegment(sketch, "E2850", {"start": v(0.36, 2.6) * mm, "end": v(0.36, 2.7) * mm});
            skLineSegment(sketch, "E2851", {"start": v(0.36, 2.7) * mm, "end": v(0.34, 2.77) * mm});
            skLineSegment(sketch, "E2852", {"start": v(0.34, 2.77) * mm, "end": v(0.3, 2.84) * mm});
            skLineSegment(sketch, "E2853", {"start": v(0.3, 2.84) * mm, "end": v(0.25, 2.93) * mm});
            skLineSegment(sketch, "E2854", {"start": v(0.25, 2.93) * mm, "end": v(0.2, 3) * mm});
            skLineSegment(sketch, "E2855", {"start": v(0.2, 3) * mm, "end": v(0.15, 3.04) * mm});
            skLineSegment(sketch, "E2856", {"start": v(0.15, 3.04) * mm, "end": v(0.1, 3.09) * mm});
            skLineSegment(sketch, "E2857", {"start": v(0.1, 3.09) * mm, "end": v(0.03, 3.12) * mm});
            skLineSegment(sketch, "E2858", {"start": v(0.03, 3.12) * mm, "end": v(-0.06, 3.16) * mm});
            skLineSegment(sketch, "E2859", {"start": v(-0.06, 3.16) * mm, "end": v(-0.15, 3.18) * mm});
            skLineSegment(sketch, "E2860", {"start": v(-0.15, 3.18) * mm, "end": v(-0.23, 3.19) * mm});
            skLineSegment(sketch, "E2861", {"start": v(-0.23, 3.19) * mm, "end": v(-0.3, 3.18) * mm});
            skLineSegment(sketch, "E2862", {"start": v(-0.3, 3.18) * mm, "end": v(-0.35, 3.17) * mm});
            skLineSegment(sketch, "E2863", {"start": v(-0.35, 3.17) * mm, "end": v(-0.38, 3.16) * mm});
            skLineSegment(sketch, "E2864", {"start": v(-0.38, 3.16) * mm, "end": v(-0.4, 3.16) * mm});
            skLineSegment(sketch, "E2865", {"start": v(-0.4, 3.16) * mm, "end": v(-0.42, 3.15) * mm});
            skLineSegment(sketch, "E2866", {"start": v(-0.42, 3.15) * mm, "end": v(-0.45, 3.14) * mm});
            skLineSegment(sketch, "E2867", {"start": v(-0.45, 3.14) * mm, "end": v(-0.48, 3.12) * mm});
            skLineSegment(sketch, "E2868", {"start": v(-0.48, 3.12) * mm, "end": v(-0.51, 3.1) * mm});
            skLineSegment(sketch, "E2869", {"start": v(-0.51, 3.1) * mm, "end": v(-0.54, 3.09) * mm});
            skLineSegment(sketch, "E2870", {"start": v(-0.54, 3.09) * mm, "end": v(-0.56, 3.08) * mm});
            skLineSegment(sketch, "E2871", {"start": v(-0.56, 3.08) * mm, "end": v(-0.56, 3.08) * mm});
            skLineSegment(sketch, "E2872", {"start": v(-0.56, 3.08) * mm, "end": v(-0.57, 3.07) * mm});
            skLineSegment(sketch, "E2873", {"start": v(-0.57, 3.07) * mm, "end": v(-0.59, 3.06) * mm});
            skLineSegment(sketch, "E2874", {"start": v(-0.59, 3.06) * mm, "end": v(-0.61, 3.04) * mm});
            skLineSegment(sketch, "E2875", {"start": v(-0.61, 3.04) * mm, "end": v(-0.64, 3.02) * mm});
            skLineSegment(sketch, "E2876", {"start": v(-0.64, 3.02) * mm, "end": v(-0.74, 2.94) * mm});
            skLineSegment(sketch, "E2877", {"start": v(-0.74, 2.94) * mm, "end": v(-0.82, 2.83) * mm});
            skLineSegment(sketch, "E2878", {"start": v(-0.82, 2.83) * mm, "end": v(-0.88, 2.7) * mm});
            skLineSegment(sketch, "E2879", {"start": v(-0.88, 2.7) * mm, "end": v(-0.93, 2.53) * mm});
            skLineSegment(sketch, "E2880", {"start": v(-0.93, 2.53) * mm, "end": v(-0.96, 2.38) * mm});
            skLineSegment(sketch, "E2881", {"start": v(-0.96, 2.38) * mm, "end": v(-0.97, 2.25) * mm});
            skLineSegment(sketch, "E2882", {"start": v(-0.97, 2.25) * mm, "end": v(-0.96, 2.13) * mm});
            skLineSegment(sketch, "E2883", {"start": v(-0.96, 2.13) * mm, "end": v(-0.93, 2.04) * mm});
            skLineSegment(sketch, "E2884", {"start": v(-0.93, 2.04) * mm, "end": v(-0.91, 2) * mm});
            skLineSegment(sketch, "E2885", {"start": v(-0.91, 2) * mm, "end": v(-0.9, 1.94) * mm});
            skLineSegment(sketch, "E2886", {"start": v(-0.9, 1.94) * mm, "end": v(-0.85, 1.86) * mm});
            skLineSegment(sketch, "E2887", {"start": v(-0.85, 1.86) * mm, "end": v(-0.8, 1.8) * mm});
            skLineSegment(sketch, "E2888", {"start": v(-0.8, 1.8) * mm, "end": v(-0.74, 1.75) * mm});
            skLineSegment(sketch, "E2889", {"start": v(-0.74, 1.75) * mm, "end": v(-0.67, 1.7) * mm});
            skLineSegment(sketch, "E2890", {"start": v(-0.67, 1.7) * mm, "end": v(-0.6, 1.68) * mm});
            skLineSegment(sketch, "E2891", {"start": v(-0.6, 1.68) * mm, "end": v(-0.54, 1.67) * mm});
            skLineSegment(sketch, "E2892", {"start": v(-0.54, 1.67) * mm, "end": v(-0.48, 1.68) * mm});
            skLineSegment(sketch, "E2893", {"start": v(-0.48, 1.68) * mm, "end": v(-0.42, 1.7) * mm});
            skLineSegment(sketch, "E2894", {"start": v(5.74, 1.96) * mm, "end": v(5.84, 2) * mm});
            skLineSegment(sketch, "E2895", {"start": v(5.84, 2) * mm, "end": v(5.95, 2.04) * mm});
            skLineSegment(sketch, "E2896", {"start": v(5.95, 2.04) * mm, "end": v(6.07, 2.1) * mm});
            skLineSegment(sketch, "E2897", {"start": v(6.07, 2.1) * mm, "end": v(6.22, 2.16) * mm});
            skLineSegment(sketch, "E2898", {"start": v(6.22, 2.16) * mm, "end": v(6.44, 2.25) * mm});
            skLineSegment(sketch, "E2899", {"start": v(6.44, 2.25) * mm, "end": v(6.68, 2.31) * mm});
            skLineSegment(sketch, "E2900", {"start": v(6.68, 2.31) * mm, "end": v(6.92, 2.34) * mm});
            skLineSegment(sketch, "E2901", {"start": v(6.92, 2.34) * mm, "end": v(7.13, 2.33) * mm});
            skLineSegment(sketch, "E2902", {"start": v(7.13, 2.33) * mm, "end": v(7.18, 2.32) * mm});
            skLineSegment(sketch, "E2903", {"start": v(7.18, 2.32) * mm, "end": v(7.24, 2.31) * mm});
            skLineSegment(sketch, "E2904", {"start": v(7.24, 2.31) * mm, "end": v(7.3, 2.3) * mm});
            skLineSegment(sketch, "E2905", {"start": v(7.3, 2.3) * mm, "end": v(7.34, 2.3) * mm});
            skLineSegment(sketch, "E2906", {"start": v(7.34, 2.3) * mm, "end": v(7.44, 2.28) * mm});
            skLineSegment(sketch, "E2907", {"start": v(7.44, 2.28) * mm, "end": v(7.5, 2.36) * mm});
            skLineSegment(sketch, "E2908", {"start": v(7.5, 2.36) * mm, "end": v(7.52, 2.4) * mm});
            skLineSegment(sketch, "E2909", {"start": v(7.52, 2.4) * mm, "end": v(7.55, 2.46) * mm});
            skLineSegment(sketch, "E2910", {"start": v(7.55, 2.46) * mm, "end": v(7.57, 2.51) * mm});
            skLineSegment(sketch, "E2911", {"start": v(7.57, 2.51) * mm, "end": v(7.6, 2.56) * mm});
            skLineSegment(sketch, "E2912", {"start": v(7.6, 2.56) * mm, "end": v(7.62, 2.61) * mm});
            skLineSegment(sketch, "E2913", {"start": v(7.62, 2.61) * mm, "end": v(7.64, 2.66) * mm});
            skLineSegment(sketch, "E2914", {"start": v(7.64, 2.66) * mm, "end": v(7.67, 2.71) * mm});
            skLineSegment(sketch, "E2915", {"start": v(7.67, 2.71) * mm, "end": v(7.69, 2.75) * mm});
            skLineSegment(sketch, "E2916", {"start": v(7.69, 2.75) * mm, "end": v(7.71, 2.8) * mm});
            skLineSegment(sketch, "E2917", {"start": v(7.71, 2.8) * mm, "end": v(7.74, 2.84) * mm});
            skLineSegment(sketch, "E2918", {"start": v(7.74, 2.84) * mm, "end": v(7.75, 2.87) * mm});
            skLineSegment(sketch, "E2919", {"start": v(7.75, 2.87) * mm, "end": v(7.75, 2.9) * mm});
            skLineSegment(sketch, "E2920", {"start": v(7.75, 2.9) * mm, "end": v(7.72, 2.9) * mm});
            skLineSegment(sketch, "E2921", {"start": v(7.72, 2.9) * mm, "end": v(7.63, 2.9) * mm});
            skLineSegment(sketch, "E2922", {"start": v(7.63, 2.9) * mm, "end": v(7.5, 2.9) * mm});
            skLineSegment(sketch, "E2923", {"start": v(7.5, 2.9) * mm, "end": v(7.37, 2.9) * mm});
            skLineSegment(sketch, "E2924", {"start": v(7.37, 2.9) * mm, "end": v(7.17, 2.88) * mm});
            skLineSegment(sketch, "E2925", {"start": v(7.17, 2.88) * mm, "end": v(7, 2.85) * mm});
            skLineSegment(sketch, "E2926", {"start": v(7, 2.85) * mm, "end": v(6.85, 2.8) * mm});
            skLineSegment(sketch, "E2927", {"start": v(6.85, 2.8) * mm, "end": v(6.7, 2.75) * mm});
            skLineSegment(sketch, "E2928", {"start": v(6.7, 2.75) * mm, "end": v(6.6, 2.7) * mm});
            skLineSegment(sketch, "E2929", {"start": v(6.6, 2.7) * mm, "end": v(6.5, 2.65) * mm});
            skLineSegment(sketch, "E2930", {"start": v(6.5, 2.65) * mm, "end": v(6.37, 2.57) * mm});
            skLineSegment(sketch, "E2931", {"start": v(6.37, 2.57) * mm, "end": v(6.2, 2.45) * mm});
            skLineSegment(sketch, "E2932", {"start": v(6.2, 2.45) * mm, "end": v(6.1, 2.38) * mm});
            skLineSegment(sketch, "E2933", {"start": v(6.1, 2.38) * mm, "end": v(6.02, 2.32) * mm});
            skLineSegment(sketch, "E2934", {"start": v(6.02, 2.32) * mm, "end": v(5.93, 2.24) * mm});
            skLineSegment(sketch, "E2935", {"start": v(5.93, 2.24) * mm, "end": v(5.81, 2.13) * mm});
            skLineSegment(sketch, "E2936", {"start": v(5.81, 2.13) * mm, "end": v(5.78, 2.1) * mm});
            skLineSegment(sketch, "E2937", {"start": v(5.78, 2.1) * mm, "end": v(5.73, 2.06) * mm});
            skLineSegment(sketch, "E2938", {"start": v(5.73, 2.06) * mm, "end": v(5.7, 2.02) * mm});
            skLineSegment(sketch, "E2939", {"start": v(5.7, 2.02) * mm, "end": v(5.65, 1.99) * mm});
            skLineSegment(sketch, "E2940", {"start": v(5.65, 1.99) * mm, "end": v(5.62, 1.96) * mm});
            skLineSegment(sketch, "E2941", {"start": v(5.62, 1.96) * mm, "end": v(5.6, 1.94) * mm});
            skLineSegment(sketch, "E2942", {"start": v(5.6, 1.94) * mm, "end": v(5.57, 1.92) * mm});
            skLineSegment(sketch, "E2943", {"start": v(5.57, 1.92) * mm, "end": v(5.57, 1.91) * mm});
            skLineSegment(sketch, "E2944", {"start": v(5.57, 1.91) * mm, "end": v(5.57, 1.9) * mm});
            skLineSegment(sketch, "E2945", {"start": v(5.57, 1.9) * mm, "end": v(5.6, 1.92) * mm});
            skLineSegment(sketch, "E2946", {"start": v(5.6, 1.92) * mm, "end": v(5.65, 1.93) * mm});
            skLineSegment(sketch, "E2947", {"start": v(5.65, 1.93) * mm, "end": v(5.74, 1.96) * mm});
            skSolve(sketch);
        }
        {
            var Q0;
            Q0=makeQuery(id+"F0.imprint","IMPRINT",FACE,{"disambiguationData":[TD([[makeQuery(id+"F0.imprint","IMPRINT",EDGE,{"derivedFrom":sQuery(id+"F0.wireOp",EDGE,"E0")}),-1.0]])]});
            extrude(context, id + "F1", {"entities" : qUnion([Q0]), "depth" : 2 * mm});
        }
        {
            var Q0;
            Q0=qCreatedBy(makeId("Top.planeOp"),FACE);
            var sketch = newSketch(context, id + "F2", { "sketchPlane" : qUnion([Q0])});
            skCircle(sketch, "E2948", {"center": v(-0.2, -6.86) * mm, "radius": 1.25 * mm});
            skCircle(sketch, "E2949", {"center": v(-0.2, -6.86) * mm, "radius": 0.75 * mm});
            skSolve(sketch);
        }
        {
            var Q0;
            Q0=makeQuery(id+"F2.imprint","IMPRINT",FACE,{"disambiguationData":[TD([[makeQuery(id+"F2.imprint","IMPRINT",EDGE,{"derivedFrom":sQuery(id+"F2.wireOp",EDGE,"E2948")}),1.0]])]});
            extrude(context, id + "F3", {"entities" : qUnion([Q0]), "operationType" : NewBodyOperationType.ADD, "depth" : 2 * mm});
        }
    });
